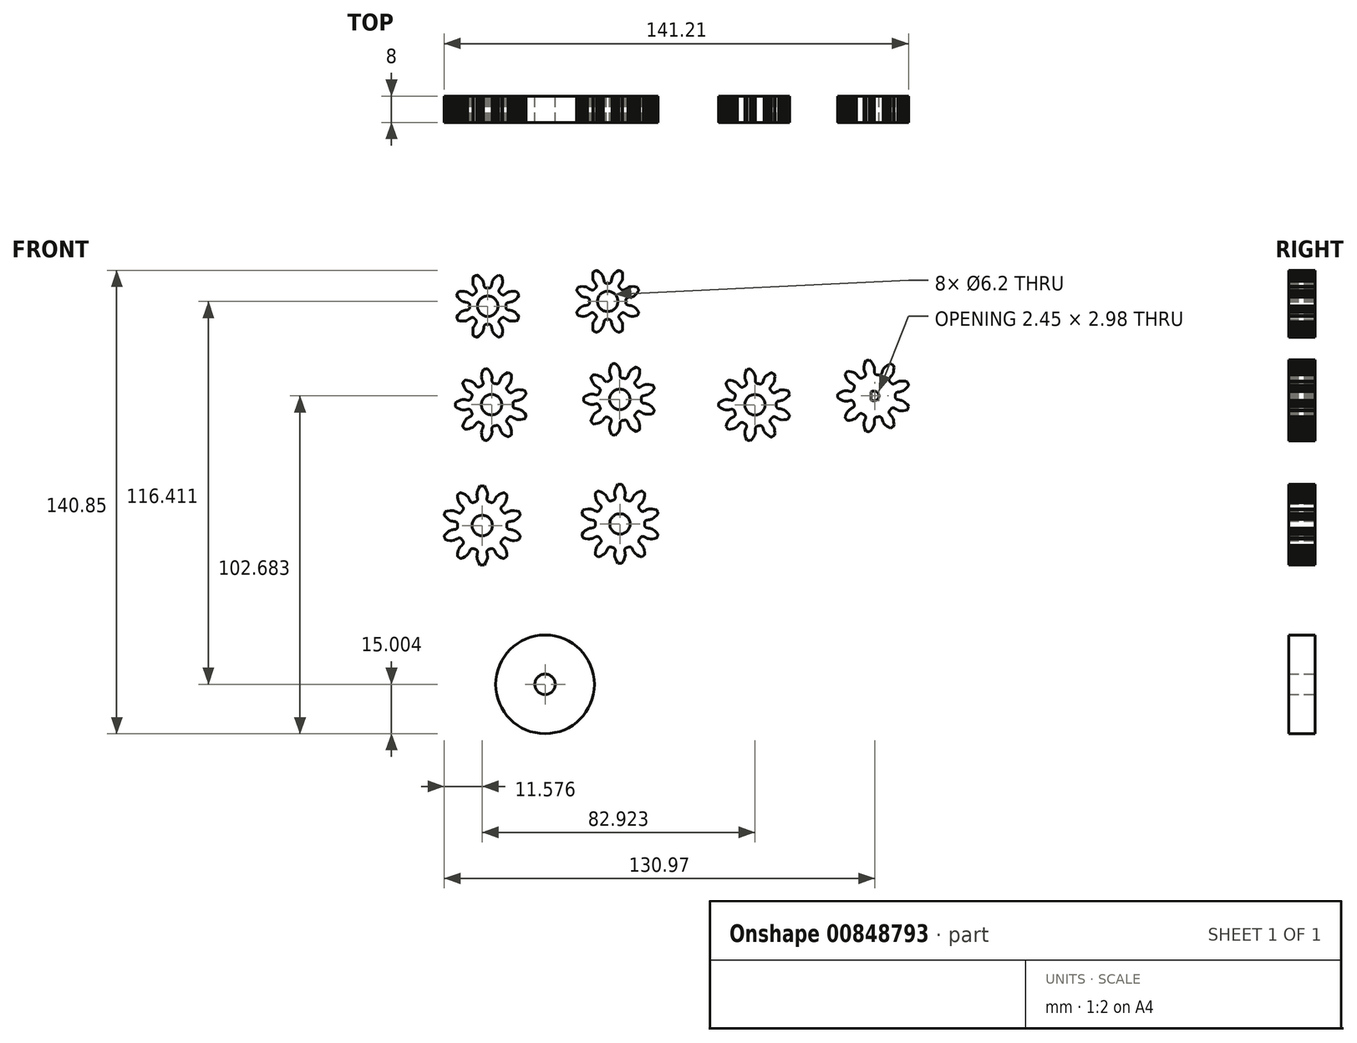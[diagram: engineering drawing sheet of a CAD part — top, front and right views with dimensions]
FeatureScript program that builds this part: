
annotation { "Feature Type Name" : "Feature", "Feature Type Description" : "" }
export const myFeature = defineFeature(function(context is Context, id is Id, definition is map)
    precondition{}
    {
        {
            var Q0;
            Q0=qCreatedBy(makeId("Front.planeOp"),FACE);
            var sketch = newSketch(context, id + "F0", { "sketchPlane" : qUnion([Q0])});
            skLineSegment(sketch, "E0", {"start": v(23.6, 118.61) * mm, "end": v(23.04, 118.9) * mm});
            skLineSegment(sketch, "E1", {"start": v(24.13, 118.4) * mm, "end": v(23.6, 118.61) * mm});
            skLineSegment(sketch, "E2", {"start": v(24.61, 118.29) * mm, "end": v(24.13, 118.4) * mm});
            skLineSegment(sketch, "E3", {"start": v(25.01, 118.25) * mm, "end": v(24.61, 118.29) * mm});
            skLineSegment(sketch, "E4", {"start": v(25.13, 118.25) * mm, "end": v(25.01, 118.25) * mm});
            skLineSegment(sketch, "E5", {"start": v(25.2, 118.26) * mm, "end": v(25.13, 118.25) * mm});
            skLineSegment(sketch, "E6", {"start": v(25.4, 118.3) * mm, "end": v(25.2, 118.26) * mm});
            skLineSegment(sketch, "E7", {"start": v(25.81, 118.38) * mm, "end": v(25.4, 118.3) * mm});
            skLineSegment(sketch, "E8", {"start": v(26.33, 118.48) * mm, "end": v(25.81, 118.38) * mm});
            skArc(sketch, "E9", {"start": v(22.48, 120.41) * mm, "mid": v(22.47, 119.85) * mm, "end": v(22.48, 119.28) * mm});
            skLineSegment(sketch, "E10", {"start": v(23.04, 120.8) * mm, "end": v(22.48, 120.41) * mm});
            skLineSegment(sketch, "E11", {"start": v(23.6, 121.08) * mm, "end": v(23.04, 120.8) * mm});
            skLineSegment(sketch, "E12", {"start": v(24.13, 121.3) * mm, "end": v(23.6, 121.08) * mm});
            skLineSegment(sketch, "E13", {"start": v(24.61, 121.41) * mm, "end": v(24.13, 121.3) * mm});
            skLineSegment(sketch, "E14", {"start": v(25.01, 121.45) * mm, "end": v(24.61, 121.41) * mm});
            skLineSegment(sketch, "E15", {"start": v(25.13, 121.45) * mm, "end": v(25.01, 121.45) * mm});
            skLineSegment(sketch, "E16", {"start": v(25.2, 121.43) * mm, "end": v(25.13, 121.45) * mm});
            skLineSegment(sketch, "E17", {"start": v(25.4, 121.4) * mm, "end": v(25.2, 121.43) * mm});
            skLineSegment(sketch, "E18", {"start": v(25.81, 121.32) * mm, "end": v(25.4, 121.4) * mm});
            skLineSegment(sketch, "E19", {"start": v(26.33, 121.22) * mm, "end": v(25.81, 121.32) * mm});
            skArc(sketch, "E20", {"start": v(26.33, 121.22) * mm, "mid": v(26.9, 121.32) * mm, "end": v(27.26, 121.78) * mm});
            skArc(sketch, "E21", {"start": v(27.47, 122.36) * mm, "mid": v(27.36, 122.07) * mm, "end": v(27.26, 121.78) * mm});
            skArc(sketch, "E22", {"start": v(27.47, 122.36) * mm, "mid": v(27.5, 122.94) * mm, "end": v(27.12, 123.39) * mm});
            skLineSegment(sketch, "E23", {"start": v(24.88, 125.83) * mm, "end": v(24.7, 126.48) * mm});
            skLineSegment(sketch, "E24", {"start": v(25.11, 125.25) * mm, "end": v(24.88, 125.83) * mm});
            skLineSegment(sketch, "E25", {"start": v(25.38, 124.75) * mm, "end": v(25.11, 125.25) * mm});
            skLineSegment(sketch, "E26", {"start": v(25.68, 124.34) * mm, "end": v(25.38, 124.75) * mm});
            skLineSegment(sketch, "E27", {"start": v(25.96, 124.06) * mm, "end": v(25.68, 124.34) * mm});
            skLineSegment(sketch, "E28", {"start": v(26.05, 123.99) * mm, "end": v(25.96, 124.06) * mm});
            skLineSegment(sketch, "E29", {"start": v(26.12, 123.94) * mm, "end": v(26.05, 123.99) * mm});
            skLineSegment(sketch, "E30", {"start": v(26.3, 123.84) * mm, "end": v(26.12, 123.94) * mm});
            skLineSegment(sketch, "E31", {"start": v(26.66, 123.65) * mm, "end": v(26.3, 123.84) * mm});
            skLineSegment(sketch, "E32", {"start": v(27.12, 123.39) * mm, "end": v(26.66, 123.65) * mm});
            skArc(sketch, "E33", {"start": v(25.42, 127.34) * mm, "mid": v(25.04, 126.92) * mm, "end": v(24.7, 126.48) * mm});
            skLineSegment(sketch, "E34", {"start": v(26.09, 127.27) * mm, "end": v(25.42, 127.34) * mm});
            skLineSegment(sketch, "E35", {"start": v(26.7, 127.14) * mm, "end": v(26.09, 127.27) * mm});
            skLineSegment(sketch, "E36", {"start": v(27.24, 126.96) * mm, "end": v(26.7, 127.14) * mm});
            skLineSegment(sketch, "E37", {"start": v(27.69, 126.74) * mm, "end": v(27.24, 126.96) * mm});
            skLineSegment(sketch, "E38", {"start": v(28.02, 126.51) * mm, "end": v(27.69, 126.74) * mm});
            skLineSegment(sketch, "E39", {"start": v(28.1, 126.43) * mm, "end": v(28.02, 126.51) * mm});
            skLineSegment(sketch, "E40", {"start": v(28.16, 126.37) * mm, "end": v(28.1, 126.43) * mm});
            skLineSegment(sketch, "E41", {"start": v(28.29, 126.22) * mm, "end": v(28.16, 126.37) * mm});
            skLineSegment(sketch, "E42", {"start": v(28.55, 125.9) * mm, "end": v(28.29, 126.22) * mm});
            skLineSegment(sketch, "E43", {"start": v(28.88, 125.5) * mm, "end": v(28.55, 125.9) * mm});
            skArc(sketch, "E44", {"start": v(28.88, 125.5) * mm, "mid": v(29.38, 125.2) * mm, "end": v(29.96, 125.32) * mm});
            skArc(sketch, "E45", {"start": v(30.49, 125.63) * mm, "mid": v(30.22, 125.48) * mm, "end": v(29.96, 125.32) * mm});
            skArc(sketch, "E46", {"start": v(30.49, 125.63) * mm, "mid": v(30.88, 126.06) * mm, "end": v(30.88, 126.64) * mm});
            skLineSegment(sketch, "E47", {"start": v(30.73, 129.95) * mm, "end": v(31, 130.57) * mm});
            skLineSegment(sketch, "E48", {"start": v(30.54, 129.36) * mm, "end": v(30.73, 129.95) * mm});
            skLineSegment(sketch, "E49", {"start": v(30.43, 128.8) * mm, "end": v(30.54, 129.36) * mm});
            skLineSegment(sketch, "E50", {"start": v(30.4, 128.3) * mm, "end": v(30.43, 128.8) * mm});
            skLineSegment(sketch, "E51", {"start": v(30.42, 127.9) * mm, "end": v(30.4, 128.3) * mm});
            skLineSegment(sketch, "E52", {"start": v(30.45, 127.78) * mm, "end": v(30.42, 127.9) * mm});
            skLineSegment(sketch, "E53", {"start": v(30.47, 127.7) * mm, "end": v(30.45, 127.78) * mm});
            skLineSegment(sketch, "E54", {"start": v(30.55, 127.52) * mm, "end": v(30.47, 127.7) * mm});
            skLineSegment(sketch, "E55", {"start": v(30.7, 127.14) * mm, "end": v(30.55, 127.52) * mm});
            skLineSegment(sketch, "E56", {"start": v(30.88, 126.64) * mm, "end": v(30.7, 127.14) * mm});
            skArc(sketch, "E57", {"start": v(32.12, 130.77) * mm, "mid": v(31.56, 130.68) * mm, "end": v(31, 130.57) * mm});
            skLineSegment(sketch, "E58", {"start": v(32.59, 130.28) * mm, "end": v(32.12, 130.77) * mm});
            skLineSegment(sketch, "E59", {"start": v(32.97, 129.79) * mm, "end": v(32.59, 130.28) * mm});
            skLineSegment(sketch, "E60", {"start": v(33.27, 129.3) * mm, "end": v(32.97, 129.79) * mm});
            skLineSegment(sketch, "E61", {"start": v(33.47, 128.84) * mm, "end": v(33.27, 129.3) * mm});
            skLineSegment(sketch, "E62", {"start": v(33.58, 128.46) * mm, "end": v(33.47, 128.84) * mm});
            skLineSegment(sketch, "E63", {"start": v(33.6, 128.34) * mm, "end": v(33.58, 128.46) * mm});
            skLineSegment(sketch, "E64", {"start": v(33.6, 128.26) * mm, "end": v(33.6, 128.34) * mm});
            skLineSegment(sketch, "E65", {"start": v(33.6, 128.05) * mm, "end": v(33.6, 128.26) * mm});
            skLineSegment(sketch, "E66", {"start": v(33.59, 127.65) * mm, "end": v(33.6, 128.05) * mm});
            skLineSegment(sketch, "E67", {"start": v(33.58, 127.12) * mm, "end": v(33.59, 127.65) * mm});
            skArc(sketch, "E68", {"start": v(33.58, 127.12) * mm, "mid": v(33.78, 126.57) * mm, "end": v(34.3, 126.3) * mm});
            skArc(sketch, "E69", {"start": v(34.9, 126.19) * mm, "mid": v(34.6, 126.25) * mm, "end": v(34.3, 126.3) * mm});
            skArc(sketch, "E70", {"start": v(34.9, 126.19) * mm, "mid": v(35.48, 126.27) * mm, "end": v(35.85, 126.72) * mm});
            skLineSegment(sketch, "E71", {"start": v(37.87, 129.35) * mm, "end": v(38.47, 129.65) * mm});
            skLineSegment(sketch, "E72", {"start": v(37.34, 129.02) * mm, "end": v(37.87, 129.35) * mm});
            skLineSegment(sketch, "E73", {"start": v(36.9, 128.66) * mm, "end": v(37.34, 129.02) * mm});
            skLineSegment(sketch, "E74", {"start": v(36.54, 128.3) * mm, "end": v(36.9, 128.66) * mm});
            skLineSegment(sketch, "E75", {"start": v(36.31, 127.98) * mm, "end": v(36.54, 128.3) * mm});
            skLineSegment(sketch, "E76", {"start": v(36.26, 127.87) * mm, "end": v(36.31, 127.98) * mm});
            skLineSegment(sketch, "E77", {"start": v(36.23, 127.8) * mm, "end": v(36.26, 127.87) * mm});
            skLineSegment(sketch, "E78", {"start": v(36.16, 127.6) * mm, "end": v(36.23, 127.8) * mm});
            skLineSegment(sketch, "E79", {"start": v(36.02, 127.22) * mm, "end": v(36.16, 127.6) * mm});
            skLineSegment(sketch, "E80", {"start": v(35.85, 126.72) * mm, "end": v(36.02, 127.22) * mm});
            skArc(sketch, "E81", {"start": v(39.45, 129.08) * mm, "mid": v(38.97, 129.38) * mm, "end": v(38.47, 129.65) * mm});
            skLineSegment(sketch, "E82", {"start": v(39.5, 128.4) * mm, "end": v(39.45, 129.08) * mm});
            skLineSegment(sketch, "E83", {"start": v(39.48, 127.78) * mm, "end": v(39.5, 128.4) * mm});
            skLineSegment(sketch, "E84", {"start": v(39.39, 127.22) * mm, "end": v(39.48, 127.78) * mm});
            skLineSegment(sketch, "E85", {"start": v(39.25, 126.74) * mm, "end": v(39.39, 127.22) * mm});
            skLineSegment(sketch, "E86", {"start": v(39.09, 126.37) * mm, "end": v(39.25, 126.74) * mm});
            skLineSegment(sketch, "E87", {"start": v(39.02, 126.27) * mm, "end": v(39.09, 126.37) * mm});
            skLineSegment(sketch, "E88", {"start": v(38.97, 126.21) * mm, "end": v(39.02, 126.27) * mm});
            skLineSegment(sketch, "E89", {"start": v(38.84, 126.06) * mm, "end": v(38.97, 126.21) * mm});
            skLineSegment(sketch, "E90", {"start": v(38.57, 125.75) * mm, "end": v(38.84, 126.06) * mm});
            skLineSegment(sketch, "E91", {"start": v(38.23, 125.35) * mm, "end": v(38.57, 125.75) * mm});
            skArc(sketch, "E92", {"start": v(38.23, 125.35) * mm, "mid": v(38.03, 124.8) * mm, "end": v(38.24, 124.26) * mm});
            skArc(sketch, "E93", {"start": v(38.64, 123.79) * mm, "mid": v(38.45, 124.03) * mm, "end": v(38.24, 124.26) * mm});
            skArc(sketch, "E94", {"start": v(38.64, 123.79) * mm, "mid": v(39.14, 123.48) * mm, "end": v(39.71, 123.58) * mm});
            skLineSegment(sketch, "E95", {"start": v(42.95, 124.3) * mm, "end": v(43.6, 124.14) * mm});
            skLineSegment(sketch, "E96", {"start": v(42.33, 124.39) * mm, "end": v(42.95, 124.3) * mm});
            skLineSegment(sketch, "E97", {"start": v(41.76, 124.4) * mm, "end": v(42.33, 124.39) * mm});
            skLineSegment(sketch, "E98", {"start": v(41.26, 124.35) * mm, "end": v(41.76, 124.4) * mm});
            skLineSegment(sketch, "E99", {"start": v(40.87, 124.25) * mm, "end": v(41.26, 124.35) * mm});
            skLineSegment(sketch, "E100", {"start": v(40.76, 124.2) * mm, "end": v(40.87, 124.25) * mm});
            skLineSegment(sketch, "E101", {"start": v(40.69, 124.16) * mm, "end": v(40.76, 124.2) * mm});
            skLineSegment(sketch, "E102", {"start": v(40.51, 124.06) * mm, "end": v(40.69, 124.16) * mm});
            skLineSegment(sketch, "E103", {"start": v(40.16, 123.85) * mm, "end": v(40.51, 124.06) * mm});
            skLineSegment(sketch, "E104", {"start": v(39.71, 123.58) * mm, "end": v(40.16, 123.85) * mm});
            skArc(sketch, "E105", {"start": v(43.99, 123.08) * mm, "mid": v(43.8, 123.61) * mm, "end": v(43.6, 124.14) * mm});
            skLineSegment(sketch, "E106", {"start": v(43.59, 122.53) * mm, "end": v(43.99, 123.08) * mm});
            skLineSegment(sketch, "E107", {"start": v(43.17, 122.07) * mm, "end": v(43.59, 122.53) * mm});
            skLineSegment(sketch, "E108", {"start": v(42.74, 121.69) * mm, "end": v(43.17, 122.07) * mm});
            skLineSegment(sketch, "E109", {"start": v(42.33, 121.4) * mm, "end": v(42.74, 121.69) * mm});
            skLineSegment(sketch, "E110", {"start": v(41.97, 121.24) * mm, "end": v(42.33, 121.4) * mm});
            skLineSegment(sketch, "E111", {"start": v(41.85, 121.2) * mm, "end": v(41.97, 121.24) * mm});
            skLineSegment(sketch, "E112", {"start": v(41.77, 121.19) * mm, "end": v(41.85, 121.2) * mm});
            skLineSegment(sketch, "E113", {"start": v(41.57, 121.15) * mm, "end": v(41.77, 121.19) * mm});
            skLineSegment(sketch, "E114", {"start": v(41.17, 121.09) * mm, "end": v(41.57, 121.15) * mm});
            skLineSegment(sketch, "E115", {"start": v(40.65, 121) * mm, "end": v(41.17, 121.09) * mm});
            skArc(sketch, "E116", {"start": v(40.65, 121) * mm, "mid": v(40.14, 120.71) * mm, "end": v(39.96, 120.16) * mm});
            skArc(sketch, "E117", {"start": v(39.96, 119.54) * mm, "mid": v(39.97, 119.85) * mm, "end": v(39.96, 120.16) * mm});
            skArc(sketch, "E118", {"start": v(39.96, 119.54) * mm, "mid": v(40.14, 118.99) * mm, "end": v(40.65, 118.7) * mm});
            skLineSegment(sketch, "E119", {"start": v(43.59, 117.17) * mm, "end": v(43.99, 116.62) * mm});
            skLineSegment(sketch, "E120", {"start": v(43.17, 117.63) * mm, "end": v(43.59, 117.17) * mm});
            skLineSegment(sketch, "E121", {"start": v(42.74, 118) * mm, "end": v(43.17, 117.63) * mm});
            skLineSegment(sketch, "E122", {"start": v(42.33, 118.29) * mm, "end": v(42.74, 118) * mm});
            skLineSegment(sketch, "E123", {"start": v(41.97, 118.46) * mm, "end": v(42.33, 118.29) * mm});
            skLineSegment(sketch, "E124", {"start": v(41.85, 118.5) * mm, "end": v(41.97, 118.46) * mm});
            skLineSegment(sketch, "E125", {"start": v(41.77, 118.51) * mm, "end": v(41.85, 118.5) * mm});
            skLineSegment(sketch, "E126", {"start": v(41.57, 118.55) * mm, "end": v(41.77, 118.51) * mm});
            skLineSegment(sketch, "E127", {"start": v(41.17, 118.61) * mm, "end": v(41.57, 118.55) * mm});
            skLineSegment(sketch, "E128", {"start": v(40.65, 118.7) * mm, "end": v(41.17, 118.61) * mm});
            skArc(sketch, "E129", {"start": v(43.6, 115.56) * mm, "mid": v(43.8, 116.09) * mm, "end": v(43.99, 116.62) * mm});
            skLineSegment(sketch, "E130", {"start": v(42.95, 115.4) * mm, "end": v(43.6, 115.56) * mm});
            skLineSegment(sketch, "E131", {"start": v(42.33, 115.31) * mm, "end": v(42.95, 115.4) * mm});
            skLineSegment(sketch, "E132", {"start": v(41.76, 115.3) * mm, "end": v(42.33, 115.31) * mm});
            skLineSegment(sketch, "E133", {"start": v(41.26, 115.35) * mm, "end": v(41.76, 115.3) * mm});
            skLineSegment(sketch, "E134", {"start": v(40.87, 115.45) * mm, "end": v(41.26, 115.35) * mm});
            skLineSegment(sketch, "E135", {"start": v(40.76, 115.5) * mm, "end": v(40.87, 115.45) * mm});
            skLineSegment(sketch, "E136", {"start": v(40.69, 115.53) * mm, "end": v(40.76, 115.5) * mm});
            skLineSegment(sketch, "E137", {"start": v(40.51, 115.64) * mm, "end": v(40.69, 115.53) * mm});
            skLineSegment(sketch, "E138", {"start": v(40.16, 115.85) * mm, "end": v(40.51, 115.64) * mm});
            skLineSegment(sketch, "E139", {"start": v(39.71, 116.12) * mm, "end": v(40.16, 115.85) * mm});
            skArc(sketch, "E140", {"start": v(39.71, 116.12) * mm, "mid": v(39.14, 116.22) * mm, "end": v(38.64, 115.91) * mm});
            skArc(sketch, "E141", {"start": v(38.24, 115.44) * mm, "mid": v(38.45, 115.67) * mm, "end": v(38.64, 115.91) * mm});
            skArc(sketch, "E142", {"start": v(38.24, 115.44) * mm, "mid": v(38.03, 114.9) * mm, "end": v(38.23, 114.35) * mm});
            skLineSegment(sketch, "E143", {"start": v(39.5, 111.29) * mm, "end": v(39.45, 110.62) * mm});
            skLineSegment(sketch, "E144", {"start": v(39.48, 111.92) * mm, "end": v(39.5, 111.29) * mm});
            skLineSegment(sketch, "E145", {"start": v(39.39, 112.48) * mm, "end": v(39.48, 111.92) * mm});
            skLineSegment(sketch, "E146", {"start": v(39.25, 112.96) * mm, "end": v(39.39, 112.48) * mm});
            skLineSegment(sketch, "E147", {"start": v(39.09, 113.32) * mm, "end": v(39.25, 112.96) * mm});
            skLineSegment(sketch, "E148", {"start": v(39.02, 113.43) * mm, "end": v(39.09, 113.32) * mm});
            skLineSegment(sketch, "E149", {"start": v(38.97, 113.49) * mm, "end": v(39.02, 113.43) * mm});
            skLineSegment(sketch, "E150", {"start": v(38.84, 113.64) * mm, "end": v(38.97, 113.49) * mm});
            skLineSegment(sketch, "E151", {"start": v(38.57, 113.95) * mm, "end": v(38.84, 113.64) * mm});
            skLineSegment(sketch, "E152", {"start": v(38.23, 114.35) * mm, "end": v(38.57, 113.95) * mm});
            skArc(sketch, "E153", {"start": v(38.47, 110.05) * mm, "mid": v(38.97, 110.32) * mm, "end": v(39.45, 110.62) * mm});
            skLineSegment(sketch, "E154", {"start": v(37.87, 110.35) * mm, "end": v(38.47, 110.05) * mm});
            skLineSegment(sketch, "E155", {"start": v(37.34, 110.68) * mm, "end": v(37.87, 110.35) * mm});
            skLineSegment(sketch, "E156", {"start": v(36.9, 111.04) * mm, "end": v(37.34, 110.68) * mm});
            skLineSegment(sketch, "E157", {"start": v(36.54, 111.4) * mm, "end": v(36.9, 111.04) * mm});
            skLineSegment(sketch, "E158", {"start": v(36.31, 111.72) * mm, "end": v(36.54, 111.4) * mm});
            skLineSegment(sketch, "E159", {"start": v(36.26, 111.83) * mm, "end": v(36.31, 111.72) * mm});
            skLineSegment(sketch, "E160", {"start": v(36.23, 111.9) * mm, "end": v(36.26, 111.83) * mm});
            skLineSegment(sketch, "E161", {"start": v(36.16, 112.1) * mm, "end": v(36.23, 111.9) * mm});
            skLineSegment(sketch, "E162", {"start": v(36.02, 112.48) * mm, "end": v(36.16, 112.1) * mm});
            skLineSegment(sketch, "E163", {"start": v(35.85, 112.98) * mm, "end": v(36.02, 112.48) * mm});
            skArc(sketch, "E164", {"start": v(35.85, 112.98) * mm, "mid": v(35.48, 113.43) * mm, "end": v(34.9, 113.5) * mm});
            skArc(sketch, "E165", {"start": v(-4.68, 111.79) * mm, "mid": v(-4.38, 111.83) * mm, "end": v(-4.07, 111.9) * mm});
            skArc(sketch, "E166", {"start": v(-4.68, 111.79) * mm, "mid": v(-5.2, 111.5) * mm, "end": v(-5.4, 110.96) * mm});
            skLineSegment(sketch, "E167", {"start": v(-6.39, 107.8) * mm, "end": v(-6.86, 107.32) * mm});
            skLineSegment(sketch, "E168", {"start": v(-6, 108.3) * mm, "end": v(-6.39, 107.8) * mm});
            skLineSegment(sketch, "E169", {"start": v(-5.7, 108.78) * mm, "end": v(-6, 108.3) * mm});
            skLineSegment(sketch, "E170", {"start": v(-5.5, 109.24) * mm, "end": v(-5.7, 108.78) * mm});
            skLineSegment(sketch, "E171", {"start": v(-5.4, 109.62) * mm, "end": v(-5.5, 109.24) * mm});
            skLineSegment(sketch, "E172", {"start": v(-5.38, 109.74) * mm, "end": v(-5.4, 109.62) * mm});
            skLineSegment(sketch, "E173", {"start": v(-5.38, 109.82) * mm, "end": v(-5.38, 109.74) * mm});
            skLineSegment(sketch, "E174", {"start": v(-5.38, 110.03) * mm, "end": v(-5.38, 109.82) * mm});
            skLineSegment(sketch, "E175", {"start": v(-5.39, 110.43) * mm, "end": v(-5.38, 110.03) * mm});
            skLineSegment(sketch, "E176", {"start": v(-5.4, 110.96) * mm, "end": v(-5.39, 110.43) * mm});
            skArc(sketch, "E177", {"start": v(-7.97, 107.51) * mm, "mid": v(-7.41, 107.4) * mm, "end": v(-6.86, 107.32) * mm});
            skLineSegment(sketch, "E178", {"start": v(-8.24, 108.13) * mm, "end": v(-7.97, 107.51) * mm});
            skLineSegment(sketch, "E179", {"start": v(-8.44, 108.72) * mm, "end": v(-8.24, 108.13) * mm});
            skLineSegment(sketch, "E180", {"start": v(-8.55, 109.28) * mm, "end": v(-8.44, 108.72) * mm});
            skLineSegment(sketch, "E181", {"start": v(-8.58, 109.78) * mm, "end": v(-8.55, 109.28) * mm});
            skLineSegment(sketch, "E182", {"start": v(-8.55, 110.18) * mm, "end": v(-8.58, 109.78) * mm});
            skLineSegment(sketch, "E183", {"start": v(-8.53, 110.3) * mm, "end": v(-8.55, 110.18) * mm});
            skLineSegment(sketch, "E184", {"start": v(-8.5, 110.37) * mm, "end": v(-8.53, 110.3) * mm});
            skLineSegment(sketch, "E185", {"start": v(-8.43, 110.56) * mm, "end": v(-8.5, 110.37) * mm});
            skLineSegment(sketch, "E186", {"start": v(-8.28, 110.95) * mm, "end": v(-8.43, 110.56) * mm});
            skArc(sketch, "E187", {"start": v(-8.1, 111.44) * mm, "mid": v(-8.1, 112.02) * mm, "end": v(-8.48, 112.46) * mm});
            skArc(sketch, "E188", {"start": v(-9.02, 112.76) * mm, "mid": v(-8.75, 112.6) * mm, "end": v(-8.48, 112.46) * mm});
            skArc(sketch, "E189", {"start": v(-9.02, 112.76) * mm, "mid": v(-9.59, 112.88) * mm, "end": v(-10.1, 112.6) * mm});
            skLineSegment(sketch, "E190", {"start": v(-12.89, 110.8) * mm, "end": v(-13.56, 110.74) * mm});
            skLineSegment(sketch, "E191", {"start": v(-12.27, 110.94) * mm, "end": v(-12.89, 110.8) * mm});
            skLineSegment(sketch, "E192", {"start": v(-11.73, 111.12) * mm, "end": v(-12.27, 110.94) * mm});
            skLineSegment(sketch, "E193", {"start": v(-11.28, 111.34) * mm, "end": v(-11.73, 111.12) * mm});
            skLineSegment(sketch, "E194", {"start": v(-10.95, 111.57) * mm, "end": v(-11.28, 111.34) * mm});
            skLineSegment(sketch, "E195", {"start": v(-10.87, 111.65) * mm, "end": v(-10.95, 111.57) * mm});
            skLineSegment(sketch, "E196", {"start": v(-10.81, 111.7) * mm, "end": v(-10.87, 111.65) * mm});
            skLineSegment(sketch, "E197", {"start": v(-10.68, 111.87) * mm, "end": v(-10.81, 111.7) * mm});
            skLineSegment(sketch, "E198", {"start": v(-10.43, 112.18) * mm, "end": v(-10.68, 111.87) * mm});
            skLineSegment(sketch, "E199", {"start": v(-10.1, 112.6) * mm, "end": v(-10.43, 112.18) * mm});
            skArc(sketch, "E200", {"start": v(-14.28, 111.6) * mm, "mid": v(-13.93, 111.16) * mm, "end": v(-13.56, 110.74) * mm});
            skLineSegment(sketch, "E201", {"start": v(-14.1, 112.25) * mm, "end": v(-14.28, 111.6) * mm});
            skLineSegment(sketch, "E202", {"start": v(-13.86, 112.83) * mm, "end": v(-14.1, 112.25) * mm});
            skLineSegment(sketch, "E203", {"start": v(-13.59, 113.33) * mm, "end": v(-13.86, 112.83) * mm});
            skLineSegment(sketch, "E204", {"start": v(-13.3, 113.74) * mm, "end": v(-13.59, 113.33) * mm});
            skLineSegment(sketch, "E205", {"start": v(-13.01, 114.02) * mm, "end": v(-13.3, 113.74) * mm});
            skLineSegment(sketch, "E206", {"start": v(-12.92, 114.1) * mm, "end": v(-13.01, 114.02) * mm});
            skLineSegment(sketch, "E207", {"start": v(-12.85, 114.14) * mm, "end": v(-12.92, 114.1) * mm});
            skLineSegment(sketch, "E208", {"start": v(-12.67, 114.24) * mm, "end": v(-12.85, 114.14) * mm});
            skLineSegment(sketch, "E209", {"start": v(-12.32, 114.44) * mm, "end": v(-12.67, 114.24) * mm});
            skLineSegment(sketch, "E210", {"start": v(-11.86, 114.7) * mm, "end": v(-12.32, 114.44) * mm});
            skArc(sketch, "E211", {"start": v(-11.86, 114.7) * mm, "mid": v(-11.48, 115.14) * mm, "end": v(-11.5, 115.72) * mm});
            skArc(sketch, "E212", {"start": v(-11.71, 116.3) * mm, "mid": v(-11.61, 116) * mm, "end": v(-11.5, 115.72) * mm});
            skArc(sketch, "E213", {"start": v(-11.71, 116.3) * mm, "mid": v(-12.07, 116.76) * mm, "end": v(-12.65, 116.86) * mm});
            skLineSegment(sketch, "E214", {"start": v(-15.93, 117.3) * mm, "end": v(-16.5, 117.67) * mm});
            skLineSegment(sketch, "E215", {"start": v(-15.38, 117) * mm, "end": v(-15.93, 117.3) * mm});
            skLineSegment(sketch, "E216", {"start": v(-14.85, 116.8) * mm, "end": v(-15.38, 117) * mm});
            skLineSegment(sketch, "E217", {"start": v(-14.36, 116.67) * mm, "end": v(-14.85, 116.8) * mm});
            skLineSegment(sketch, "E218", {"start": v(-13.96, 116.63) * mm, "end": v(-14.36, 116.67) * mm});
            skLineSegment(sketch, "E219", {"start": v(-13.84, 116.64) * mm, "end": v(-13.96, 116.63) * mm});
            skLineSegment(sketch, "E220", {"start": v(-13.76, 116.65) * mm, "end": v(-13.84, 116.64) * mm});
            skLineSegment(sketch, "E221", {"start": v(-13.56, 116.69) * mm, "end": v(-13.76, 116.65) * mm});
            skLineSegment(sketch, "E222", {"start": v(-13.16, 116.76) * mm, "end": v(-13.56, 116.69) * mm});
            skLineSegment(sketch, "E223", {"start": v(-12.65, 116.86) * mm, "end": v(-13.16, 116.76) * mm});
            skArc(sketch, "E224", {"start": v(-16.5, 118.8) * mm, "mid": v(-16.5, 118.23) * mm, "end": v(-16.5, 117.67) * mm});
            skLineSegment(sketch, "E225", {"start": v(-15.93, 119.17) * mm, "end": v(-16.5, 118.8) * mm});
            skLineSegment(sketch, "E226", {"start": v(-15.38, 119.47) * mm, "end": v(-15.93, 119.17) * mm});
            skLineSegment(sketch, "E227", {"start": v(-14.85, 119.68) * mm, "end": v(-15.38, 119.47) * mm});
            skLineSegment(sketch, "E228", {"start": v(-14.36, 119.8) * mm, "end": v(-14.85, 119.68) * mm});
            skLineSegment(sketch, "E229", {"start": v(-13.96, 119.83) * mm, "end": v(-14.36, 119.8) * mm});
            skLineSegment(sketch, "E230", {"start": v(-13.84, 119.83) * mm, "end": v(-13.96, 119.83) * mm});
            skLineSegment(sketch, "E231", {"start": v(-13.76, 119.82) * mm, "end": v(-13.84, 119.83) * mm});
            skLineSegment(sketch, "E232", {"start": v(-13.56, 119.78) * mm, "end": v(-13.76, 119.82) * mm});
            skLineSegment(sketch, "E233", {"start": v(-13.16, 119.7) * mm, "end": v(-13.56, 119.78) * mm});
            skLineSegment(sketch, "E234", {"start": v(-12.65, 119.6) * mm, "end": v(-13.16, 119.7) * mm});
            skArc(sketch, "E235", {"start": v(-12.65, 119.6) * mm, "mid": v(-12.07, 119.7) * mm, "end": v(-11.71, 120.16) * mm});
            skArc(sketch, "E236", {"start": v(-11.5, 120.74) * mm, "mid": v(-11.61, 120.46) * mm, "end": v(-11.71, 120.16) * mm});
            skArc(sketch, "E237", {"start": v(-11.5, 120.74) * mm, "mid": v(-11.48, 121.33) * mm, "end": v(-11.86, 121.77) * mm});
            skLineSegment(sketch, "E238", {"start": v(-14.1, 124.21) * mm, "end": v(-14.28, 124.86) * mm});
            skLineSegment(sketch, "E239", {"start": v(-13.86, 123.63) * mm, "end": v(-14.1, 124.21) * mm});
            skLineSegment(sketch, "E240", {"start": v(-13.59, 123.13) * mm, "end": v(-13.86, 123.63) * mm});
            skLineSegment(sketch, "E241", {"start": v(-13.3, 122.73) * mm, "end": v(-13.59, 123.13) * mm});
            skLineSegment(sketch, "E242", {"start": v(-13.01, 122.44) * mm, "end": v(-13.3, 122.73) * mm});
            skLineSegment(sketch, "E243", {"start": v(-12.92, 122.37) * mm, "end": v(-13.01, 122.44) * mm});
            skLineSegment(sketch, "E244", {"start": v(-12.85, 122.33) * mm, "end": v(-12.92, 122.37) * mm});
            skLineSegment(sketch, "E245", {"start": v(-12.67, 122.23) * mm, "end": v(-12.85, 122.33) * mm});
            skLineSegment(sketch, "E246", {"start": v(-12.32, 122.03) * mm, "end": v(-12.67, 122.23) * mm});
            skLineSegment(sketch, "E247", {"start": v(-11.86, 121.77) * mm, "end": v(-12.32, 122.03) * mm});
            skArc(sketch, "E248", {"start": v(-13.56, 125.73) * mm, "mid": v(-13.93, 125.3) * mm, "end": v(-14.28, 124.86) * mm});
            skLineSegment(sketch, "E249", {"start": v(-12.89, 125.66) * mm, "end": v(-13.56, 125.73) * mm});
            skLineSegment(sketch, "E250", {"start": v(-12.27, 125.53) * mm, "end": v(-12.89, 125.66) * mm});
            skLineSegment(sketch, "E251", {"start": v(-11.73, 125.34) * mm, "end": v(-12.27, 125.53) * mm});
            skLineSegment(sketch, "E252", {"start": v(-11.28, 125.12) * mm, "end": v(-11.73, 125.34) * mm});
            skLineSegment(sketch, "E253", {"start": v(-10.95, 124.9) * mm, "end": v(-11.28, 125.12) * mm});
            skLineSegment(sketch, "E254", {"start": v(-10.87, 124.82) * mm, "end": v(-10.95, 124.9) * mm});
            skLineSegment(sketch, "E255", {"start": v(-10.81, 124.76) * mm, "end": v(-10.87, 124.82) * mm});
            skLineSegment(sketch, "E256", {"start": v(-10.68, 124.6) * mm, "end": v(-10.81, 124.76) * mm});
            skLineSegment(sketch, "E257", {"start": v(-10.43, 124.28) * mm, "end": v(-10.68, 124.6) * mm});
            skLineSegment(sketch, "E258", {"start": v(-10.1, 123.87) * mm, "end": v(-10.43, 124.28) * mm});
            skArc(sketch, "E259", {"start": v(-10.1, 123.87) * mm, "mid": v(-9.59, 123.58) * mm, "end": v(-9.02, 123.7) * mm});
            skArc(sketch, "E260", {"start": v(-8.48, 124) * mm, "mid": v(-8.75, 123.86) * mm, "end": v(-9.02, 123.7) * mm});
            skArc(sketch, "E261", {"start": v(-8.48, 124) * mm, "mid": v(-8.1, 124.44) * mm, "end": v(-8.1, 125.03) * mm});
            skLineSegment(sketch, "E262", {"start": v(-8.24, 128.34) * mm, "end": v(-7.97, 128.95) * mm});
            skLineSegment(sketch, "E263", {"start": v(-8.44, 127.74) * mm, "end": v(-8.24, 128.34) * mm});
            skLineSegment(sketch, "E264", {"start": v(-8.55, 127.18) * mm, "end": v(-8.44, 127.74) * mm});
            skLineSegment(sketch, "E265", {"start": v(-8.58, 126.68) * mm, "end": v(-8.55, 127.18) * mm});
            skLineSegment(sketch, "E266", {"start": v(-8.55, 126.28) * mm, "end": v(-8.58, 126.68) * mm});
            skLineSegment(sketch, "E267", {"start": v(-8.53, 126.17) * mm, "end": v(-8.55, 126.28) * mm});
            skLineSegment(sketch, "E268", {"start": v(-8.5, 126.1) * mm, "end": v(-8.53, 126.17) * mm});
            skLineSegment(sketch, "E269", {"start": v(-8.43, 125.9) * mm, "end": v(-8.5, 126.1) * mm});
            skLineSegment(sketch, "E270", {"start": v(-8.28, 125.52) * mm, "end": v(-8.43, 125.9) * mm});
            skLineSegment(sketch, "E271", {"start": v(-8.1, 125.03) * mm, "end": v(-8.28, 125.52) * mm});
            skArc(sketch, "E272", {"start": v(-6.86, 129.15) * mm, "mid": v(-7.41, 129.07) * mm, "end": v(-7.97, 128.95) * mm});
            skLineSegment(sketch, "E273", {"start": v(-6.39, 128.67) * mm, "end": v(-6.86, 129.15) * mm});
            skLineSegment(sketch, "E274", {"start": v(-6, 128.17) * mm, "end": v(-6.39, 128.67) * mm});
            skLineSegment(sketch, "E275", {"start": v(-5.7, 127.68) * mm, "end": v(-6, 128.17) * mm});
            skLineSegment(sketch, "E276", {"start": v(-5.5, 127.23) * mm, "end": v(-5.7, 127.68) * mm});
            skLineSegment(sketch, "E277", {"start": v(-5.4, 126.84) * mm, "end": v(-5.5, 127.23) * mm});
            skLineSegment(sketch, "E278", {"start": v(-5.38, 126.72) * mm, "end": v(-5.4, 126.84) * mm});
            skLineSegment(sketch, "E279", {"start": v(-5.38, 126.64) * mm, "end": v(-5.38, 126.72) * mm});
            skLineSegment(sketch, "E280", {"start": v(-5.38, 126.44) * mm, "end": v(-5.38, 126.64) * mm});
            skLineSegment(sketch, "E281", {"start": v(-5.39, 126.03) * mm, "end": v(-5.38, 126.44) * mm});
            skLineSegment(sketch, "E282", {"start": v(-5.4, 125.5) * mm, "end": v(-5.39, 126.03) * mm});
            skArc(sketch, "E283", {"start": v(-5.4, 125.5) * mm, "mid": v(-5.2, 124.96) * mm, "end": v(-4.68, 124.68) * mm});
            skArc(sketch, "E284", {"start": v(-4.07, 124.57) * mm, "mid": v(-4.38, 124.63) * mm, "end": v(-4.68, 124.68) * mm});
            skArc(sketch, "E285", {"start": v(-4.07, 124.57) * mm, "mid": v(-3.5, 124.66) * mm, "end": v(-3.12, 125.1) * mm});
            skLineSegment(sketch, "E286", {"start": v(-1.1, 127.73) * mm, "end": v(-0.5, 128.03) * mm});
            skLineSegment(sketch, "E287", {"start": v(-1.64, 127.4) * mm, "end": v(-1.1, 127.73) * mm});
            skLineSegment(sketch, "E288", {"start": v(-2.08, 127.05) * mm, "end": v(-1.64, 127.4) * mm});
            skLineSegment(sketch, "E289", {"start": v(-2.43, 126.69) * mm, "end": v(-2.08, 127.05) * mm});
            skLineSegment(sketch, "E290", {"start": v(-2.66, 126.36) * mm, "end": v(-2.43, 126.69) * mm});
            skLineSegment(sketch, "E291", {"start": v(-2.72, 126.25) * mm, "end": v(-2.66, 126.36) * mm});
            skLineSegment(sketch, "E292", {"start": v(-2.75, 126.18) * mm, "end": v(-2.72, 126.25) * mm});
            skLineSegment(sketch, "E293", {"start": v(-2.81, 125.99) * mm, "end": v(-2.75, 126.18) * mm});
            skLineSegment(sketch, "E294", {"start": v(-2.95, 125.6) * mm, "end": v(-2.81, 125.99) * mm});
            skLineSegment(sketch, "E295", {"start": v(-3.12, 125.1) * mm, "end": v(-2.95, 125.6) * mm});
            skArc(sketch, "E296", {"start": v(0.48, 127.46) * mm, "mid": v(0, 127.76) * mm, "end": v(-0.5, 128.03) * mm});
            skLineSegment(sketch, "E297", {"start": v(0.52, 126.8) * mm, "end": v(0.48, 127.46) * mm});
            skLineSegment(sketch, "E298", {"start": v(0.5, 126.17) * mm, "end": v(0.52, 126.8) * mm});
            skLineSegment(sketch, "E299", {"start": v(0.42, 125.6) * mm, "end": v(0.5, 126.17) * mm});
            skLineSegment(sketch, "E300", {"start": v(0.28, 125.12) * mm, "end": v(0.42, 125.6) * mm});
            skLineSegment(sketch, "E301", {"start": v(0.11, 124.76) * mm, "end": v(0.28, 125.12) * mm});
            skLineSegment(sketch, "E302", {"start": v(0.05, 124.66) * mm, "end": v(0.11, 124.76) * mm});
            skLineSegment(sketch, "E303", {"start": v(0, 124.6) * mm, "end": v(0.05, 124.66) * mm});
            skLineSegment(sketch, "E304", {"start": v(-0.13, 124.44) * mm, "end": v(0, 124.6) * mm});
            skLineSegment(sketch, "E305", {"start": v(-0.4, 124.13) * mm, "end": v(-0.13, 124.44) * mm});
            skLineSegment(sketch, "E306", {"start": v(-0.75, 123.73) * mm, "end": v(-0.4, 124.13) * mm});
            skArc(sketch, "E307", {"start": v(-0.75, 123.73) * mm, "mid": v(-0.95, 123.18) * mm, "end": v(-0.73, 122.64) * mm});
            skArc(sketch, "E308", {"start": v(-0.33, 122.17) * mm, "mid": v(-0.53, 122.41) * mm, "end": v(-0.73, 122.64) * mm});
            skArc(sketch, "E309", {"start": v(-0.33, 122.17) * mm, "mid": v(0.16, 121.86) * mm, "end": v(0.74, 121.96) * mm});
            skLineSegment(sketch, "E310", {"start": v(3.97, 122.68) * mm, "end": v(4.63, 122.52) * mm});
            skLineSegment(sketch, "E311", {"start": v(3.35, 122.77) * mm, "end": v(3.97, 122.68) * mm});
            skLineSegment(sketch, "E312", {"start": v(2.78, 122.78) * mm, "end": v(3.35, 122.77) * mm});
            skLineSegment(sketch, "E313", {"start": v(2.28, 122.73) * mm, "end": v(2.78, 122.78) * mm});
            skLineSegment(sketch, "E314", {"start": v(1.9, 122.63) * mm, "end": v(2.28, 122.73) * mm});
            skLineSegment(sketch, "E315", {"start": v(1.79, 122.59) * mm, "end": v(1.9, 122.63) * mm});
            skLineSegment(sketch, "E316", {"start": v(1.72, 122.55) * mm, "end": v(1.79, 122.59) * mm});
            skLineSegment(sketch, "E317", {"start": v(1.54, 122.44) * mm, "end": v(1.72, 122.55) * mm});
            skLineSegment(sketch, "E318", {"start": v(1.19, 122.23) * mm, "end": v(1.54, 122.44) * mm});
            skLineSegment(sketch, "E319", {"start": v(0.74, 121.96) * mm, "end": v(1.19, 122.23) * mm});
            skArc(sketch, "E320", {"start": v(5.01, 121.46) * mm, "mid": v(4.83, 122) * mm, "end": v(4.63, 122.52) * mm});
            skLineSegment(sketch, "E321", {"start": v(4.62, 120.91) * mm, "end": v(5.01, 121.46) * mm});
            skLineSegment(sketch, "E322", {"start": v(4.2, 120.45) * mm, "end": v(4.62, 120.91) * mm});
            skLineSegment(sketch, "E323", {"start": v(3.77, 120.07) * mm, "end": v(4.2, 120.45) * mm});
            skLineSegment(sketch, "E324", {"start": v(3.35, 119.8) * mm, "end": v(3.77, 120.07) * mm});
            skLineSegment(sketch, "E325", {"start": v(3, 119.62) * mm, "end": v(3.35, 119.8) * mm});
            skLineSegment(sketch, "E326", {"start": v(2.88, 119.58) * mm, "end": v(3, 119.62) * mm});
            skLineSegment(sketch, "E327", {"start": v(2.8, 119.57) * mm, "end": v(2.88, 119.58) * mm});
            skLineSegment(sketch, "E328", {"start": v(2.6, 119.54) * mm, "end": v(2.8, 119.57) * mm});
            skLineSegment(sketch, "E329", {"start": v(2.2, 119.47) * mm, "end": v(2.6, 119.54) * mm});
            skLineSegment(sketch, "E330", {"start": v(1.68, 119.39) * mm, "end": v(2.2, 119.47) * mm});
            skArc(sketch, "E331", {"start": v(1.68, 119.39) * mm, "mid": v(1.17, 119.1) * mm, "end": v(0.99, 118.54) * mm});
            skArc(sketch, "E332", {"start": v(0.99, 117.92) * mm, "mid": v(1, 118.23) * mm, "end": v(0.99, 118.54) * mm});
            skArc(sketch, "E333", {"start": v(0.99, 117.92) * mm, "mid": v(1.17, 117.37) * mm, "end": v(1.68, 117.08) * mm});
            skLineSegment(sketch, "E334", {"start": v(4.62, 115.55) * mm, "end": v(5.01, 115) * mm});
            skLineSegment(sketch, "E335", {"start": v(4.2, 116.02) * mm, "end": v(4.62, 115.55) * mm});
            skLineSegment(sketch, "E336", {"start": v(3.77, 116.4) * mm, "end": v(4.2, 116.02) * mm});
            skLineSegment(sketch, "E337", {"start": v(3.35, 116.67) * mm, "end": v(3.77, 116.4) * mm});
            skLineSegment(sketch, "E338", {"start": v(3, 116.85) * mm, "end": v(3.35, 116.67) * mm});
            skLineSegment(sketch, "E339", {"start": v(2.88, 116.88) * mm, "end": v(3, 116.85) * mm});
            skLineSegment(sketch, "E340", {"start": v(2.8, 116.9) * mm, "end": v(2.88, 116.88) * mm});
            skLineSegment(sketch, "E341", {"start": v(2.6, 116.93) * mm, "end": v(2.8, 116.9) * mm});
            skLineSegment(sketch, "E342", {"start": v(2.2, 117) * mm, "end": v(2.6, 116.93) * mm});
            skLineSegment(sketch, "E343", {"start": v(1.68, 117.08) * mm, "end": v(2.2, 117) * mm});
            skArc(sketch, "E344", {"start": v(4.63, 113.94) * mm, "mid": v(4.83, 114.47) * mm, "end": v(5.01, 115) * mm});
            skLineSegment(sketch, "E345", {"start": v(3.97, 113.78) * mm, "end": v(4.63, 113.94) * mm});
            skLineSegment(sketch, "E346", {"start": v(3.35, 113.7) * mm, "end": v(3.97, 113.78) * mm});
            skLineSegment(sketch, "E347", {"start": v(2.78, 113.68) * mm, "end": v(3.35, 113.7) * mm});
            skLineSegment(sketch, "E348", {"start": v(2.28, 113.73) * mm, "end": v(2.78, 113.68) * mm});
            skLineSegment(sketch, "E349", {"start": v(1.9, 113.83) * mm, "end": v(2.28, 113.73) * mm});
            skLineSegment(sketch, "E350", {"start": v(1.79, 113.88) * mm, "end": v(1.9, 113.83) * mm});
            skLineSegment(sketch, "E351", {"start": v(1.72, 113.92) * mm, "end": v(1.79, 113.88) * mm});
            skLineSegment(sketch, "E352", {"start": v(1.54, 114.02) * mm, "end": v(1.72, 113.92) * mm});
            skLineSegment(sketch, "E353", {"start": v(1.19, 114.23) * mm, "end": v(1.54, 114.02) * mm});
            skLineSegment(sketch, "E354", {"start": v(0.74, 114.5) * mm, "end": v(1.19, 114.23) * mm});
            skArc(sketch, "E355", {"start": v(0.74, 114.5) * mm, "mid": v(0.16, 114.6) * mm, "end": v(-0.33, 114.3) * mm});
            skArc(sketch, "E356", {"start": v(-0.73, 113.82) * mm, "mid": v(-0.53, 114.05) * mm, "end": v(-0.33, 114.3) * mm});
            skArc(sketch, "E357", {"start": v(-0.73, 113.82) * mm, "mid": v(-0.95, 113.28) * mm, "end": v(-0.75, 112.73) * mm});
            skLineSegment(sketch, "E358", {"start": v(0.52, 109.67) * mm, "end": v(0.48, 109) * mm});
            skLineSegment(sketch, "E359", {"start": v(0.5, 110.3) * mm, "end": v(0.52, 109.67) * mm});
            skLineSegment(sketch, "E360", {"start": v(0.42, 110.86) * mm, "end": v(0.5, 110.3) * mm});
            skLineSegment(sketch, "E361", {"start": v(0.28, 111.34) * mm, "end": v(0.42, 110.86) * mm});
            skLineSegment(sketch, "E362", {"start": v(0.11, 111.7) * mm, "end": v(0.28, 111.34) * mm});
            skLineSegment(sketch, "E363", {"start": v(0.05, 111.8) * mm, "end": v(0.11, 111.7) * mm});
            skLineSegment(sketch, "E364", {"start": v(0, 111.87) * mm, "end": v(0.05, 111.8) * mm});
            skLineSegment(sketch, "E365", {"start": v(-0.13, 112.03) * mm, "end": v(0, 111.87) * mm});
            skLineSegment(sketch, "E366", {"start": v(-0.4, 112.34) * mm, "end": v(-0.13, 112.03) * mm});
            skLineSegment(sketch, "E367", {"start": v(-0.75, 112.73) * mm, "end": v(-0.4, 112.34) * mm});
            skArc(sketch, "E368", {"start": v(-0.5, 108.44) * mm, "mid": v(0, 108.7) * mm, "end": v(0.48, 109) * mm});
            skLineSegment(sketch, "E369", {"start": v(-1.1, 108.73) * mm, "end": v(-0.5, 108.44) * mm});
            skLineSegment(sketch, "E370", {"start": v(-1.64, 109.06) * mm, "end": v(-1.1, 108.73) * mm});
            skLineSegment(sketch, "E371", {"start": v(-2.08, 109.42) * mm, "end": v(-1.64, 109.06) * mm});
            skLineSegment(sketch, "E372", {"start": v(-2.43, 109.78) * mm, "end": v(-2.08, 109.42) * mm});
            skLineSegment(sketch, "E373", {"start": v(-2.66, 110.1) * mm, "end": v(-2.43, 109.78) * mm});
            skLineSegment(sketch, "E374", {"start": v(-2.72, 110.21) * mm, "end": v(-2.66, 110.1) * mm});
            skLineSegment(sketch, "E375", {"start": v(-2.75, 110.29) * mm, "end": v(-2.72, 110.21) * mm});
            skLineSegment(sketch, "E376", {"start": v(-2.81, 110.48) * mm, "end": v(-2.75, 110.29) * mm});
            skLineSegment(sketch, "E377", {"start": v(-2.95, 110.86) * mm, "end": v(-2.81, 110.48) * mm});
            skLineSegment(sketch, "E378", {"start": v(-3.12, 111.36) * mm, "end": v(-2.95, 110.86) * mm});
            skArc(sketch, "E379", {"start": v(-3.12, 111.36) * mm, "mid": v(-3.5, 111.8) * mm, "end": v(-4.07, 111.9) * mm});
            skArc(sketch, "E380", {"start": v(-3, 144.08) * mm, "mid": v(-2.8, 144.28) * mm, "end": v(-2.59, 144.49) * mm});
            skArc(sketch, "E381", {"start": v(-3, 144.08) * mm, "mid": v(-3.26, 143.57) * mm, "end": v(-3.13, 143.02) * mm});
            skLineSegment(sketch, "E382", {"start": v(-2.21, 139.8) * mm, "end": v(-2.36, 139.15) * mm});
            skLineSegment(sketch, "E383", {"start": v(-2.15, 140.41) * mm, "end": v(-2.21, 139.8) * mm});
            skLineSegment(sketch, "E384", {"start": v(-2.15, 140.97) * mm, "end": v(-2.15, 140.41) * mm});
            skLineSegment(sketch, "E385", {"start": v(-2.22, 141.46) * mm, "end": v(-2.15, 140.97) * mm});
            skLineSegment(sketch, "E386", {"start": v(-2.34, 141.84) * mm, "end": v(-2.22, 141.46) * mm});
            skLineSegment(sketch, "E387", {"start": v(-2.37, 141.9) * mm, "end": v(-2.34, 141.84) * mm});
            skLineSegment(sketch, "E388", {"start": v(-2.4, 141.95) * mm, "end": v(-2.37, 141.9) * mm});
            skLineSegment(sketch, "E389", {"start": v(-2.43, 142.01) * mm, "end": v(-2.4, 141.95) * mm});
            skLineSegment(sketch, "E390", {"start": v(-2.55, 142.2) * mm, "end": v(-2.43, 142.01) * mm});
            skLineSegment(sketch, "E391", {"start": v(-2.8, 142.55) * mm, "end": v(-2.55, 142.2) * mm});
            skLineSegment(sketch, "E392", {"start": v(-3.13, 143.02) * mm, "end": v(-2.8, 142.55) * mm});
            skArc(sketch, "E393", {"start": v(-3.36, 138.73) * mm, "mid": v(-2.85, 138.93) * mm, "end": v(-2.36, 139.15) * mm});
            skLineSegment(sketch, "E394", {"start": v(-3.92, 139.09) * mm, "end": v(-3.36, 138.73) * mm});
            skLineSegment(sketch, "E395", {"start": v(-4.4, 139.48) * mm, "end": v(-3.92, 139.09) * mm});
            skLineSegment(sketch, "E396", {"start": v(-4.8, 139.88) * mm, "end": v(-4.4, 139.48) * mm});
            skLineSegment(sketch, "E397", {"start": v(-5.1, 140.27) * mm, "end": v(-4.8, 139.88) * mm});
            skLineSegment(sketch, "E398", {"start": v(-5.28, 140.63) * mm, "end": v(-5.1, 140.27) * mm});
            skLineSegment(sketch, "E399", {"start": v(-5.3, 140.69) * mm, "end": v(-5.28, 140.63) * mm});
            skLineSegment(sketch, "E400", {"start": v(-5.32, 140.74) * mm, "end": v(-5.3, 140.69) * mm});
            skLineSegment(sketch, "E401", {"start": v(-5.33, 140.81) * mm, "end": v(-5.32, 140.74) * mm});
            skLineSegment(sketch, "E402", {"start": v(-5.37, 141.02) * mm, "end": v(-5.33, 140.81) * mm});
            skLineSegment(sketch, "E403", {"start": v(-5.45, 141.45) * mm, "end": v(-5.37, 141.02) * mm});
            skLineSegment(sketch, "E404", {"start": v(-5.55, 142.01) * mm, "end": v(-5.45, 141.45) * mm});
            skArc(sketch, "E405", {"start": v(-5.55, 142.01) * mm, "mid": v(-5.85, 142.5) * mm, "end": v(-6.39, 142.67) * mm});
            skArc(sketch, "E406", {"start": v(-6.97, 142.67) * mm, "mid": v(-6.68, 142.67) * mm, "end": v(-6.39, 142.67) * mm});
            skArc(sketch, "E407", {"start": v(-6.97, 142.67) * mm, "mid": v(-7.51, 142.5) * mm, "end": v(-7.8, 142.01) * mm});
            skLineSegment(sketch, "E408", {"start": v(-9.44, 139.09) * mm, "end": v(-10, 138.73) * mm});
            skLineSegment(sketch, "E409", {"start": v(-8.96, 139.48) * mm, "end": v(-9.44, 139.09) * mm});
            skLineSegment(sketch, "E410", {"start": v(-8.56, 139.88) * mm, "end": v(-8.96, 139.48) * mm});
            skLineSegment(sketch, "E411", {"start": v(-8.27, 140.27) * mm, "end": v(-8.56, 139.88) * mm});
            skLineSegment(sketch, "E412", {"start": v(-8.08, 140.63) * mm, "end": v(-8.27, 140.27) * mm});
            skLineSegment(sketch, "E413", {"start": v(-8.06, 140.69) * mm, "end": v(-8.08, 140.63) * mm});
            skLineSegment(sketch, "E414", {"start": v(-8.04, 140.74) * mm, "end": v(-8.06, 140.69) * mm});
            skLineSegment(sketch, "E415", {"start": v(-8.03, 140.81) * mm, "end": v(-8.04, 140.74) * mm});
            skLineSegment(sketch, "E416", {"start": v(-7.99, 141.02) * mm, "end": v(-8.03, 140.81) * mm});
            skLineSegment(sketch, "E417", {"start": v(-7.9, 141.45) * mm, "end": v(-7.99, 141.02) * mm});
            skLineSegment(sketch, "E418", {"start": v(-7.8, 142.01) * mm, "end": v(-7.9, 141.45) * mm});
            skArc(sketch, "E419", {"start": v(-11, 139.15) * mm, "mid": v(-10.5, 138.93) * mm, "end": v(-10, 138.73) * mm});
            skLineSegment(sketch, "E420", {"start": v(-11.15, 139.8) * mm, "end": v(-11, 139.15) * mm});
            skLineSegment(sketch, "E421", {"start": v(-11.21, 140.41) * mm, "end": v(-11.15, 139.8) * mm});
            skLineSegment(sketch, "E422", {"start": v(-11.2, 140.97) * mm, "end": v(-11.21, 140.41) * mm});
            skLineSegment(sketch, "E423", {"start": v(-11.14, 141.46) * mm, "end": v(-11.2, 140.97) * mm});
            skLineSegment(sketch, "E424", {"start": v(-11.02, 141.84) * mm, "end": v(-11.14, 141.46) * mm});
            skLineSegment(sketch, "E425", {"start": v(-11, 141.9) * mm, "end": v(-11.02, 141.84) * mm});
            skLineSegment(sketch, "E426", {"start": v(-10.97, 141.95) * mm, "end": v(-11, 141.9) * mm});
            skLineSegment(sketch, "E427", {"start": v(-10.93, 142.01) * mm, "end": v(-10.97, 141.95) * mm});
            skLineSegment(sketch, "E428", {"start": v(-10.8, 142.2) * mm, "end": v(-10.93, 142.01) * mm});
            skLineSegment(sketch, "E429", {"start": v(-10.56, 142.55) * mm, "end": v(-10.8, 142.2) * mm});
            skLineSegment(sketch, "E430", {"start": v(-10.23, 143.02) * mm, "end": v(-10.56, 142.55) * mm});
            skArc(sketch, "E431", {"start": v(-10.23, 143.02) * mm, "mid": v(-10.1, 143.57) * mm, "end": v(-10.36, 144.08) * mm});
            skArc(sketch, "E432", {"start": v(-10.77, 144.49) * mm, "mid": v(-10.57, 144.28) * mm, "end": v(-10.36, 144.08) * mm});
            skArc(sketch, "E433", {"start": v(-10.77, 144.49) * mm, "mid": v(-11.28, 144.75) * mm, "end": v(-11.83, 144.61) * mm});
            skLineSegment(sketch, "E434", {"start": v(-15.05, 143.7) * mm, "end": v(-15.7, 143.85) * mm});
            skLineSegment(sketch, "E435", {"start": v(-14.44, 143.63) * mm, "end": v(-15.05, 143.7) * mm});
            skLineSegment(sketch, "E436", {"start": v(-13.87, 143.64) * mm, "end": v(-14.44, 143.63) * mm});
            skLineSegment(sketch, "E437", {"start": v(-13.38, 143.7) * mm, "end": v(-13.87, 143.64) * mm});
            skLineSegment(sketch, "E438", {"start": v(-13, 143.83) * mm, "end": v(-13.38, 143.7) * mm});
            skLineSegment(sketch, "E439", {"start": v(-12.94, 143.86) * mm, "end": v(-13, 143.83) * mm});
            skLineSegment(sketch, "E440", {"start": v(-12.9, 143.88) * mm, "end": v(-12.94, 143.86) * mm});
            skLineSegment(sketch, "E441", {"start": v(-12.83, 143.92) * mm, "end": v(-12.9, 143.88) * mm});
            skLineSegment(sketch, "E442", {"start": v(-12.66, 144.04) * mm, "end": v(-12.83, 143.92) * mm});
            skLineSegment(sketch, "E443", {"start": v(-12.3, 144.29) * mm, "end": v(-12.66, 144.04) * mm});
            skLineSegment(sketch, "E444", {"start": v(-11.83, 144.61) * mm, "end": v(-12.3, 144.29) * mm});
            skArc(sketch, "E445", {"start": v(-16.11, 144.84) * mm, "mid": v(-15.92, 144.34) * mm, "end": v(-15.7, 143.85) * mm});
            skLineSegment(sketch, "E446", {"start": v(-15.76, 145.4) * mm, "end": v(-16.11, 144.84) * mm});
            skLineSegment(sketch, "E447", {"start": v(-15.37, 145.89) * mm, "end": v(-15.76, 145.4) * mm});
            skLineSegment(sketch, "E448", {"start": v(-14.97, 146.28) * mm, "end": v(-15.37, 145.89) * mm});
            skLineSegment(sketch, "E449", {"start": v(-14.57, 146.58) * mm, "end": v(-14.97, 146.28) * mm});
            skLineSegment(sketch, "E450", {"start": v(-14.22, 146.76) * mm, "end": v(-14.57, 146.58) * mm});
            skLineSegment(sketch, "E451", {"start": v(-14.16, 146.79) * mm, "end": v(-14.22, 146.76) * mm});
            skLineSegment(sketch, "E452", {"start": v(-14.1, 146.8) * mm, "end": v(-14.16, 146.79) * mm});
            skLineSegment(sketch, "E453", {"start": v(-14.03, 146.82) * mm, "end": v(-14.1, 146.8) * mm});
            skLineSegment(sketch, "E454", {"start": v(-13.82, 146.86) * mm, "end": v(-14.03, 146.82) * mm});
            skLineSegment(sketch, "E455", {"start": v(-13.4, 146.94) * mm, "end": v(-13.82, 146.86) * mm});
            skLineSegment(sketch, "E456", {"start": v(-12.83, 147.04) * mm, "end": v(-13.4, 146.94) * mm});
            skArc(sketch, "E457", {"start": v(-12.83, 147.04) * mm, "mid": v(-12.34, 147.33) * mm, "end": v(-12.17, 147.87) * mm});
            skArc(sketch, "E458", {"start": v(-12.17, 148.46) * mm, "mid": v(-12.18, 148.17) * mm, "end": v(-12.17, 147.87) * mm});
            skArc(sketch, "E459", {"start": v(-12.17, 148.46) * mm, "mid": v(-12.34, 149) * mm, "end": v(-12.83, 149.3) * mm});
            skLineSegment(sketch, "E460", {"start": v(-15.76, 150.93) * mm, "end": v(-16.11, 151.49) * mm});
            skLineSegment(sketch, "E461", {"start": v(-15.37, 150.44) * mm, "end": v(-15.76, 150.93) * mm});
            skLineSegment(sketch, "E462", {"start": v(-14.97, 150.05) * mm, "end": v(-15.37, 150.44) * mm});
            skLineSegment(sketch, "E463", {"start": v(-14.57, 149.76) * mm, "end": v(-14.97, 150.05) * mm});
            skLineSegment(sketch, "E464", {"start": v(-14.22, 149.57) * mm, "end": v(-14.57, 149.76) * mm});
            skLineSegment(sketch, "E465", {"start": v(-14.16, 149.55) * mm, "end": v(-14.22, 149.57) * mm});
            skLineSegment(sketch, "E466", {"start": v(-14.1, 149.53) * mm, "end": v(-14.16, 149.55) * mm});
            skLineSegment(sketch, "E467", {"start": v(-14.03, 149.51) * mm, "end": v(-14.1, 149.53) * mm});
            skLineSegment(sketch, "E468", {"start": v(-13.82, 149.47) * mm, "end": v(-14.03, 149.51) * mm});
            skLineSegment(sketch, "E469", {"start": v(-13.4, 149.4) * mm, "end": v(-13.82, 149.47) * mm});
            skLineSegment(sketch, "E470", {"start": v(-12.83, 149.3) * mm, "end": v(-13.4, 149.4) * mm});
            skArc(sketch, "E471", {"start": v(-15.7, 152.49) * mm, "mid": v(-15.92, 152) * mm, "end": v(-16.11, 151.49) * mm});
            skLineSegment(sketch, "E472", {"start": v(-15.05, 152.63) * mm, "end": v(-15.7, 152.49) * mm});
            skLineSegment(sketch, "E473", {"start": v(-14.44, 152.7) * mm, "end": v(-15.05, 152.63) * mm});
            skLineSegment(sketch, "E474", {"start": v(-13.87, 152.7) * mm, "end": v(-14.44, 152.7) * mm});
            skLineSegment(sketch, "E475", {"start": v(-13.38, 152.62) * mm, "end": v(-13.87, 152.7) * mm});
            skLineSegment(sketch, "E476", {"start": v(-13, 152.5) * mm, "end": v(-13.38, 152.62) * mm});
            skLineSegment(sketch, "E477", {"start": v(-12.94, 152.48) * mm, "end": v(-13, 152.5) * mm});
            skLineSegment(sketch, "E478", {"start": v(-12.9, 152.45) * mm, "end": v(-12.94, 152.48) * mm});
            skLineSegment(sketch, "E479", {"start": v(-12.83, 152.41) * mm, "end": v(-12.9, 152.45) * mm});
            skLineSegment(sketch, "E480", {"start": v(-12.66, 152.3) * mm, "end": v(-12.83, 152.41) * mm});
            skLineSegment(sketch, "E481", {"start": v(-12.3, 152.04) * mm, "end": v(-12.66, 152.3) * mm});
            skLineSegment(sketch, "E482", {"start": v(-11.83, 151.72) * mm, "end": v(-12.3, 152.04) * mm});
            skArc(sketch, "E483", {"start": v(-11.83, 151.72) * mm, "mid": v(-11.28, 151.58) * mm, "end": v(-10.77, 151.84) * mm});
            skArc(sketch, "E484", {"start": v(-10.36, 152.26) * mm, "mid": v(-10.57, 152.06) * mm, "end": v(-10.77, 151.84) * mm});
            skArc(sketch, "E485", {"start": v(-10.36, 152.26) * mm, "mid": v(-10.1, 152.76) * mm, "end": v(-10.23, 153.31) * mm});
            skLineSegment(sketch, "E486", {"start": v(-11.15, 156.54) * mm, "end": v(-11, 157.19) * mm});
            skLineSegment(sketch, "E487", {"start": v(-11.21, 155.92) * mm, "end": v(-11.15, 156.54) * mm});
            skLineSegment(sketch, "E488", {"start": v(-11.2, 155.36) * mm, "end": v(-11.21, 155.92) * mm});
            skLineSegment(sketch, "E489", {"start": v(-11.14, 154.87) * mm, "end": v(-11.2, 155.36) * mm});
            skLineSegment(sketch, "E490", {"start": v(-11.02, 154.5) * mm, "end": v(-11.14, 154.87) * mm});
            skLineSegment(sketch, "E491", {"start": v(-11, 154.43) * mm, "end": v(-11.02, 154.5) * mm});
            skLineSegment(sketch, "E492", {"start": v(-10.97, 154.38) * mm, "end": v(-11, 154.43) * mm});
            skLineSegment(sketch, "E493", {"start": v(-10.93, 154.32) * mm, "end": v(-10.97, 154.38) * mm});
            skLineSegment(sketch, "E494", {"start": v(-10.8, 154.14) * mm, "end": v(-10.93, 154.32) * mm});
            skLineSegment(sketch, "E495", {"start": v(-10.56, 153.78) * mm, "end": v(-10.8, 154.14) * mm});
            skLineSegment(sketch, "E496", {"start": v(-10.23, 153.31) * mm, "end": v(-10.56, 153.78) * mm});
            skArc(sketch, "E497", {"start": v(-10, 157.6) * mm, "mid": v(-10.5, 157.4) * mm, "end": v(-11, 157.19) * mm});
            skLineSegment(sketch, "E498", {"start": v(-9.44, 157.24) * mm, "end": v(-10, 157.6) * mm});
            skLineSegment(sketch, "E499", {"start": v(-8.96, 156.86) * mm, "end": v(-9.44, 157.24) * mm});
            skLineSegment(sketch, "E500", {"start": v(-8.56, 156.45) * mm, "end": v(-8.96, 156.86) * mm});
            skLineSegment(sketch, "E501", {"start": v(-8.27, 156.06) * mm, "end": v(-8.56, 156.45) * mm});
            skLineSegment(sketch, "E502", {"start": v(-8.08, 155.7) * mm, "end": v(-8.27, 156.06) * mm});
            skLineSegment(sketch, "E503", {"start": v(-8.06, 155.64) * mm, "end": v(-8.08, 155.7) * mm});
            skLineSegment(sketch, "E504", {"start": v(-8.04, 155.6) * mm, "end": v(-8.06, 155.64) * mm});
            skLineSegment(sketch, "E505", {"start": v(-8.03, 155.52) * mm, "end": v(-8.04, 155.6) * mm});
            skLineSegment(sketch, "E506", {"start": v(-7.99, 155.3) * mm, "end": v(-8.03, 155.52) * mm});
            skLineSegment(sketch, "E507", {"start": v(-7.9, 154.88) * mm, "end": v(-7.99, 155.3) * mm});
            skLineSegment(sketch, "E508", {"start": v(-7.8, 154.32) * mm, "end": v(-7.9, 154.88) * mm});
            skArc(sketch, "E509", {"start": v(-7.8, 154.32) * mm, "mid": v(-7.51, 153.83) * mm, "end": v(-6.97, 153.66) * mm});
            skArc(sketch, "E510", {"start": v(-6.39, 153.66) * mm, "mid": v(-6.68, 153.67) * mm, "end": v(-6.97, 153.66) * mm});
            skArc(sketch, "E511", {"start": v(-6.39, 153.66) * mm, "mid": v(-5.85, 153.83) * mm, "end": v(-5.55, 154.32) * mm});
            skLineSegment(sketch, "E512", {"start": v(-3.92, 157.24) * mm, "end": v(-3.36, 157.6) * mm});
            skLineSegment(sketch, "E513", {"start": v(-4.4, 156.86) * mm, "end": v(-3.92, 157.24) * mm});
            skLineSegment(sketch, "E514", {"start": v(-4.8, 156.45) * mm, "end": v(-4.4, 156.86) * mm});
            skLineSegment(sketch, "E515", {"start": v(-5.1, 156.06) * mm, "end": v(-4.8, 156.45) * mm});
            skLineSegment(sketch, "E516", {"start": v(-5.28, 155.7) * mm, "end": v(-5.1, 156.06) * mm});
            skLineSegment(sketch, "E517", {"start": v(-5.3, 155.64) * mm, "end": v(-5.28, 155.7) * mm});
            skLineSegment(sketch, "E518", {"start": v(-5.32, 155.6) * mm, "end": v(-5.3, 155.64) * mm});
            skLineSegment(sketch, "E519", {"start": v(-5.33, 155.52) * mm, "end": v(-5.32, 155.6) * mm});
            skLineSegment(sketch, "E520", {"start": v(-5.37, 155.3) * mm, "end": v(-5.33, 155.52) * mm});
            skLineSegment(sketch, "E521", {"start": v(-5.45, 154.88) * mm, "end": v(-5.37, 155.3) * mm});
            skLineSegment(sketch, "E522", {"start": v(-5.55, 154.32) * mm, "end": v(-5.45, 154.88) * mm});
            skArc(sketch, "E523", {"start": v(-2.36, 157.19) * mm, "mid": v(-2.85, 157.4) * mm, "end": v(-3.36, 157.6) * mm});
            skLineSegment(sketch, "E524", {"start": v(-2.21, 156.54) * mm, "end": v(-2.36, 157.19) * mm});
            skLineSegment(sketch, "E525", {"start": v(-2.15, 155.92) * mm, "end": v(-2.21, 156.54) * mm});
            skLineSegment(sketch, "E526", {"start": v(-2.15, 155.36) * mm, "end": v(-2.15, 155.92) * mm});
            skLineSegment(sketch, "E527", {"start": v(-2.22, 154.87) * mm, "end": v(-2.15, 155.36) * mm});
            skLineSegment(sketch, "E528", {"start": v(-2.34, 154.5) * mm, "end": v(-2.22, 154.87) * mm});
            skLineSegment(sketch, "E529", {"start": v(-2.37, 154.43) * mm, "end": v(-2.34, 154.5) * mm});
            skLineSegment(sketch, "E530", {"start": v(-2.4, 154.38) * mm, "end": v(-2.37, 154.43) * mm});
            skLineSegment(sketch, "E531", {"start": v(-2.43, 154.32) * mm, "end": v(-2.4, 154.38) * mm});
            skLineSegment(sketch, "E532", {"start": v(-2.55, 154.14) * mm, "end": v(-2.43, 154.32) * mm});
            skLineSegment(sketch, "E533", {"start": v(-2.8, 153.78) * mm, "end": v(-2.55, 154.14) * mm});
            skLineSegment(sketch, "E534", {"start": v(-3.13, 153.31) * mm, "end": v(-2.8, 153.78) * mm});
            skArc(sketch, "E535", {"start": v(-3.13, 153.31) * mm, "mid": v(-3.26, 152.76) * mm, "end": v(-3, 152.26) * mm});
            skArc(sketch, "E536", {"start": v(-2.59, 151.84) * mm, "mid": v(-2.8, 152.06) * mm, "end": v(-3, 152.26) * mm});
            skArc(sketch, "E537", {"start": v(-2.59, 151.84) * mm, "mid": v(-2.08, 151.58) * mm, "end": v(-1.53, 151.72) * mm});
            skLineSegment(sketch, "E538", {"start": v(1.7, 152.63) * mm, "end": v(2.34, 152.49) * mm});
            skLineSegment(sketch, "E539", {"start": v(1.08, 152.7) * mm, "end": v(1.7, 152.63) * mm});
            skLineSegment(sketch, "E540", {"start": v(0.51, 152.7) * mm, "end": v(1.08, 152.7) * mm});
            skLineSegment(sketch, "E541", {"start": v(0.02, 152.62) * mm, "end": v(0.51, 152.7) * mm});
            skLineSegment(sketch, "E542", {"start": v(-0.35, 152.5) * mm, "end": v(0.02, 152.62) * mm});
            skLineSegment(sketch, "E543", {"start": v(-0.42, 152.48) * mm, "end": v(-0.35, 152.5) * mm});
            skLineSegment(sketch, "E544", {"start": v(-0.46, 152.45) * mm, "end": v(-0.42, 152.48) * mm});
            skLineSegment(sketch, "E545", {"start": v(-0.53, 152.41) * mm, "end": v(-0.46, 152.45) * mm});
            skLineSegment(sketch, "E546", {"start": v(-0.7, 152.3) * mm, "end": v(-0.53, 152.41) * mm});
            skLineSegment(sketch, "E547", {"start": v(-1.06, 152.04) * mm, "end": v(-0.7, 152.3) * mm});
            skLineSegment(sketch, "E548", {"start": v(-1.53, 151.72) * mm, "end": v(-1.06, 152.04) * mm});
            skArc(sketch, "E549", {"start": v(2.75, 151.49) * mm, "mid": v(2.56, 152) * mm, "end": v(2.34, 152.49) * mm});
            skLineSegment(sketch, "E550", {"start": v(2.4, 150.93) * mm, "end": v(2.75, 151.49) * mm});
            skLineSegment(sketch, "E551", {"start": v(2.01, 150.44) * mm, "end": v(2.4, 150.93) * mm});
            skLineSegment(sketch, "E552", {"start": v(1.6, 150.05) * mm, "end": v(2.01, 150.44) * mm});
            skLineSegment(sketch, "E553", {"start": v(1.21, 149.76) * mm, "end": v(1.6, 150.05) * mm});
            skLineSegment(sketch, "E554", {"start": v(0.86, 149.57) * mm, "end": v(1.21, 149.76) * mm});
            skLineSegment(sketch, "E555", {"start": v(0.8, 149.55) * mm, "end": v(0.86, 149.57) * mm});
            skLineSegment(sketch, "E556", {"start": v(0.75, 149.53) * mm, "end": v(0.8, 149.55) * mm});
            skLineSegment(sketch, "E557", {"start": v(0.67, 149.51) * mm, "end": v(0.75, 149.53) * mm});
            skLineSegment(sketch, "E558", {"start": v(0.46, 149.47) * mm, "end": v(0.67, 149.51) * mm});
            skLineSegment(sketch, "E559", {"start": v(0.03, 149.4) * mm, "end": v(0.46, 149.47) * mm});
            skLineSegment(sketch, "E560", {"start": v(-0.53, 149.3) * mm, "end": v(0.03, 149.4) * mm});
            skArc(sketch, "E561", {"start": v(-0.53, 149.3) * mm, "mid": v(-1.02, 149) * mm, "end": v(-1.19, 148.46) * mm});
            skArc(sketch, "E562", {"start": v(-1.19, 147.87) * mm, "mid": v(-1.18, 148.17) * mm, "end": v(-1.19, 148.46) * mm});
            skArc(sketch, "E563", {"start": v(-1.19, 147.87) * mm, "mid": v(-1.02, 147.33) * mm, "end": v(-0.53, 147.04) * mm});
            skLineSegment(sketch, "E564", {"start": v(2.4, 145.4) * mm, "end": v(2.75, 144.84) * mm});
            skLineSegment(sketch, "E565", {"start": v(2.01, 145.89) * mm, "end": v(2.4, 145.4) * mm});
            skLineSegment(sketch, "E566", {"start": v(1.6, 146.28) * mm, "end": v(2.01, 145.89) * mm});
            skLineSegment(sketch, "E567", {"start": v(1.21, 146.58) * mm, "end": v(1.6, 146.28) * mm});
            skLineSegment(sketch, "E568", {"start": v(0.86, 146.76) * mm, "end": v(1.21, 146.58) * mm});
            skLineSegment(sketch, "E569", {"start": v(0.8, 146.79) * mm, "end": v(0.86, 146.76) * mm});
            skLineSegment(sketch, "E570", {"start": v(0.75, 146.8) * mm, "end": v(0.8, 146.79) * mm});
            skLineSegment(sketch, "E571", {"start": v(0.67, 146.82) * mm, "end": v(0.75, 146.8) * mm});
            skLineSegment(sketch, "E572", {"start": v(0.46, 146.86) * mm, "end": v(0.67, 146.82) * mm});
            skLineSegment(sketch, "E573", {"start": v(0.03, 146.94) * mm, "end": v(0.46, 146.86) * mm});
            skLineSegment(sketch, "E574", {"start": v(-0.53, 147.04) * mm, "end": v(0.03, 146.94) * mm});
            skArc(sketch, "E575", {"start": v(2.34, 143.85) * mm, "mid": v(2.56, 144.34) * mm, "end": v(2.75, 144.84) * mm});
            skLineSegment(sketch, "E576", {"start": v(1.7, 143.7) * mm, "end": v(2.34, 143.85) * mm});
            skLineSegment(sketch, "E577", {"start": v(1.08, 143.63) * mm, "end": v(1.7, 143.7) * mm});
            skLineSegment(sketch, "E578", {"start": v(0.51, 143.64) * mm, "end": v(1.08, 143.63) * mm});
            skLineSegment(sketch, "E579", {"start": v(0.02, 143.7) * mm, "end": v(0.51, 143.64) * mm});
            skLineSegment(sketch, "E580", {"start": v(-0.35, 143.83) * mm, "end": v(0.02, 143.7) * mm});
            skLineSegment(sketch, "E581", {"start": v(-0.42, 143.86) * mm, "end": v(-0.35, 143.83) * mm});
            skLineSegment(sketch, "E582", {"start": v(-0.46, 143.88) * mm, "end": v(-0.42, 143.86) * mm});
            skLineSegment(sketch, "E583", {"start": v(-0.53, 143.92) * mm, "end": v(-0.46, 143.88) * mm});
            skLineSegment(sketch, "E584", {"start": v(-0.7, 144.04) * mm, "end": v(-0.53, 143.92) * mm});
            skLineSegment(sketch, "E585", {"start": v(-1.06, 144.29) * mm, "end": v(-0.7, 144.04) * mm});
            skLineSegment(sketch, "E586", {"start": v(-1.53, 144.61) * mm, "end": v(-1.06, 144.29) * mm});
            skArc(sketch, "E587", {"start": v(-1.53, 144.61) * mm, "mid": v(-2.08, 144.75) * mm, "end": v(-2.59, 144.49) * mm});
            skLineSegment(sketch, "E588", {"start": v(32.07, 158.31) * mm, "end": v(32.56, 158.7) * mm});
            skLineSegment(sketch, "E589", {"start": v(31.68, 157.91) * mm, "end": v(32.07, 158.31) * mm});
            skLineSegment(sketch, "E590", {"start": v(31.38, 157.52) * mm, "end": v(31.68, 157.91) * mm});
            skLineSegment(sketch, "E591", {"start": v(31.2, 157.16) * mm, "end": v(31.38, 157.52) * mm});
            skLineSegment(sketch, "E592", {"start": v(31.18, 157.1) * mm, "end": v(31.2, 157.16) * mm});
            skLineSegment(sketch, "E593", {"start": v(31.16, 157.05) * mm, "end": v(31.18, 157.1) * mm});
            skLineSegment(sketch, "E594", {"start": v(31.14, 156.98) * mm, "end": v(31.16, 157.05) * mm});
            skLineSegment(sketch, "E595", {"start": v(31.1, 156.77) * mm, "end": v(31.14, 156.98) * mm});
            skLineSegment(sketch, "E596", {"start": v(31.02, 156.34) * mm, "end": v(31.1, 156.77) * mm});
            skLineSegment(sketch, "E597", {"start": v(30.92, 155.78) * mm, "end": v(31.02, 156.34) * mm});
            skArc(sketch, "E598", {"start": v(34.12, 158.64) * mm, "mid": v(33.62, 158.86) * mm, "end": v(33.12, 159.06) * mm});
            skLineSegment(sketch, "E599", {"start": v(34.26, 158) * mm, "end": v(34.12, 158.64) * mm});
            skLineSegment(sketch, "E600", {"start": v(34.33, 157.38) * mm, "end": v(34.26, 158) * mm});
            skLineSegment(sketch, "E601", {"start": v(34.32, 156.82) * mm, "end": v(34.33, 157.38) * mm});
            skLineSegment(sketch, "E602", {"start": v(34.25, 156.33) * mm, "end": v(34.32, 156.82) * mm});
            skLineSegment(sketch, "E603", {"start": v(34.13, 155.95) * mm, "end": v(34.25, 156.33) * mm});
            skLineSegment(sketch, "E604", {"start": v(34.1, 155.89) * mm, "end": v(34.13, 155.95) * mm});
            skLineSegment(sketch, "E605", {"start": v(34.08, 155.84) * mm, "end": v(34.1, 155.89) * mm});
            skLineSegment(sketch, "E606", {"start": v(34.04, 155.78) * mm, "end": v(34.08, 155.84) * mm});
            skLineSegment(sketch, "E607", {"start": v(33.92, 155.6) * mm, "end": v(34.04, 155.78) * mm});
            skLineSegment(sketch, "E608", {"start": v(33.67, 155.24) * mm, "end": v(33.92, 155.6) * mm});
            skLineSegment(sketch, "E609", {"start": v(33.35, 154.77) * mm, "end": v(33.67, 155.24) * mm});
            skArc(sketch, "E610", {"start": v(33.35, 154.77) * mm, "mid": v(33.21, 154.22) * mm, "end": v(33.47, 153.71) * mm});
            skArc(sketch, "E611", {"start": v(33.89, 153.3) * mm, "mid": v(33.68, 153.51) * mm, "end": v(33.47, 153.71) * mm});
            skArc(sketch, "E612", {"start": v(33.89, 153.3) * mm, "mid": v(34.4, 153.04) * mm, "end": v(34.94, 153.18) * mm});
            skLineSegment(sketch, "E613", {"start": v(38.17, 154.1) * mm, "end": v(38.81, 153.94) * mm});
            skLineSegment(sketch, "E614", {"start": v(37.55, 154.16) * mm, "end": v(38.17, 154.1) * mm});
            skLineSegment(sketch, "E615", {"start": v(36.99, 154.15) * mm, "end": v(37.55, 154.16) * mm});
            skLineSegment(sketch, "E616", {"start": v(36.5, 154.08) * mm, "end": v(36.99, 154.15) * mm});
            skLineSegment(sketch, "E617", {"start": v(36.12, 153.96) * mm, "end": v(36.5, 154.08) * mm});
            skLineSegment(sketch, "E618", {"start": v(36.06, 153.94) * mm, "end": v(36.12, 153.96) * mm});
            skLineSegment(sketch, "E619", {"start": v(36.01, 153.91) * mm, "end": v(36.06, 153.94) * mm});
            skLineSegment(sketch, "E620", {"start": v(35.95, 153.87) * mm, "end": v(36.01, 153.91) * mm});
            skLineSegment(sketch, "E621", {"start": v(35.77, 153.75) * mm, "end": v(35.95, 153.87) * mm});
            skLineSegment(sketch, "E622", {"start": v(35.41, 153.5) * mm, "end": v(35.77, 153.75) * mm});
            skLineSegment(sketch, "E623", {"start": v(34.94, 153.18) * mm, "end": v(35.41, 153.5) * mm});
            skArc(sketch, "E624", {"start": v(39.23, 152.95) * mm, "mid": v(39.03, 153.45) * mm, "end": v(38.81, 153.94) * mm});
            skLineSegment(sketch, "E625", {"start": v(38.87, 152.38) * mm, "end": v(39.23, 152.95) * mm});
            skLineSegment(sketch, "E626", {"start": v(38.49, 151.9) * mm, "end": v(38.87, 152.38) * mm});
            skLineSegment(sketch, "E627", {"start": v(38.08, 151.5) * mm, "end": v(38.49, 151.9) * mm});
            skLineSegment(sketch, "E628", {"start": v(37.69, 151.21) * mm, "end": v(38.08, 151.5) * mm});
            skLineSegment(sketch, "E629", {"start": v(37.34, 151.03) * mm, "end": v(37.69, 151.21) * mm});
            skLineSegment(sketch, "E630", {"start": v(37.27, 151) * mm, "end": v(37.34, 151.03) * mm});
            skLineSegment(sketch, "E631", {"start": v(37.22, 150.99) * mm, "end": v(37.27, 151) * mm});
            skLineSegment(sketch, "E632", {"start": v(37.15, 150.97) * mm, "end": v(37.22, 150.99) * mm});
            skLineSegment(sketch, "E633", {"start": v(36.94, 150.93) * mm, "end": v(37.15, 150.97) * mm});
            skLineSegment(sketch, "E634", {"start": v(36.5, 150.85) * mm, "end": v(36.94, 150.93) * mm});
            skLineSegment(sketch, "E635", {"start": v(35.95, 150.75) * mm, "end": v(36.5, 150.85) * mm});
            skArc(sketch, "E636", {"start": v(35.95, 150.75) * mm, "mid": v(35.46, 150.46) * mm, "end": v(35.29, 149.92) * mm});
            skArc(sketch, "E637", {"start": v(35.29, 149.33) * mm, "mid": v(35.3, 149.62) * mm, "end": v(35.29, 149.92) * mm});
            skArc(sketch, "E638", {"start": v(35.29, 149.33) * mm, "mid": v(35.46, 148.8) * mm, "end": v(35.95, 148.5) * mm});
            skLineSegment(sketch, "E639", {"start": v(38.87, 146.86) * mm, "end": v(39.23, 146.3) * mm});
            skLineSegment(sketch, "E640", {"start": v(38.49, 147.35) * mm, "end": v(38.87, 146.86) * mm});
            skLineSegment(sketch, "E641", {"start": v(38.08, 147.74) * mm, "end": v(38.49, 147.35) * mm});
            skLineSegment(sketch, "E642", {"start": v(37.69, 148.04) * mm, "end": v(38.08, 147.74) * mm});
            skLineSegment(sketch, "E643", {"start": v(37.34, 148.22) * mm, "end": v(37.69, 148.04) * mm});
            skLineSegment(sketch, "E644", {"start": v(37.27, 148.24) * mm, "end": v(37.34, 148.22) * mm});
            skLineSegment(sketch, "E645", {"start": v(37.22, 148.26) * mm, "end": v(37.27, 148.24) * mm});
            skLineSegment(sketch, "E646", {"start": v(37.15, 148.28) * mm, "end": v(37.22, 148.26) * mm});
            skLineSegment(sketch, "E647", {"start": v(36.94, 148.32) * mm, "end": v(37.15, 148.28) * mm});
            skLineSegment(sketch, "E648", {"start": v(36.5, 148.4) * mm, "end": v(36.94, 148.32) * mm});
            skLineSegment(sketch, "E649", {"start": v(35.95, 148.5) * mm, "end": v(36.5, 148.4) * mm});
            skArc(sketch, "E650", {"start": v(38.81, 145.3) * mm, "mid": v(39.03, 145.8) * mm, "end": v(39.23, 146.3) * mm});
            skLineSegment(sketch, "E651", {"start": v(38.17, 145.16) * mm, "end": v(38.81, 145.3) * mm});
            skLineSegment(sketch, "E652", {"start": v(37.55, 145.1) * mm, "end": v(38.17, 145.16) * mm});
            skLineSegment(sketch, "E653", {"start": v(36.99, 145.1) * mm, "end": v(37.55, 145.1) * mm});
            skLineSegment(sketch, "E654", {"start": v(36.5, 145.17) * mm, "end": v(36.99, 145.1) * mm});
            skLineSegment(sketch, "E655", {"start": v(36.12, 145.29) * mm, "end": v(36.5, 145.17) * mm});
            skLineSegment(sketch, "E656", {"start": v(36.06, 145.31) * mm, "end": v(36.12, 145.29) * mm});
            skLineSegment(sketch, "E657", {"start": v(36.01, 145.34) * mm, "end": v(36.06, 145.31) * mm});
            skLineSegment(sketch, "E658", {"start": v(35.95, 145.38) * mm, "end": v(36.01, 145.34) * mm});
            skLineSegment(sketch, "E659", {"start": v(35.77, 145.5) * mm, "end": v(35.95, 145.38) * mm});
            skLineSegment(sketch, "E660", {"start": v(35.41, 145.75) * mm, "end": v(35.77, 145.5) * mm});
            skLineSegment(sketch, "E661", {"start": v(34.94, 146.07) * mm, "end": v(35.41, 145.75) * mm});
            skArc(sketch, "E662", {"start": v(34.94, 146.07) * mm, "mid": v(34.4, 146.2) * mm, "end": v(33.89, 145.95) * mm});
            skCircle(sketch, "E663", {"center": v(-6.68, 148.17) * mm, "radius": 3.1 * mm});
            skLineSegment(sketch, "E664", {"start": v(-6.75, 90.69) * mm, "end": v(-6.74, 90.78) * mm});
            skLineSegment(sketch, "E665", {"start": v(-6.79, 90.5) * mm, "end": v(-6.75, 90.69) * mm});
            skLineSegment(sketch, "E666", {"start": v(-6.85, 90.12) * mm, "end": v(-6.79, 90.5) * mm});
            skLineSegment(sketch, "E667", {"start": v(-6.93, 89.65) * mm, "end": v(-6.85, 90.12) * mm});
            skArc(sketch, "E668", {"start": v(-6.93, 89.65) * mm, "mid": v(-6.82, 89.07) * mm, "end": v(-6.34, 88.71) * mm});
            skArc(sketch, "E669", {"start": v(75.4, 111.74) * mm, "mid": v(75.7, 111.78) * mm, "end": v(76, 111.85) * mm});
            skArc(sketch, "E670", {"start": v(75.4, 111.74) * mm, "mid": v(74.88, 111.46) * mm, "end": v(74.68, 110.91) * mm});
            skLineSegment(sketch, "E671", {"start": v(73.69, 107.75) * mm, "end": v(73.22, 107.27) * mm});
            skLineSegment(sketch, "E672", {"start": v(74.07, 108.25) * mm, "end": v(73.69, 107.75) * mm});
            skLineSegment(sketch, "E673", {"start": v(74.37, 108.73) * mm, "end": v(74.07, 108.25) * mm});
            skLineSegment(sketch, "E674", {"start": v(74.57, 109.2) * mm, "end": v(74.37, 108.73) * mm});
            skLineSegment(sketch, "E675", {"start": v(74.68, 109.58) * mm, "end": v(74.57, 109.2) * mm});
            skLineSegment(sketch, "E676", {"start": v(74.7, 109.7) * mm, "end": v(74.68, 109.58) * mm});
            skLineSegment(sketch, "E677", {"start": v(74.7, 109.78) * mm, "end": v(74.7, 109.7) * mm});
            skLineSegment(sketch, "E678", {"start": v(74.7, 109.98) * mm, "end": v(74.7, 109.78) * mm});
            skLineSegment(sketch, "E679", {"start": v(74.69, 110.39) * mm, "end": v(74.7, 109.98) * mm});
            skLineSegment(sketch, "E680", {"start": v(74.68, 110.91) * mm, "end": v(74.69, 110.39) * mm});
            skArc(sketch, "E681", {"start": v(72.1, 107.47) * mm, "mid": v(72.66, 107.35) * mm, "end": v(73.22, 107.27) * mm});
            skLineSegment(sketch, "E682", {"start": v(71.83, 108.08) * mm, "end": v(72.1, 107.47) * mm});
            skLineSegment(sketch, "E683", {"start": v(71.64, 108.68) * mm, "end": v(71.83, 108.08) * mm});
            skLineSegment(sketch, "E684", {"start": v(71.53, 109.24) * mm, "end": v(71.64, 108.68) * mm});
            skLineSegment(sketch, "E685", {"start": v(71.5, 109.73) * mm, "end": v(71.53, 109.24) * mm});
            skLineSegment(sketch, "E686", {"start": v(71.52, 110.13) * mm, "end": v(71.5, 109.73) * mm});
            skLineSegment(sketch, "E687", {"start": v(71.55, 110.25) * mm, "end": v(71.52, 110.13) * mm});
            skLineSegment(sketch, "E688", {"start": v(71.57, 110.33) * mm, "end": v(71.55, 110.25) * mm});
            skLineSegment(sketch, "E689", {"start": v(71.65, 110.52) * mm, "end": v(71.57, 110.33) * mm});
            skLineSegment(sketch, "E690", {"start": v(71.8, 110.9) * mm, "end": v(71.65, 110.52) * mm});
            skLineSegment(sketch, "E691", {"start": v(71.98, 111.4) * mm, "end": v(71.8, 110.9) * mm});
            skArc(sketch, "E692", {"start": v(71.98, 111.4) * mm, "mid": v(71.98, 111.97) * mm, "end": v(71.6, 112.4) * mm});
            skArc(sketch, "E693", {"start": v(71.06, 112.72) * mm, "mid": v(71.32, 112.56) * mm, "end": v(71.6, 112.4) * mm});
            skArc(sketch, "E694", {"start": v(71.06, 112.72) * mm, "mid": v(70.48, 112.84) * mm, "end": v(69.98, 112.54) * mm});
            skLineSegment(sketch, "E695", {"start": v(67.19, 110.76) * mm, "end": v(66.52, 110.7) * mm});
            skLineSegment(sketch, "E696", {"start": v(67.8, 110.9) * mm, "end": v(67.19, 110.76) * mm});
            skLineSegment(sketch, "E697", {"start": v(68.34, 111.08) * mm, "end": v(67.8, 110.9) * mm});
            skLineSegment(sketch, "E698", {"start": v(68.79, 111.3) * mm, "end": v(68.34, 111.08) * mm});
            skLineSegment(sketch, "E699", {"start": v(69.12, 111.52) * mm, "end": v(68.79, 111.3) * mm});
            skLineSegment(sketch, "E700", {"start": v(69.2, 111.6) * mm, "end": v(69.12, 111.52) * mm});
            skLineSegment(sketch, "E701", {"start": v(69.26, 111.66) * mm, "end": v(69.2, 111.6) * mm});
            skLineSegment(sketch, "E702", {"start": v(69.4, 111.82) * mm, "end": v(69.26, 111.66) * mm});
            skLineSegment(sketch, "E703", {"start": v(69.65, 112.14) * mm, "end": v(69.4, 111.82) * mm});
            skLineSegment(sketch, "E704", {"start": v(69.98, 112.54) * mm, "end": v(69.65, 112.14) * mm});
            skArc(sketch, "E705", {"start": v(65.8, 111.56) * mm, "mid": v(66.14, 111.12) * mm, "end": v(66.52, 110.7) * mm});
            skLineSegment(sketch, "E706", {"start": v(65.98, 112.2) * mm, "end": v(65.8, 111.56) * mm});
            skLineSegment(sketch, "E707", {"start": v(66.21, 112.78) * mm, "end": v(65.98, 112.2) * mm});
            skLineSegment(sketch, "E708", {"start": v(66.49, 113.29) * mm, "end": v(66.21, 112.78) * mm});
            skLineSegment(sketch, "E709", {"start": v(66.78, 113.7) * mm, "end": v(66.49, 113.29) * mm});
            skLineSegment(sketch, "E710", {"start": v(67.06, 113.98) * mm, "end": v(66.78, 113.7) * mm});
            skLineSegment(sketch, "E711", {"start": v(67.16, 114.05) * mm, "end": v(67.06, 113.98) * mm});
            skLineSegment(sketch, "E712", {"start": v(67.22, 114.1) * mm, "end": v(67.16, 114.05) * mm});
            skLineSegment(sketch, "E713", {"start": v(67.4, 114.2) * mm, "end": v(67.22, 114.1) * mm});
            skLineSegment(sketch, "E714", {"start": v(67.76, 114.39) * mm, "end": v(67.4, 114.2) * mm});
            skLineSegment(sketch, "E715", {"start": v(68.22, 114.65) * mm, "end": v(67.76, 114.39) * mm});
            skArc(sketch, "E716", {"start": v(68.22, 114.65) * mm, "mid": v(68.6, 115.1) * mm, "end": v(68.57, 115.68) * mm});
            skArc(sketch, "E717", {"start": v(68.36, 116.26) * mm, "mid": v(68.46, 115.96) * mm, "end": v(68.57, 115.68) * mm});
            skArc(sketch, "E718", {"start": v(68.36, 116.26) * mm, "mid": v(68, 116.71) * mm, "end": v(67.43, 116.81) * mm});
            skLineSegment(sketch, "E719", {"start": v(64.14, 117.24) * mm, "end": v(63.58, 117.62) * mm});
            skLineSegment(sketch, "E720", {"start": v(64.7, 116.95) * mm, "end": v(64.14, 117.24) * mm});
            skLineSegment(sketch, "E721", {"start": v(65.23, 116.74) * mm, "end": v(64.7, 116.95) * mm});
            skLineSegment(sketch, "E722", {"start": v(65.71, 116.62) * mm, "end": v(65.23, 116.74) * mm});
            skLineSegment(sketch, "E723", {"start": v(66.11, 116.58) * mm, "end": v(65.71, 116.62) * mm});
            skLineSegment(sketch, "E724", {"start": v(66.23, 116.59) * mm, "end": v(66.11, 116.58) * mm});
            skLineSegment(sketch, "E725", {"start": v(66.3, 116.6) * mm, "end": v(66.23, 116.59) * mm});
            skLineSegment(sketch, "E726", {"start": v(66.5, 116.64) * mm, "end": v(66.3, 116.6) * mm});
            skLineSegment(sketch, "E727", {"start": v(66.91, 116.71) * mm, "end": v(66.5, 116.64) * mm});
            skLineSegment(sketch, "E728", {"start": v(67.43, 116.81) * mm, "end": v(66.91, 116.71) * mm});
            skArc(sketch, "E729", {"start": v(63.58, 118.75) * mm, "mid": v(63.57, 118.19) * mm, "end": v(63.58, 117.62) * mm});
            skLineSegment(sketch, "E730", {"start": v(64.14, 119.13) * mm, "end": v(63.58, 118.75) * mm});
            skLineSegment(sketch, "E731", {"start": v(64.7, 119.42) * mm, "end": v(64.14, 119.13) * mm});
            skLineSegment(sketch, "E732", {"start": v(65.23, 119.63) * mm, "end": v(64.7, 119.42) * mm});
            skLineSegment(sketch, "E733", {"start": v(65.71, 119.75) * mm, "end": v(65.23, 119.63) * mm});
            skLineSegment(sketch, "E734", {"start": v(66.11, 119.79) * mm, "end": v(65.71, 119.75) * mm});
            skLineSegment(sketch, "E735", {"start": v(66.23, 119.78) * mm, "end": v(66.11, 119.79) * mm});
            skLineSegment(sketch, "E736", {"start": v(66.3, 119.77) * mm, "end": v(66.23, 119.78) * mm});
            skLineSegment(sketch, "E737", {"start": v(66.5, 119.73) * mm, "end": v(66.3, 119.77) * mm});
            skLineSegment(sketch, "E738", {"start": v(27.69, 112.96) * mm, "end": v(27.24, 112.74) * mm});
            skLineSegment(sketch, "E739", {"start": v(22.6, 145.1) * mm, "end": v(22.04, 145.1) * mm});
            skLineSegment(sketch, "E740", {"start": v(28.02, 113.18) * mm, "end": v(27.69, 112.96) * mm});
            skLineSegment(sketch, "E741", {"start": v(23.1, 145.17) * mm, "end": v(22.6, 145.1) * mm});
            skLineSegment(sketch, "E742", {"start": v(28.1, 113.27) * mm, "end": v(28.02, 113.18) * mm});
            skLineSegment(sketch, "E743", {"start": v(23.47, 145.29) * mm, "end": v(23.1, 145.17) * mm});
            skLineSegment(sketch, "E744", {"start": v(28.16, 113.33) * mm, "end": v(28.1, 113.27) * mm});
            skLineSegment(sketch, "E745", {"start": v(23.53, 145.31) * mm, "end": v(23.47, 145.29) * mm});
            skLineSegment(sketch, "E746", {"start": v(28.29, 113.48) * mm, "end": v(28.16, 113.33) * mm});
            skLineSegment(sketch, "E747", {"start": v(23.58, 145.34) * mm, "end": v(23.53, 145.31) * mm});
            skLineSegment(sketch, "E748", {"start": v(28.55, 113.8) * mm, "end": v(28.29, 113.48) * mm});
            skLineSegment(sketch, "E749", {"start": v(23.64, 145.38) * mm, "end": v(23.58, 145.34) * mm});
            skLineSegment(sketch, "E750", {"start": v(28.88, 114.2) * mm, "end": v(28.55, 113.8) * mm});
            skLineSegment(sketch, "E751", {"start": v(23.82, 145.5) * mm, "end": v(23.64, 145.38) * mm});
            skArc(sketch, "E752", {"start": v(24.7, 113.22) * mm, "mid": v(25.04, 112.78) * mm, "end": v(25.42, 112.35) * mm});
            skLineSegment(sketch, "E753", {"start": v(24.18, 145.75) * mm, "end": v(23.82, 145.5) * mm});
            skLineSegment(sketch, "E754", {"start": v(24.88, 113.87) * mm, "end": v(24.7, 113.22) * mm});
            skLineSegment(sketch, "E755", {"start": v(24.65, 146.07) * mm, "end": v(24.18, 145.75) * mm});
            skLineSegment(sketch, "E756", {"start": v(25.11, 114.45) * mm, "end": v(24.88, 113.87) * mm});
            skArc(sketch, "E757", {"start": v(20.36, 146.3) * mm, "mid": v(20.56, 145.8) * mm, "end": v(20.78, 145.3) * mm});
            skLineSegment(sketch, "E758", {"start": v(25.38, 114.95) * mm, "end": v(25.11, 114.45) * mm});
            skLineSegment(sketch, "E759", {"start": v(20.72, 146.86) * mm, "end": v(20.36, 146.3) * mm});
            skLineSegment(sketch, "E760", {"start": v(25.68, 115.35) * mm, "end": v(25.38, 114.95) * mm});
            skLineSegment(sketch, "E761", {"start": v(21.1, 147.35) * mm, "end": v(20.72, 146.86) * mm});
            skArc(sketch, "E762", {"start": v(27.12, 116.3) * mm, "mid": v(27.5, 116.76) * mm, "end": v(27.47, 117.34) * mm});
            skLineSegment(sketch, "E763", {"start": v(22.65, 148.32) * mm, "end": v(22.44, 148.28) * mm});
            skArc(sketch, "E764", {"start": v(27.26, 117.92) * mm, "mid": v(27.36, 117.63) * mm, "end": v(27.47, 117.34) * mm});
            skLineSegment(sketch, "E765", {"start": v(23.08, 148.4) * mm, "end": v(22.65, 148.32) * mm});
            skArc(sketch, "E766", {"start": v(27.26, 117.92) * mm, "mid": v(26.9, 118.38) * mm, "end": v(26.33, 118.48) * mm});
            skLineSegment(sketch, "E767", {"start": v(23.64, 148.5) * mm, "end": v(23.08, 148.4) * mm});
            skLineSegment(sketch, "E768", {"start": v(23.04, 118.9) * mm, "end": v(22.48, 119.28) * mm});
            skArc(sketch, "E769", {"start": v(23.64, 148.5) * mm, "mid": v(24.13, 148.8) * mm, "end": v(24.3, 149.33) * mm});
            skLineSegment(sketch, "E770", {"start": v(27.12, 116.3) * mm, "end": v(26.66, 116.05) * mm});
            skLineSegment(sketch, "E771", {"start": v(22.44, 148.28) * mm, "end": v(22.37, 148.26) * mm});
            skLineSegment(sketch, "E772", {"start": v(26.66, 116.05) * mm, "end": v(26.3, 115.85) * mm});
            skLineSegment(sketch, "E773", {"start": v(22.37, 148.26) * mm, "end": v(22.32, 148.24) * mm});
            skLineSegment(sketch, "E774", {"start": v(26.3, 115.85) * mm, "end": v(26.12, 115.75) * mm});
            skLineSegment(sketch, "E775", {"start": v(22.32, 148.24) * mm, "end": v(22.25, 148.22) * mm});
            skLineSegment(sketch, "E776", {"start": v(26.12, 115.75) * mm, "end": v(26.05, 115.71) * mm});
            skLineSegment(sketch, "E777", {"start": v(22.25, 148.22) * mm, "end": v(21.9, 148.04) * mm});
            skLineSegment(sketch, "E778", {"start": v(26.05, 115.71) * mm, "end": v(25.96, 115.64) * mm});
            skLineSegment(sketch, "E779", {"start": v(21.9, 148.04) * mm, "end": v(21.5, 147.74) * mm});
            skLineSegment(sketch, "E780", {"start": v(25.96, 115.64) * mm, "end": v(25.68, 115.35) * mm});
            skLineSegment(sketch, "E781", {"start": v(21.5, 147.74) * mm, "end": v(21.1, 147.35) * mm});
            skLineSegment(sketch, "E782", {"start": v(27.24, 112.74) * mm, "end": v(26.7, 112.56) * mm});
            skLineSegment(sketch, "E783", {"start": v(22.04, 145.1) * mm, "end": v(21.42, 145.16) * mm});
            skLineSegment(sketch, "E784", {"start": v(26.7, 112.56) * mm, "end": v(26.09, 112.42) * mm});
            skLineSegment(sketch, "E785", {"start": v(21.42, 145.16) * mm, "end": v(20.78, 145.3) * mm});
            skLineSegment(sketch, "E786", {"start": v(26.09, 112.42) * mm, "end": v(25.42, 112.35) * mm});
            skArc(sketch, "E787", {"start": v(25.7, 145.95) * mm, "mid": v(25.2, 146.2) * mm, "end": v(24.65, 146.07) * mm});
            skArc(sketch, "E788", {"start": v(29.96, 114.38) * mm, "mid": v(29.38, 114.5) * mm, "end": v(28.88, 114.2) * mm});
            skArc(sketch, "E789", {"start": v(25.7, 145.95) * mm, "mid": v(25.9, 145.74) * mm, "end": v(26.12, 145.53) * mm});
            skArc(sketch, "E790", {"start": v(29.96, 114.38) * mm, "mid": v(30.22, 114.22) * mm, "end": v(30.49, 114.07) * mm});
            skArc(sketch, "E791", {"start": v(26.24, 144.48) * mm, "mid": v(26.38, 145.03) * mm, "end": v(26.12, 145.53) * mm});
            skArc(sketch, "E792", {"start": v(30.88, 113.05) * mm, "mid": v(30.88, 113.64) * mm, "end": v(30.49, 114.07) * mm});
            skLineSegment(sketch, "E793", {"start": v(26.24, 144.48) * mm, "end": v(25.92, 144) * mm});
            skLineSegment(sketch, "E794", {"start": v(30.88, 113.05) * mm, "end": v(30.7, 112.56) * mm});
            skLineSegment(sketch, "E795", {"start": v(25.92, 144) * mm, "end": v(25.67, 143.65) * mm});
            skLineSegment(sketch, "E796", {"start": v(30.7, 112.56) * mm, "end": v(30.55, 112.18) * mm});
            skLineSegment(sketch, "E797", {"start": v(25.67, 143.65) * mm, "end": v(25.55, 143.47) * mm});
            skLineSegment(sketch, "E798", {"start": v(30.55, 112.18) * mm, "end": v(30.47, 111.99) * mm});
            skLineSegment(sketch, "E799", {"start": v(25.55, 143.47) * mm, "end": v(25.5, 143.4) * mm});
            skLineSegment(sketch, "E800", {"start": v(30.47, 111.99) * mm, "end": v(30.45, 111.91) * mm});
            skLineSegment(sketch, "E801", {"start": v(25.5, 143.4) * mm, "end": v(25.48, 143.36) * mm});
            skLineSegment(sketch, "E802", {"start": v(30.45, 111.91) * mm, "end": v(30.42, 111.8) * mm});
            skLineSegment(sketch, "E803", {"start": v(25.48, 143.36) * mm, "end": v(25.46, 143.3) * mm});
            skLineSegment(sketch, "E804", {"start": v(30.42, 111.8) * mm, "end": v(30.4, 111.4) * mm});
            skLineSegment(sketch, "E805", {"start": v(25.46, 143.3) * mm, "end": v(25.34, 142.92) * mm});
            skLineSegment(sketch, "E806", {"start": v(30.4, 111.4) * mm, "end": v(30.43, 110.9) * mm});
            skLineSegment(sketch, "E807", {"start": v(25.34, 142.92) * mm, "end": v(25.27, 142.43) * mm});
            skLineSegment(sketch, "E808", {"start": v(30.43, 110.9) * mm, "end": v(30.54, 110.34) * mm});
            skLineSegment(sketch, "E809", {"start": v(25.27, 142.43) * mm, "end": v(25.26, 141.87) * mm});
            skLineSegment(sketch, "E810", {"start": v(30.54, 110.34) * mm, "end": v(30.73, 109.74) * mm});
            skLineSegment(sketch, "E811", {"start": v(25.26, 141.87) * mm, "end": v(25.33, 141.25) * mm});
            skLineSegment(sketch, "E812", {"start": v(30.73, 109.74) * mm, "end": v(31, 109.13) * mm});
            skLineSegment(sketch, "E813", {"start": v(25.33, 141.25) * mm, "end": v(25.47, 140.6) * mm});
            skArc(sketch, "E814", {"start": v(31, 109.13) * mm, "mid": v(31.56, 109.02) * mm, "end": v(32.12, 108.93) * mm});
            skArc(sketch, "E815", {"start": v(25.47, 140.6) * mm, "mid": v(25.97, 140.39) * mm, "end": v(26.47, 140.2) * mm});
            skLineSegment(sketch, "E816", {"start": v(33.58, 112.58) * mm, "end": v(33.59, 112.05) * mm});
            skLineSegment(sketch, "E817", {"start": v(28.67, 143.47) * mm, "end": v(28.57, 142.91) * mm});
            skLineSegment(sketch, "E818", {"start": v(69.26, 124.7) * mm, "end": v(69.2, 124.77) * mm});
            skLineSegment(sketch, "E819", {"start": v(69.2, 124.77) * mm, "end": v(69.12, 124.85) * mm});
            skLineSegment(sketch, "E820", {"start": v(69.12, 124.85) * mm, "end": v(68.79, 125.08) * mm});
            skLineSegment(sketch, "E821", {"start": v(68.79, 125.08) * mm, "end": v(68.34, 125.3) * mm});
            skLineSegment(sketch, "E822", {"start": v(68.34, 125.3) * mm, "end": v(67.8, 125.48) * mm});
            skLineSegment(sketch, "E823", {"start": v(67.8, 125.48) * mm, "end": v(67.19, 125.6) * mm});
            skLineSegment(sketch, "E824", {"start": v(67.19, 125.6) * mm, "end": v(66.52, 125.68) * mm});
            skArc(sketch, "E825", {"start": v(66.52, 125.68) * mm, "mid": v(66.14, 125.26) * mm, "end": v(65.8, 124.81) * mm});
            skLineSegment(sketch, "E826", {"start": v(68.22, 121.73) * mm, "end": v(67.76, 121.98) * mm});
            skLineSegment(sketch, "E827", {"start": v(67.76, 121.98) * mm, "end": v(67.4, 122.18) * mm});
            skLineSegment(sketch, "E828", {"start": v(67.4, 122.18) * mm, "end": v(67.22, 122.28) * mm});
            skLineSegment(sketch, "E829", {"start": v(67.22, 122.28) * mm, "end": v(67.16, 122.32) * mm});
            skLineSegment(sketch, "E830", {"start": v(67.16, 122.32) * mm, "end": v(67.06, 122.4) * mm});
            skLineSegment(sketch, "E831", {"start": v(67.06, 122.4) * mm, "end": v(66.78, 122.68) * mm});
            skLineSegment(sketch, "E832", {"start": v(66.78, 122.68) * mm, "end": v(66.49, 123.09) * mm});
            skLineSegment(sketch, "E833", {"start": v(66.49, 123.09) * mm, "end": v(66.21, 123.59) * mm});
            skLineSegment(sketch, "E834", {"start": v(66.21, 123.59) * mm, "end": v(65.98, 124.17) * mm});
            skLineSegment(sketch, "E835", {"start": v(65.98, 124.17) * mm, "end": v(65.8, 124.81) * mm});
            skArc(sketch, "E836", {"start": v(68.57, 120.7) * mm, "mid": v(68.6, 121.28) * mm, "end": v(68.22, 121.73) * mm});
            skArc(sketch, "E837", {"start": v(68.57, 120.7) * mm, "mid": v(68.46, 120.4) * mm, "end": v(68.36, 120.12) * mm});
            skArc(sketch, "E838", {"start": v(67.43, 119.56) * mm, "mid": v(68, 119.66) * mm, "end": v(68.36, 120.12) * mm});
            skLineSegment(sketch, "E839", {"start": v(67.43, 119.56) * mm, "end": v(66.91, 119.66) * mm});
            skLineSegment(sketch, "E840", {"start": v(66.91, 119.66) * mm, "end": v(66.5, 119.73) * mm});
            skLineSegment(sketch, "E841", {"start": v(-7.36, 70.13) * mm, "end": v(-7.77, 69.5) * mm});
            skArc(sketch, "E842", {"start": v(-6.34, 74.26) * mm, "mid": v(-6.82, 73.9) * mm, "end": v(-6.93, 73.33) * mm});
            skArc(sketch, "E843", {"start": v(-6.34, 74.26) * mm, "mid": v(-6.04, 74.35) * mm, "end": v(-5.73, 74.46) * mm});
            skArc(sketch, "E844", {"start": v(-4.7, 74.05) * mm, "mid": v(-5.14, 74.45) * mm, "end": v(-5.73, 74.46) * mm});
            skLineSegment(sketch, "E845", {"start": v(-4.7, 74.05) * mm, "end": v(-4.5, 73.62) * mm});
            skLineSegment(sketch, "E846", {"start": v(-4.5, 73.62) * mm, "end": v(-4.33, 73.28) * mm});
            skLineSegment(sketch, "E847", {"start": v(-4.33, 73.28) * mm, "end": v(-4.24, 73.1) * mm});
            skLineSegment(sketch, "E848", {"start": v(-4.24, 73.1) * mm, "end": v(-4.2, 73.02) * mm});
            skLineSegment(sketch, "E849", {"start": v(-4.2, 73.02) * mm, "end": v(-4.13, 72.93) * mm});
            skLineSegment(sketch, "E850", {"start": v(-4.13, 72.93) * mm, "end": v(-3.89, 72.65) * mm});
            skLineSegment(sketch, "E851", {"start": v(-3.89, 72.65) * mm, "end": v(-3.53, 72.34) * mm});
            skLineSegment(sketch, "E852", {"start": v(-3.53, 72.34) * mm, "end": v(-3.1, 72.04) * mm});
            skLineSegment(sketch, "E853", {"start": v(-3.1, 72.04) * mm, "end": v(-2.48, 71.72) * mm});
            skLineSegment(sketch, "E854", {"start": v(-2.48, 71.72) * mm, "end": v(-1.78, 71.45) * mm});
            skArc(sketch, "E855", {"start": v(-1.78, 71.45) * mm, "mid": v(-1.3, 71.78) * mm, "end": v(-0.83, 72.14) * mm});
            skLineSegment(sketch, "E856", {"start": v(-2.4, 75.72) * mm, "end": v(-2.06, 75.38) * mm});
            skLineSegment(sketch, "E857", {"start": v(-2.06, 75.38) * mm, "end": v(-1.8, 75.12) * mm});
            skLineSegment(sketch, "E858", {"start": v(-1.8, 75.12) * mm, "end": v(-1.65, 74.98) * mm});
            skLineSegment(sketch, "E859", {"start": v(-1.65, 74.98) * mm, "end": v(-1.59, 74.92) * mm});
            skLineSegment(sketch, "E860", {"start": v(-1.59, 74.92) * mm, "end": v(-1.52, 74.83) * mm});
            skLineSegment(sketch, "E861", {"start": v(-1.52, 74.83) * mm, "end": v(-1.33, 74.5) * mm});
            skLineSegment(sketch, "E862", {"start": v(-1.33, 74.5) * mm, "end": v(-1.14, 74.08) * mm});
            skLineSegment(sketch, "E863", {"start": v(-1.14, 74.08) * mm, "end": v(-1, 73.57) * mm});
            skLineSegment(sketch, "E864", {"start": v(-1, 73.57) * mm, "end": v(-0.88, 72.89) * mm});
            skLineSegment(sketch, "E865", {"start": v(-0.88, 72.89) * mm, "end": v(-0.83, 72.14) * mm});
            skArc(sketch, "E866", {"start": v(-2.48, 76.82) * mm, "mid": v(-2.66, 76.26) * mm, "end": v(-2.4, 75.72) * mm});
            skArc(sketch, "E867", {"start": v(-2.48, 76.82) * mm, "mid": v(-2.29, 77.08) * mm, "end": v(-2.1, 77.34) * mm});
            skArc(sketch, "E868", {"start": v(-1.03, 77.62) * mm, "mid": v(-1.62, 77.69) * mm, "end": v(-2.1, 77.34) * mm});
            skLineSegment(sketch, "E869", {"start": v(-1.03, 77.62) * mm, "end": v(-0.6, 77.39) * mm});
            skLineSegment(sketch, "E870", {"start": v(-0.6, 77.39) * mm, "end": v(-0.27, 77.21) * mm});
            skLineSegment(sketch, "E871", {"start": v(-0.27, 77.21) * mm, "end": v(-0.1, 77.12) * mm});
            skLineSegment(sketch, "E872", {"start": v(-0.1, 77.12) * mm, "end": v(-0.02, 77.08) * mm});
            skLineSegment(sketch, "E873", {"start": v(-0.02, 77.08) * mm, "end": v(0.1, 77.04) * mm});
            skLineSegment(sketch, "E874", {"start": v(0.1, 77.04) * mm, "end": v(0.46, 76.96) * mm});
            skLineSegment(sketch, "E875", {"start": v(0.46, 76.96) * mm, "end": v(0.92, 76.92) * mm});
            skLineSegment(sketch, "E876", {"start": v(0.92, 76.92) * mm, "end": v(1.45, 76.94) * mm});
            skLineSegment(sketch, "E877", {"start": v(1.45, 76.94) * mm, "end": v(2.14, 77.04) * mm});
            skLineSegment(sketch, "E878", {"start": v(2.14, 77.04) * mm, "end": v(2.86, 77.23) * mm});
            skArc(sketch, "E879", {"start": v(2.86, 77.23) * mm, "mid": v(3.06, 77.78) * mm, "end": v(3.23, 78.34) * mm});
            skLineSegment(sketch, "E880", {"start": v(-0.15, 80.32) * mm, "end": v(0.32, 80.25) * mm});
            skLineSegment(sketch, "E881", {"start": v(0.32, 80.25) * mm, "end": v(0.7, 80.2) * mm});
            skLineSegment(sketch, "E882", {"start": v(0.7, 80.2) * mm, "end": v(0.9, 80.16) * mm});
            skLineSegment(sketch, "E883", {"start": v(0.9, 80.16) * mm, "end": v(0.98, 80.15) * mm});
            skLineSegment(sketch, "E884", {"start": v(0.98, 80.15) * mm, "end": v(1.09, 80.12) * mm});
            skLineSegment(sketch, "E885", {"start": v(1.09, 80.12) * mm, "end": v(1.43, 79.97) * mm});
            skLineSegment(sketch, "E886", {"start": v(1.43, 79.97) * mm, "end": v(1.83, 79.73) * mm});
            skLineSegment(sketch, "E887", {"start": v(1.83, 79.73) * mm, "end": v(2.25, 79.4) * mm});
            skLineSegment(sketch, "E888", {"start": v(2.25, 79.4) * mm, "end": v(2.75, 78.92) * mm});
            skLineSegment(sketch, "E889", {"start": v(2.75, 78.92) * mm, "end": v(3.23, 78.34) * mm});
            skArc(sketch, "E890", {"start": v(-0.86, 81.17) * mm, "mid": v(-0.67, 80.6) * mm, "end": v(-0.15, 80.32) * mm});
            skArc(sketch, "E891", {"start": v(-0.86, 81.17) * mm, "mid": v(-0.85, 81.49) * mm, "end": v(-0.86, 81.8) * mm});
            skArc(sketch, "E892", {"start": v(-0.15, 82.66) * mm, "mid": v(-0.67, 82.37) * mm, "end": v(-0.86, 81.8) * mm});
            skLineSegment(sketch, "E893", {"start": v(-0.15, 82.66) * mm, "end": v(0.32, 82.73) * mm});
            skLineSegment(sketch, "E894", {"start": v(0.32, 82.73) * mm, "end": v(0.7, 82.78) * mm});
            skLineSegment(sketch, "E895", {"start": v(0.7, 82.78) * mm, "end": v(0.9, 82.81) * mm});
            skLineSegment(sketch, "E896", {"start": v(0.9, 82.81) * mm, "end": v(0.98, 82.82) * mm});
            skLineSegment(sketch, "E897", {"start": v(0.98, 82.82) * mm, "end": v(1.09, 82.86) * mm});
            skLineSegment(sketch, "E898", {"start": v(1.09, 82.86) * mm, "end": v(1.43, 83) * mm});
            skLineSegment(sketch, "E899", {"start": v(1.43, 83) * mm, "end": v(1.83, 83.24) * mm});
            skLineSegment(sketch, "E900", {"start": v(1.83, 83.24) * mm, "end": v(2.25, 83.57) * mm});
            skLineSegment(sketch, "E901", {"start": v(2.25, 83.57) * mm, "end": v(2.75, 84.05) * mm});
            skLineSegment(sketch, "E902", {"start": v(2.75, 84.05) * mm, "end": v(3.23, 84.63) * mm});
            skArc(sketch, "E903", {"start": v(3.23, 84.63) * mm, "mid": v(3.06, 85.2) * mm, "end": v(2.86, 85.75) * mm});
            skLineSegment(sketch, "E904", {"start": v(-1.03, 85.36) * mm, "end": v(-0.6, 85.59) * mm});
            skLineSegment(sketch, "E905", {"start": v(-0.6, 85.59) * mm, "end": v(-0.27, 85.76) * mm});
            skLineSegment(sketch, "E906", {"start": v(-0.27, 85.76) * mm, "end": v(-0.1, 85.85) * mm});
            skLineSegment(sketch, "E907", {"start": v(-0.1, 85.85) * mm, "end": v(-0.02, 85.9) * mm});
            skLineSegment(sketch, "E908", {"start": v(-0.02, 85.9) * mm, "end": v(0.1, 85.93) * mm});
            skLineSegment(sketch, "E909", {"start": v(0.1, 85.93) * mm, "end": v(0.46, 86.01) * mm});
            skLineSegment(sketch, "E910", {"start": v(0.46, 86.01) * mm, "end": v(0.92, 86.05) * mm});
            skLineSegment(sketch, "E911", {"start": v(0.92, 86.05) * mm, "end": v(1.45, 86.04) * mm});
            skLineSegment(sketch, "E912", {"start": v(1.45, 86.04) * mm, "end": v(2.14, 85.94) * mm});
            skLineSegment(sketch, "E913", {"start": v(2.14, 85.94) * mm, "end": v(2.86, 85.75) * mm});
            skArc(sketch, "E914", {"start": v(-2.1, 85.63) * mm, "mid": v(-1.62, 85.29) * mm, "end": v(-1.03, 85.36) * mm});
            skArc(sketch, "E915", {"start": v(-2.1, 85.63) * mm, "mid": v(-2.29, 85.9) * mm, "end": v(-2.48, 86.15) * mm});
            skArc(sketch, "E916", {"start": v(-2.4, 87.26) * mm, "mid": v(-2.66, 86.72) * mm, "end": v(-2.48, 86.15) * mm});
            skLineSegment(sketch, "E917", {"start": v(-2.4, 87.26) * mm, "end": v(-2.06, 87.6) * mm});
            skLineSegment(sketch, "E918", {"start": v(-2.06, 87.6) * mm, "end": v(-1.8, 87.85) * mm});
            skLineSegment(sketch, "E919", {"start": v(-1.8, 87.85) * mm, "end": v(-1.65, 88) * mm});
            skLineSegment(sketch, "E920", {"start": v(-1.65, 88) * mm, "end": v(-1.59, 88.05) * mm});
            skLineSegment(sketch, "E921", {"start": v(-1.59, 88.05) * mm, "end": v(-1.52, 88.15) * mm});
            skLineSegment(sketch, "E922", {"start": v(-1.52, 88.15) * mm, "end": v(-1.33, 88.47) * mm});
            skLineSegment(sketch, "E923", {"start": v(-1.33, 88.47) * mm, "end": v(-1.14, 88.9) * mm});
            skLineSegment(sketch, "E924", {"start": v(-1.14, 88.9) * mm, "end": v(-1, 89.4) * mm});
            skLineSegment(sketch, "E925", {"start": v(-1, 89.4) * mm, "end": v(-0.88, 90.09) * mm});
            skLineSegment(sketch, "E926", {"start": v(-0.88, 90.09) * mm, "end": v(-0.83, 90.84) * mm});
            skArc(sketch, "E927", {"start": v(-0.83, 90.84) * mm, "mid": v(-1.3, 91.2) * mm, "end": v(-1.78, 91.53) * mm});
            skLineSegment(sketch, "E928", {"start": v(-4.7, 88.92) * mm, "end": v(-4.5, 89.36) * mm});
            skLineSegment(sketch, "E929", {"start": v(-4.5, 89.36) * mm, "end": v(-4.33, 89.7) * mm});
            skLineSegment(sketch, "E930", {"start": v(-4.33, 89.7) * mm, "end": v(-4.24, 89.87) * mm});
            skLineSegment(sketch, "E931", {"start": v(-4.24, 89.87) * mm, "end": v(-4.2, 89.95) * mm});
            skLineSegment(sketch, "E932", {"start": v(-4.2, 89.95) * mm, "end": v(-4.13, 90.05) * mm});
            skLineSegment(sketch, "E933", {"start": v(-4.13, 90.05) * mm, "end": v(-3.89, 90.33) * mm});
            skLineSegment(sketch, "E934", {"start": v(-3.89, 90.33) * mm, "end": v(-3.53, 90.63) * mm});
            skLineSegment(sketch, "E935", {"start": v(-3.53, 90.63) * mm, "end": v(-3.1, 90.93) * mm});
            skLineSegment(sketch, "E936", {"start": v(-3.1, 90.93) * mm, "end": v(-2.48, 91.26) * mm});
            skLineSegment(sketch, "E937", {"start": v(-2.48, 91.26) * mm, "end": v(-1.78, 91.53) * mm});
            skArc(sketch, "E938", {"start": v(-5.73, 88.51) * mm, "mid": v(-5.14, 88.52) * mm, "end": v(-4.7, 88.92) * mm});
            skArc(sketch, "E939", {"start": v(-5.73, 88.51) * mm, "mid": v(-6.04, 88.62) * mm, "end": v(-6.34, 88.71) * mm});
            skArc(sketch, "E940", {"start": v(34.94, 90.13) * mm, "mid": v(35.05, 89.55) * mm, "end": v(35.53, 89.2) * mm});
            skLineSegment(sketch, "E941", {"start": v(34.94, 90.13) * mm, "end": v(35.02, 90.6) * mm});
            skLineSegment(sketch, "E942", {"start": v(35.02, 90.6) * mm, "end": v(35.09, 90.98) * mm});
            skLineSegment(sketch, "E943", {"start": v(35.09, 90.98) * mm, "end": v(35.12, 91.17) * mm});
            skLineSegment(sketch, "E944", {"start": v(35.12, 91.17) * mm, "end": v(35.13, 91.26) * mm});
            skLineSegment(sketch, "E945", {"start": v(35.13, 91.26) * mm, "end": v(35.14, 91.38) * mm});
            skLineSegment(sketch, "E946", {"start": v(35.14, 91.38) * mm, "end": v(35.1, 91.75) * mm});
            skLineSegment(sketch, "E947", {"start": v(35.1, 91.75) * mm, "end": v(35, 92.2) * mm});
            skLineSegment(sketch, "E948", {"start": v(35, 92.2) * mm, "end": v(34.82, 92.7) * mm});
            skLineSegment(sketch, "E949", {"start": v(34.82, 92.7) * mm, "end": v(34.51, 93.33) * mm});
            skLineSegment(sketch, "E950", {"start": v(34.51, 93.33) * mm, "end": v(34.1, 93.96) * mm});
            skArc(sketch, "E951", {"start": v(34.1, 93.96) * mm, "mid": v(33.52, 93.97) * mm, "end": v(32.93, 93.96) * mm});
            skLineSegment(sketch, "E952", {"start": v(32.1, 90.13) * mm, "end": v(32.02, 90.6) * mm});
            skLineSegment(sketch, "E953", {"start": v(32.02, 90.6) * mm, "end": v(31.95, 90.98) * mm});
            skLineSegment(sketch, "E954", {"start": v(31.95, 90.98) * mm, "end": v(31.92, 91.17) * mm});
            skLineSegment(sketch, "E955", {"start": v(31.92, 91.17) * mm, "end": v(31.9, 91.26) * mm});
            skLineSegment(sketch, "E956", {"start": v(31.9, 91.26) * mm, "end": v(31.9, 91.38) * mm});
            skLineSegment(sketch, "E957", {"start": v(31.9, 91.38) * mm, "end": v(31.94, 91.75) * mm});
            skLineSegment(sketch, "E958", {"start": v(31.94, 91.75) * mm, "end": v(32.04, 92.2) * mm});
            skLineSegment(sketch, "E959", {"start": v(32.04, 92.2) * mm, "end": v(32.22, 92.7) * mm});
            skLineSegment(sketch, "E960", {"start": v(32.22, 92.7) * mm, "end": v(32.53, 93.33) * mm});
            skLineSegment(sketch, "E961", {"start": v(32.53, 93.33) * mm, "end": v(32.93, 93.96) * mm});
            skArc(sketch, "E962", {"start": v(31.51, 89.2) * mm, "mid": v(31.99, 89.55) * mm, "end": v(32.1, 90.13) * mm});
            skArc(sketch, "E963", {"start": v(31.51, 89.2) * mm, "mid": v(31.2, 89.1) * mm, "end": v(30.9, 89) * mm});
            skArc(sketch, "E964", {"start": v(29.87, 89.4) * mm, "mid": v(30.3, 89) * mm, "end": v(30.9, 89) * mm});
            skLineSegment(sketch, "E965", {"start": v(29.87, 89.4) * mm, "end": v(29.66, 89.84) * mm});
            skLineSegment(sketch, "E966", {"start": v(29.66, 89.84) * mm, "end": v(29.5, 90.18) * mm});
            skLineSegment(sketch, "E967", {"start": v(29.5, 90.18) * mm, "end": v(29.4, 90.36) * mm});
            skLineSegment(sketch, "E968", {"start": v(29.4, 90.36) * mm, "end": v(29.36, 90.44) * mm});
            skLineSegment(sketch, "E969", {"start": v(29.36, 90.44) * mm, "end": v(29.3, 90.53) * mm});
            skLineSegment(sketch, "E970", {"start": v(29.3, 90.53) * mm, "end": v(29.05, 90.81) * mm});
            skLineSegment(sketch, "E971", {"start": v(29.05, 90.81) * mm, "end": v(28.7, 91.12) * mm});
            skLineSegment(sketch, "E972", {"start": v(28.7, 91.12) * mm, "end": v(28.26, 91.42) * mm});
            skLineSegment(sketch, "E973", {"start": v(28.26, 91.42) * mm, "end": v(27.65, 91.74) * mm});
            skLineSegment(sketch, "E974", {"start": v(27.65, 91.74) * mm, "end": v(26.95, 92.01) * mm});
            skArc(sketch, "E975", {"start": v(26.95, 92.01) * mm, "mid": v(26.47, 91.68) * mm, "end": v(26, 91.32) * mm});
            skLineSegment(sketch, "E976", {"start": v(27.57, 87.74) * mm, "end": v(27.23, 88.08) * mm});
            skLineSegment(sketch, "E977", {"start": v(27.23, 88.08) * mm, "end": v(26.96, 88.34) * mm});
            skLineSegment(sketch, "E978", {"start": v(26.96, 88.34) * mm, "end": v(26.82, 88.48) * mm});
            skLineSegment(sketch, "E979", {"start": v(26.82, 88.48) * mm, "end": v(26.76, 88.54) * mm});
            skLineSegment(sketch, "E980", {"start": v(26.76, 88.54) * mm, "end": v(26.68, 88.63) * mm});
            skLineSegment(sketch, "E981", {"start": v(26.68, 88.63) * mm, "end": v(26.5, 88.95) * mm});
            skLineSegment(sketch, "E982", {"start": v(26.5, 88.95) * mm, "end": v(26.31, 89.38) * mm});
            skLineSegment(sketch, "E983", {"start": v(33.59, 112.05) * mm, "end": v(33.6, 111.64) * mm});
            skLineSegment(sketch, "E984", {"start": v(28.57, 142.91) * mm, "end": v(28.49, 142.48) * mm});
            skLineSegment(sketch, "E985", {"start": v(32.56, 158.7) * mm, "end": v(33.12, 159.06) * mm});
            skLineSegment(sketch, "E986", {"start": v(33.6, 111.64) * mm, "end": v(33.6, 111.44) * mm});
            skLineSegment(sketch, "E987", {"start": v(28.49, 142.48) * mm, "end": v(28.45, 142.27) * mm});
            skArc(sketch, "E988", {"start": v(30.09, 155.12) * mm, "mid": v(30.63, 155.29) * mm, "end": v(30.92, 155.78) * mm});
            skLineSegment(sketch, "E989", {"start": v(33.6, 111.44) * mm, "end": v(33.6, 111.36) * mm});
            skLineSegment(sketch, "E990", {"start": v(28.45, 142.27) * mm, "end": v(28.43, 142.2) * mm});
            skArc(sketch, "E991", {"start": v(30.09, 155.12) * mm, "mid": v(29.8, 155.12) * mm, "end": v(29.5, 155.12) * mm});
            skLineSegment(sketch, "E992", {"start": v(33.6, 111.36) * mm, "end": v(33.58, 111.24) * mm});
            skLineSegment(sketch, "E993", {"start": v(28.43, 142.2) * mm, "end": v(28.41, 142.15) * mm});
            skArc(sketch, "E994", {"start": v(28.67, 155.78) * mm, "mid": v(28.96, 155.29) * mm, "end": v(29.5, 155.12) * mm});
            skLineSegment(sketch, "E995", {"start": v(33.58, 111.24) * mm, "end": v(33.47, 110.85) * mm});
            skLineSegment(sketch, "E996", {"start": v(28.41, 142.15) * mm, "end": v(28.4, 142.08) * mm});
            skLineSegment(sketch, "E997", {"start": v(28.67, 155.78) * mm, "end": v(28.57, 156.34) * mm});
            skLineSegment(sketch, "E998", {"start": v(33.47, 110.85) * mm, "end": v(33.27, 110.4) * mm});
            skLineSegment(sketch, "E999", {"start": v(28.4, 142.08) * mm, "end": v(28.2, 141.73) * mm});
            skLineSegment(sketch, "E1000", {"start": v(28.57, 156.34) * mm, "end": v(28.49, 156.77) * mm});
            skLineSegment(sketch, "E1001", {"start": v(33.27, 110.4) * mm, "end": v(32.97, 109.91) * mm});
            skLineSegment(sketch, "E1002", {"start": v(28.2, 141.73) * mm, "end": v(27.91, 141.34) * mm});
            skLineSegment(sketch, "E1003", {"start": v(28.49, 156.77) * mm, "end": v(28.45, 156.98) * mm});
            skLineSegment(sketch, "E1004", {"start": v(32.97, 109.91) * mm, "end": v(32.59, 109.42) * mm});
            skLineSegment(sketch, "E1005", {"start": v(27.91, 141.34) * mm, "end": v(27.52, 140.93) * mm});
            skLineSegment(sketch, "E1006", {"start": v(28.45, 156.98) * mm, "end": v(28.43, 157.05) * mm});
            skLineSegment(sketch, "E1007", {"start": v(32.59, 109.42) * mm, "end": v(32.12, 108.93) * mm});
            skLineSegment(sketch, "E1008", {"start": v(27.52, 140.93) * mm, "end": v(27.03, 140.55) * mm});
            skLineSegment(sketch, "E1009", {"start": v(28.43, 157.05) * mm, "end": v(28.41, 157.1) * mm});
            skArc(sketch, "E1010", {"start": v(34.3, 113.4) * mm, "mid": v(33.78, 113.13) * mm, "end": v(33.58, 112.58) * mm});
            skLineSegment(sketch, "E1011", {"start": v(27.03, 140.55) * mm, "end": v(26.47, 140.2) * mm});
            skLineSegment(sketch, "E1012", {"start": v(28.41, 157.1) * mm, "end": v(28.4, 157.16) * mm});
            skArc(sketch, "E1013", {"start": v(34.3, 113.4) * mm, "mid": v(34.6, 113.45) * mm, "end": v(34.9, 113.5) * mm});
            skArc(sketch, "E1014", {"start": v(29.5, 144.13) * mm, "mid": v(28.96, 143.96) * mm, "end": v(28.67, 143.47) * mm});
            skLineSegment(sketch, "E1015", {"start": v(28.4, 157.16) * mm, "end": v(28.2, 157.52) * mm});
            skArc(sketch, "E1016", {"start": v(76.95, 111.31) * mm, "mid": v(76.58, 111.76) * mm, "end": v(76, 111.85) * mm});
            skArc(sketch, "E1017", {"start": v(29.5, 144.13) * mm, "mid": v(29.8, 144.12) * mm, "end": v(30.09, 144.13) * mm});
            skLineSegment(sketch, "E1018", {"start": v(28.2, 157.52) * mm, "end": v(27.91, 157.91) * mm});
            skLineSegment(sketch, "E1019", {"start": v(76.95, 111.31) * mm, "end": v(77.13, 110.82) * mm});
            skArc(sketch, "E1020", {"start": v(30.92, 143.47) * mm, "mid": v(30.63, 143.96) * mm, "end": v(30.09, 144.13) * mm});
            skLineSegment(sketch, "E1021", {"start": v(27.91, 157.91) * mm, "end": v(27.52, 158.31) * mm});
            skLineSegment(sketch, "E1022", {"start": v(77.13, 110.82) * mm, "end": v(77.26, 110.43) * mm});
            skLineSegment(sketch, "E1023", {"start": v(30.92, 143.47) * mm, "end": v(31.02, 142.91) * mm});
            skLineSegment(sketch, "E1024", {"start": v(27.52, 158.31) * mm, "end": v(27.03, 158.7) * mm});
            skLineSegment(sketch, "E1025", {"start": v(77.26, 110.43) * mm, "end": v(77.33, 110.24) * mm});
            skLineSegment(sketch, "E1026", {"start": v(31.02, 142.91) * mm, "end": v(31.1, 142.48) * mm});
            skLineSegment(sketch, "E1027", {"start": v(27.03, 158.7) * mm, "end": v(26.47, 159.06) * mm});
            skLineSegment(sketch, "E1028", {"start": v(77.33, 110.24) * mm, "end": v(77.36, 110.17) * mm});
            skLineSegment(sketch, "E1029", {"start": v(31.1, 142.48) * mm, "end": v(31.14, 142.27) * mm});
            skArc(sketch, "E1030", {"start": v(26.47, 159.06) * mm, "mid": v(25.97, 158.86) * mm, "end": v(25.47, 158.64) * mm});
            skLineSegment(sketch, "E1031", {"start": v(77.36, 110.17) * mm, "end": v(77.41, 110.06) * mm});
            skLineSegment(sketch, "E1032", {"start": v(31.14, 142.27) * mm, "end": v(31.16, 142.2) * mm});
            skLineSegment(sketch, "E1033", {"start": v(26.24, 154.77) * mm, "end": v(25.92, 155.24) * mm});
            skLineSegment(sketch, "E1034", {"start": v(77.41, 110.06) * mm, "end": v(77.64, 109.73) * mm});
            skLineSegment(sketch, "E1035", {"start": v(31.16, 142.2) * mm, "end": v(31.18, 142.15) * mm});
            skLineSegment(sketch, "E1036", {"start": v(25.92, 155.24) * mm, "end": v(25.67, 155.6) * mm});
            skLineSegment(sketch, "E1037", {"start": v(77.64, 109.73) * mm, "end": v(78, 109.37) * mm});
            skLineSegment(sketch, "E1038", {"start": v(31.18, 142.15) * mm, "end": v(31.2, 142.08) * mm});
            skLineSegment(sketch, "E1039", {"start": v(25.67, 155.6) * mm, "end": v(25.55, 155.78) * mm});
            skLineSegment(sketch, "E1040", {"start": v(78, 109.37) * mm, "end": v(78.44, 109.02) * mm});
            skLineSegment(sketch, "E1041", {"start": v(31.2, 142.08) * mm, "end": v(31.38, 141.73) * mm});
            skLineSegment(sketch, "E1042", {"start": v(25.55, 155.78) * mm, "end": v(25.5, 155.84) * mm});
            skLineSegment(sketch, "E1043", {"start": v(78.44, 109.02) * mm, "end": v(78.97, 108.68) * mm});
            skLineSegment(sketch, "E1044", {"start": v(31.38, 141.73) * mm, "end": v(31.68, 141.34) * mm});
            skLineSegment(sketch, "E1045", {"start": v(25.5, 155.84) * mm, "end": v(25.48, 155.89) * mm});
            skLineSegment(sketch, "E1046", {"start": v(78.97, 108.68) * mm, "end": v(79.57, 108.39) * mm});
            skLineSegment(sketch, "E1047", {"start": v(31.68, 141.34) * mm, "end": v(32.07, 140.93) * mm});
            skLineSegment(sketch, "E1048", {"start": v(25.48, 155.89) * mm, "end": v(25.46, 155.95) * mm});
            skArc(sketch, "E1049", {"start": v(79.57, 108.39) * mm, "mid": v(80.07, 108.66) * mm, "end": v(80.55, 108.95) * mm});
            skLineSegment(sketch, "E1050", {"start": v(32.07, 140.93) * mm, "end": v(32.56, 140.55) * mm});
            skLineSegment(sketch, "E1051", {"start": v(25.46, 155.95) * mm, "end": v(25.34, 156.33) * mm});
            skLineSegment(sketch, "E1052", {"start": v(79.33, 112.69) * mm, "end": v(79.67, 112.29) * mm});
            skLineSegment(sketch, "E1053", {"start": v(32.56, 140.55) * mm, "end": v(33.12, 140.2) * mm});
            skLineSegment(sketch, "E1054", {"start": v(25.34, 156.33) * mm, "end": v(25.27, 156.82) * mm});
            skLineSegment(sketch, "E1055", {"start": v(79.67, 112.29) * mm, "end": v(79.94, 111.98) * mm});
            skArc(sketch, "E1056", {"start": v(33.12, 140.2) * mm, "mid": v(33.62, 140.39) * mm, "end": v(34.12, 140.6) * mm});
            skLineSegment(sketch, "E1057", {"start": v(25.27, 156.82) * mm, "end": v(25.26, 157.38) * mm});
            skLineSegment(sketch, "E1058", {"start": v(79.94, 111.98) * mm, "end": v(80.07, 111.82) * mm});
            skLineSegment(sketch, "E1059", {"start": v(33.35, 144.48) * mm, "end": v(33.67, 144) * mm});
            skLineSegment(sketch, "E1060", {"start": v(25.26, 157.38) * mm, "end": v(25.33, 158) * mm});
            skLineSegment(sketch, "E1061", {"start": v(80.07, 111.82) * mm, "end": v(80.12, 111.76) * mm});
            skLineSegment(sketch, "E1062", {"start": v(33.67, 144) * mm, "end": v(33.92, 143.65) * mm});
            skLineSegment(sketch, "E1063", {"start": v(25.33, 158) * mm, "end": v(25.47, 158.64) * mm});
            skLineSegment(sketch, "E1064", {"start": v(80.12, 111.76) * mm, "end": v(80.19, 111.66) * mm});
            skLineSegment(sketch, "E1065", {"start": v(33.92, 143.65) * mm, "end": v(34.04, 143.47) * mm});
            skArc(sketch, "E1066", {"start": v(26.12, 153.71) * mm, "mid": v(26.38, 154.22) * mm, "end": v(26.24, 154.77) * mm});
            skLineSegment(sketch, "E1067", {"start": v(80.19, 111.66) * mm, "end": v(80.35, 111.3) * mm});
            skLineSegment(sketch, "E1068", {"start": v(34.04, 143.47) * mm, "end": v(34.08, 143.4) * mm});
            skArc(sketch, "E1069", {"start": v(26.12, 153.71) * mm, "mid": v(25.9, 153.51) * mm, "end": v(25.7, 153.3) * mm});
            skLineSegment(sketch, "E1070", {"start": v(80.35, 111.3) * mm, "end": v(80.5, 110.82) * mm});
            skLineSegment(sketch, "E1071", {"start": v(34.08, 143.4) * mm, "end": v(34.1, 143.36) * mm});
            skArc(sketch, "E1072", {"start": v(24.65, 153.18) * mm, "mid": v(25.2, 153.04) * mm, "end": v(25.7, 153.3) * mm});
            skLineSegment(sketch, "E1073", {"start": v(80.5, 110.82) * mm, "end": v(80.58, 110.25) * mm});
            skLineSegment(sketch, "E1074", {"start": v(34.1, 143.36) * mm, "end": v(34.13, 143.3) * mm});
            skLineSegment(sketch, "E1075", {"start": v(24.65, 153.18) * mm, "end": v(24.18, 153.5) * mm});
            skLineSegment(sketch, "E1076", {"start": v(80.58, 110.25) * mm, "end": v(80.6, 109.63) * mm});
            skLineSegment(sketch, "E1077", {"start": v(34.13, 143.3) * mm, "end": v(34.25, 142.92) * mm});
            skLineSegment(sketch, "E1078", {"start": v(24.18, 153.5) * mm, "end": v(23.82, 153.75) * mm});
            skLineSegment(sketch, "E1079", {"start": v(80.6, 109.63) * mm, "end": v(80.55, 108.95) * mm});
            skLineSegment(sketch, "E1080", {"start": v(34.25, 142.92) * mm, "end": v(34.32, 142.43) * mm});
            skLineSegment(sketch, "E1081", {"start": v(23.82, 153.75) * mm, "end": v(23.64, 153.87) * mm});
            skArc(sketch, "E1082", {"start": v(79.35, 113.78) * mm, "mid": v(79.13, 113.23) * mm, "end": v(79.33, 112.69) * mm});
            skLineSegment(sketch, "E1083", {"start": v(34.32, 142.43) * mm, "end": v(34.33, 141.87) * mm});
            skLineSegment(sketch, "E1084", {"start": v(23.64, 153.87) * mm, "end": v(23.58, 153.91) * mm});
            skArc(sketch, "E1085", {"start": v(79.35, 113.78) * mm, "mid": v(79.55, 114) * mm, "end": v(79.74, 114.25) * mm});
            skLineSegment(sketch, "E1086", {"start": v(34.33, 141.87) * mm, "end": v(34.26, 141.25) * mm});
            skLineSegment(sketch, "E1087", {"start": v(23.58, 153.91) * mm, "end": v(23.53, 153.94) * mm});
            skArc(sketch, "E1088", {"start": v(80.81, 114.45) * mm, "mid": v(80.24, 114.56) * mm, "end": v(79.74, 114.25) * mm});
            skLineSegment(sketch, "E1089", {"start": v(34.26, 141.25) * mm, "end": v(34.12, 140.6) * mm});
            skLineSegment(sketch, "E1090", {"start": v(23.53, 153.94) * mm, "end": v(23.47, 153.96) * mm});
            skLineSegment(sketch, "E1091", {"start": v(80.81, 114.45) * mm, "end": v(81.26, 114.18) * mm});
            skArc(sketch, "E1092", {"start": v(33.47, 145.53) * mm, "mid": v(33.21, 145.03) * mm, "end": v(33.35, 144.48) * mm});
            skLineSegment(sketch, "E1093", {"start": v(23.47, 153.96) * mm, "end": v(23.1, 154.08) * mm});
            skLineSegment(sketch, "E1094", {"start": v(81.26, 114.18) * mm, "end": v(81.61, 113.98) * mm});
            skArc(sketch, "E1095", {"start": v(33.47, 145.53) * mm, "mid": v(33.68, 145.74) * mm, "end": v(33.89, 145.95) * mm});
            skLineSegment(sketch, "E1096", {"start": v(23.1, 154.08) * mm, "end": v(22.6, 154.15) * mm});
            skLineSegment(sketch, "E1097", {"start": v(81.61, 113.98) * mm, "end": v(81.79, 113.87) * mm});
            skArc(sketch, "E1098", {"start": v(109.81, 119.73) * mm, "mid": v(112.26, 120.9) * mm, "end": v(109.81, 122.05) * mm});
            skLineSegment(sketch, "E1099", {"start": v(22.6, 154.15) * mm, "end": v(22.04, 154.16) * mm});
            skLineSegment(sketch, "E1100", {"start": v(81.79, 113.87) * mm, "end": v(81.86, 113.83) * mm});
            skLineSegment(sketch, "E1101", {"start": v(109.81, 122.05) * mm, "end": v(109.81, 119.73) * mm});
            skLineSegment(sketch, "E1102", {"start": v(22.04, 154.16) * mm, "end": v(21.42, 154.1) * mm});
            skLineSegment(sketch, "E1103", {"start": v(80.35, 125.08) * mm, "end": v(80.5, 125.56) * mm});
            skLineSegment(sketch, "E1104", {"start": v(80.5, 125.56) * mm, "end": v(80.58, 126.12) * mm});
            skLineSegment(sketch, "E1105", {"start": v(26.31, 89.38) * mm, "end": v(26.16, 89.9) * mm});
            skLineSegment(sketch, "E1106", {"start": v(80.58, 126.12) * mm, "end": v(80.6, 126.75) * mm});
            skLineSegment(sketch, "E1107", {"start": v(26.16, 89.9) * mm, "end": v(26.04, 90.57) * mm});
            skLineSegment(sketch, "E1108", {"start": v(80.6, 126.75) * mm, "end": v(80.55, 127.42) * mm});
            skLineSegment(sketch, "E1109", {"start": v(26.04, 90.57) * mm, "end": v(26, 91.32) * mm});
            skArc(sketch, "E1110", {"start": v(80.55, 127.42) * mm, "mid": v(80.07, 127.71) * mm, "end": v(79.57, 127.98) * mm});
            skArc(sketch, "E1111", {"start": v(27.65, 86.64) * mm, "mid": v(27.82, 87.2) * mm, "end": v(27.57, 87.74) * mm});
            skLineSegment(sketch, "E1112", {"start": v(76.95, 125.06) * mm, "end": v(77.13, 125.55) * mm});
            skArc(sketch, "E1113", {"start": v(27.65, 86.64) * mm, "mid": v(27.45, 86.38) * mm, "end": v(27.27, 86.12) * mm});
            skLineSegment(sketch, "E1114", {"start": v(77.13, 125.55) * mm, "end": v(77.26, 125.94) * mm});
            skArc(sketch, "E1115", {"start": v(26.2, 85.84) * mm, "mid": v(26.79, 85.77) * mm, "end": v(27.27, 86.12) * mm});
            skLineSegment(sketch, "E1116", {"start": v(77.26, 125.94) * mm, "end": v(77.33, 126.13) * mm});
            skLineSegment(sketch, "E1117", {"start": v(26.2, 85.84) * mm, "end": v(25.77, 86.07) * mm});
            skLineSegment(sketch, "E1118", {"start": v(77.33, 126.13) * mm, "end": v(77.36, 126.2) * mm});
            skLineSegment(sketch, "E1119", {"start": v(25.77, 86.07) * mm, "end": v(25.44, 86.25) * mm});
            skLineSegment(sketch, "E1120", {"start": v(77.36, 126.2) * mm, "end": v(77.41, 126.31) * mm});
            skLineSegment(sketch, "E1121", {"start": v(25.44, 86.25) * mm, "end": v(25.26, 86.34) * mm});
            skLineSegment(sketch, "E1122", {"start": v(77.41, 126.31) * mm, "end": v(77.64, 126.64) * mm});
            skLineSegment(sketch, "E1123", {"start": v(25.26, 86.34) * mm, "end": v(25.18, 86.38) * mm});
            skLineSegment(sketch, "E1124", {"start": v(77.64, 126.64) * mm, "end": v(78, 127) * mm});
            skLineSegment(sketch, "E1125", {"start": v(25.18, 86.38) * mm, "end": v(25.08, 86.42) * mm});
            skLineSegment(sketch, "E1126", {"start": v(78, 127) * mm, "end": v(78.44, 127.35) * mm});
            skLineSegment(sketch, "E1127", {"start": v(25.08, 86.42) * mm, "end": v(24.71, 86.5) * mm});
            skLineSegment(sketch, "E1128", {"start": v(78.44, 127.35) * mm, "end": v(78.97, 127.69) * mm});
            skLineSegment(sketch, "E1129", {"start": v(24.71, 86.5) * mm, "end": v(24.25, 86.54) * mm});
            skLineSegment(sketch, "E1130", {"start": v(78.97, 127.69) * mm, "end": v(79.57, 127.98) * mm});
            skLineSegment(sketch, "E1131", {"start": v(24.25, 86.54) * mm, "end": v(23.71, 86.52) * mm});
            skArc(sketch, "E1132", {"start": v(76, 124.53) * mm, "mid": v(76.58, 124.6) * mm, "end": v(76.95, 125.06) * mm});
            skLineSegment(sketch, "E1133", {"start": v(23.71, 86.52) * mm, "end": v(23.03, 86.42) * mm});
            skArc(sketch, "E1134", {"start": v(76, 124.53) * mm, "mid": v(75.7, 124.59) * mm, "end": v(75.4, 124.63) * mm});
            skLineSegment(sketch, "E1135", {"start": v(23.03, 86.42) * mm, "end": v(22.3, 86.23) * mm});
            skArc(sketch, "E1136", {"start": v(74.68, 125.46) * mm, "mid": v(74.88, 124.9) * mm, "end": v(75.4, 124.63) * mm});
            skArc(sketch, "E1137", {"start": v(22.3, 86.23) * mm, "mid": v(22.1, 85.68) * mm, "end": v(21.94, 85.12) * mm});
            skLineSegment(sketch, "E1138", {"start": v(74.68, 125.46) * mm, "end": v(74.69, 125.98) * mm});
            skLineSegment(sketch, "E1139", {"start": v(25.32, 83.14) * mm, "end": v(24.84, 83.21) * mm});
            skLineSegment(sketch, "E1140", {"start": v(74.69, 125.98) * mm, "end": v(74.7, 126.4) * mm});
            skLineSegment(sketch, "E1141", {"start": v(24.84, 83.21) * mm, "end": v(24.47, 83.27) * mm});
            skLineSegment(sketch, "E1142", {"start": v(74.7, 126.4) * mm, "end": v(74.7, 126.6) * mm});
            skLineSegment(sketch, "E1143", {"start": v(24.47, 83.27) * mm, "end": v(24.27, 83.3) * mm});
            skLineSegment(sketch, "E1144", {"start": v(74.7, 126.6) * mm, "end": v(74.7, 126.68) * mm});
            skLineSegment(sketch, "E1145", {"start": v(24.27, 83.3) * mm, "end": v(24.19, 83.3) * mm});
            skLineSegment(sketch, "E1146", {"start": v(74.7, 126.68) * mm, "end": v(74.68, 126.8) * mm});
            skLineSegment(sketch, "E1147", {"start": v(24.19, 83.3) * mm, "end": v(24.08, 83.34) * mm});
            skLineSegment(sketch, "E1148", {"start": v(74.68, 126.8) * mm, "end": v(74.57, 127.18) * mm});
            skLineSegment(sketch, "E1149", {"start": v(24.08, 83.34) * mm, "end": v(23.73, 83.49) * mm});
            skLineSegment(sketch, "E1150", {"start": v(71.53, 127.14) * mm, "end": v(71.64, 127.7) * mm});
            skLineSegment(sketch, "E1151", {"start": v(24.08, 80.6) * mm, "end": v(23.73, 80.46) * mm});
            skLineSegment(sketch, "E1152", {"start": v(71.64, 127.7) * mm, "end": v(71.83, 128.3) * mm});
            skLineSegment(sketch, "E1153", {"start": v(23.73, 80.46) * mm, "end": v(23.33, 80.22) * mm});
            skLineSegment(sketch, "E1154", {"start": v(71.83, 128.3) * mm, "end": v(72.1, 128.9) * mm});
            skLineSegment(sketch, "E1155", {"start": v(23.33, 80.22) * mm, "end": v(22.91, 79.9) * mm});
            skArc(sketch, "E1156", {"start": v(71.6, 123.96) * mm, "mid": v(71.98, 124.4) * mm, "end": v(71.98, 124.98) * mm});
            skLineSegment(sketch, "E1157", {"start": v(22.91, 79.9) * mm, "end": v(22.42, 79.4) * mm});
            skArc(sketch, "E1158", {"start": v(69.98, 123.83) * mm, "mid": v(70.48, 123.54) * mm, "end": v(71.06, 123.65) * mm});
            skArc(sketch, "E1159", {"start": v(21.94, 78.83) * mm, "mid": v(22.1, 78.26) * mm, "end": v(22.3, 77.71) * mm});
            skLineSegment(sketch, "E1160", {"start": v(69.4, 124.55) * mm, "end": v(69.26, 124.7) * mm});
            skLineSegment(sketch, "E1161", {"start": v(25.44, 77.7) * mm, "end": v(25.26, 77.6) * mm});
            skLineSegment(sketch, "E1162", {"start": v(69.65, 124.24) * mm, "end": v(69.4, 124.55) * mm});
            skLineSegment(sketch, "E1163", {"start": v(25.77, 77.87) * mm, "end": v(25.44, 77.7) * mm});
            skArc(sketch, "E1164", {"start": v(71.6, 123.96) * mm, "mid": v(71.32, 123.82) * mm, "end": v(71.06, 123.65) * mm});
            skLineSegment(sketch, "E1165", {"start": v(22.42, 79.4) * mm, "end": v(21.94, 78.83) * mm});
            skLineSegment(sketch, "E1166", {"start": v(69.98, 123.83) * mm, "end": v(69.65, 124.24) * mm});
            skLineSegment(sketch, "E1167", {"start": v(26.2, 78.1) * mm, "end": v(25.77, 77.87) * mm});
            skLineSegment(sketch, "E1168", {"start": v(71.5, 126.64) * mm, "end": v(71.53, 127.14) * mm});
            skLineSegment(sketch, "E1169", {"start": v(24.19, 80.64) * mm, "end": v(24.08, 80.6) * mm});
            skLineSegment(sketch, "E1170", {"start": v(71.52, 126.24) * mm, "end": v(71.5, 126.64) * mm});
            skLineSegment(sketch, "E1171", {"start": v(24.27, 80.65) * mm, "end": v(24.19, 80.64) * mm});
            skLineSegment(sketch, "E1172", {"start": v(71.55, 126.12) * mm, "end": v(71.52, 126.24) * mm});
            skLineSegment(sketch, "E1173", {"start": v(24.47, 80.68) * mm, "end": v(24.27, 80.65) * mm});
            skLineSegment(sketch, "E1174", {"start": v(71.57, 126.05) * mm, "end": v(71.55, 126.12) * mm});
            skLineSegment(sketch, "E1175", {"start": v(24.84, 80.73) * mm, "end": v(24.47, 80.68) * mm});
            skLineSegment(sketch, "E1176", {"start": v(71.65, 125.85) * mm, "end": v(71.57, 126.05) * mm});
            skLineSegment(sketch, "E1177", {"start": v(25.32, 80.8) * mm, "end": v(24.84, 80.73) * mm});
            skLineSegment(sketch, "E1178", {"start": v(71.8, 125.47) * mm, "end": v(71.65, 125.85) * mm});
            skArc(sketch, "E1179", {"start": v(25.32, 80.8) * mm, "mid": v(25.84, 81.09) * mm, "end": v(26.03, 81.65) * mm});
            skLineSegment(sketch, "E1180", {"start": v(71.98, 124.98) * mm, "end": v(71.8, 125.47) * mm});
            skArc(sketch, "E1181", {"start": v(26.03, 82.3) * mm, "mid": v(26.02, 81.97) * mm, "end": v(26.03, 81.65) * mm});
            skArc(sketch, "E1182", {"start": v(73.22, 129.1) * mm, "mid": v(72.66, 129.02) * mm, "end": v(72.1, 128.9) * mm});
            skArc(sketch, "E1183", {"start": v(26.03, 82.3) * mm, "mid": v(25.84, 82.86) * mm, "end": v(25.32, 83.14) * mm});
            skLineSegment(sketch, "E1184", {"start": v(73.69, 128.62) * mm, "end": v(73.22, 129.1) * mm});
            skLineSegment(sketch, "E1185", {"start": v(22.42, 84.54) * mm, "end": v(21.94, 85.12) * mm});
            skLineSegment(sketch, "E1186", {"start": v(74.07, 128.12) * mm, "end": v(73.69, 128.62) * mm});
            skLineSegment(sketch, "E1187", {"start": v(22.91, 84.05) * mm, "end": v(22.42, 84.54) * mm});
            skLineSegment(sketch, "E1188", {"start": v(74.37, 127.64) * mm, "end": v(74.07, 128.12) * mm});
            skLineSegment(sketch, "E1189", {"start": v(23.33, 83.73) * mm, "end": v(22.91, 84.05) * mm});
            skLineSegment(sketch, "E1190", {"start": v(74.57, 127.18) * mm, "end": v(74.37, 127.64) * mm});
            skLineSegment(sketch, "E1191", {"start": v(23.73, 83.49) * mm, "end": v(23.33, 83.73) * mm});
            skLineSegment(sketch, "E1192", {"start": v(80.19, 124.71) * mm, "end": v(80.35, 125.08) * mm});
            skLineSegment(sketch, "E1193", {"start": v(80.12, 124.6) * mm, "end": v(80.19, 124.71) * mm});
            skLineSegment(sketch, "E1194", {"start": v(80.07, 124.55) * mm, "end": v(80.12, 124.6) * mm});
            skLineSegment(sketch, "E1195", {"start": v(79.94, 124.4) * mm, "end": v(80.07, 124.55) * mm});
            skLineSegment(sketch, "E1196", {"start": v(79.67, 124.08) * mm, "end": v(79.94, 124.4) * mm});
            skLineSegment(sketch, "E1197", {"start": v(79.33, 123.69) * mm, "end": v(79.67, 124.08) * mm});
            skArc(sketch, "E1198", {"start": v(79.33, 123.69) * mm, "mid": v(79.13, 123.14) * mm, "end": v(79.35, 122.6) * mm});
            skArc(sketch, "E1199", {"start": v(79.74, 122.12) * mm, "mid": v(79.55, 122.36) * mm, "end": v(79.35, 122.6) * mm});
            skArc(sketch, "E1200", {"start": v(79.74, 122.12) * mm, "mid": v(80.24, 121.82) * mm, "end": v(80.81, 121.92) * mm});
            skLineSegment(sketch, "E1201", {"start": v(84.05, 122.64) * mm, "end": v(84.7, 122.47) * mm});
            skLineSegment(sketch, "E1202", {"start": v(83.43, 122.72) * mm, "end": v(84.05, 122.64) * mm});
            skLineSegment(sketch, "E1203", {"start": v(82.86, 122.74) * mm, "end": v(83.43, 122.72) * mm});
            skLineSegment(sketch, "E1204", {"start": v(82.36, 122.68) * mm, "end": v(82.86, 122.74) * mm});
            skLineSegment(sketch, "E1205", {"start": v(81.97, 122.58) * mm, "end": v(82.36, 122.68) * mm});
            skLineSegment(sketch, "E1206", {"start": v(-8.1, 111.44) * mm, "end": v(-8.28, 110.95) * mm});
            skCircle(sketch, "E1207", {"center": v(29.8, 149.62) * mm, "radius": 3.1 * mm});
            skLineSegment(sketch, "E1208", {"start": v(29.3, 73.41) * mm, "end": v(29.05, 73.13) * mm});
            skLineSegment(sketch, "E1209", {"start": v(81.86, 122.54) * mm, "end": v(81.97, 122.58) * mm});
            skLineSegment(sketch, "E1210", {"start": v(81.79, 122.5) * mm, "end": v(81.86, 122.54) * mm});
            skLineSegment(sketch, "E1211", {"start": v(81.61, 122.4) * mm, "end": v(81.79, 122.5) * mm});
            skLineSegment(sketch, "E1212", {"start": v(81.26, 122.19) * mm, "end": v(81.61, 122.4) * mm});
            skLineSegment(sketch, "E1213", {"start": v(80.81, 121.92) * mm, "end": v(81.26, 122.19) * mm});
            skArc(sketch, "E1214", {"start": v(85.09, 121.41) * mm, "mid": v(84.9, 121.95) * mm, "end": v(84.7, 122.47) * mm});
            skLineSegment(sketch, "E1215", {"start": v(84.7, 120.87) * mm, "end": v(85.09, 121.41) * mm});
            skLineSegment(sketch, "E1216", {"start": v(84.27, 120.4) * mm, "end": v(84.7, 120.87) * mm});
            skLineSegment(sketch, "E1217", {"start": v(83.84, 120.03) * mm, "end": v(84.27, 120.4) * mm});
            skLineSegment(sketch, "E1218", {"start": v(83.43, 119.75) * mm, "end": v(83.84, 120.03) * mm});
            skLineSegment(sketch, "E1219", {"start": v(83.07, 119.57) * mm, "end": v(83.43, 119.75) * mm});
            skLineSegment(sketch, "E1220", {"start": v(82.95, 119.54) * mm, "end": v(83.07, 119.57) * mm});
            skLineSegment(sketch, "E1221", {"start": v(82.87, 119.52) * mm, "end": v(82.95, 119.54) * mm});
            skLineSegment(sketch, "E1222", {"start": v(82.67, 119.49) * mm, "end": v(82.87, 119.52) * mm});
            skLineSegment(sketch, "E1223", {"start": v(82.27, 119.42) * mm, "end": v(82.67, 119.49) * mm});
            skLineSegment(sketch, "E1224", {"start": v(81.75, 119.34) * mm, "end": v(82.27, 119.42) * mm});
            skArc(sketch, "E1225", {"start": v(81.75, 119.34) * mm, "mid": v(81.24, 119.05) * mm, "end": v(81.06, 118.5) * mm});
            skArc(sketch, "E1226", {"start": v(81.06, 117.88) * mm, "mid": v(81.07, 118.19) * mm, "end": v(81.06, 118.5) * mm});
            skArc(sketch, "E1227", {"start": v(81.06, 117.88) * mm, "mid": v(81.24, 117.32) * mm, "end": v(81.75, 117.03) * mm});
            skLineSegment(sketch, "E1228", {"start": v(84.7, 115.5) * mm, "end": v(85.09, 114.96) * mm});
            skLineSegment(sketch, "E1229", {"start": v(84.27, 115.97) * mm, "end": v(84.7, 115.5) * mm});
            skLineSegment(sketch, "E1230", {"start": v(83.84, 116.35) * mm, "end": v(84.27, 115.97) * mm});
            skArc(sketch, "E1231", {"start": v(24.3, 149.92) * mm, "mid": v(24.3, 149.62) * mm, "end": v(24.3, 149.33) * mm});
            skLineSegment(sketch, "E1232", {"start": v(83.43, 116.63) * mm, "end": v(83.84, 116.35) * mm});
            skArc(sketch, "E1233", {"start": v(24.3, 149.92) * mm, "mid": v(24.13, 150.46) * mm, "end": v(23.64, 150.75) * mm});
            skLineSegment(sketch, "E1234", {"start": v(83.07, 116.8) * mm, "end": v(83.43, 116.63) * mm});
            skLineSegment(sketch, "E1235", {"start": v(20.72, 152.38) * mm, "end": v(20.36, 152.95) * mm});
            skLineSegment(sketch, "E1236", {"start": v(82.95, 116.83) * mm, "end": v(83.07, 116.8) * mm});
            skLineSegment(sketch, "E1237", {"start": v(21.1, 151.9) * mm, "end": v(20.72, 152.38) * mm});
            skLineSegment(sketch, "E1238", {"start": v(82.87, 116.85) * mm, "end": v(82.95, 116.83) * mm});
            skLineSegment(sketch, "E1239", {"start": v(21.5, 151.5) * mm, "end": v(21.1, 151.9) * mm});
            skLineSegment(sketch, "E1240", {"start": v(82.67, 116.88) * mm, "end": v(82.87, 116.85) * mm});
            skLineSegment(sketch, "E1241", {"start": v(21.9, 151.21) * mm, "end": v(21.5, 151.5) * mm});
            skLineSegment(sketch, "E1242", {"start": v(82.27, 116.95) * mm, "end": v(82.67, 116.88) * mm});
            skLineSegment(sketch, "E1243", {"start": v(22.25, 151.03) * mm, "end": v(21.9, 151.21) * mm});
            skLineSegment(sketch, "E1244", {"start": v(81.75, 117.03) * mm, "end": v(82.27, 116.95) * mm});
            skLineSegment(sketch, "E1245", {"start": v(22.32, 151) * mm, "end": v(22.25, 151.03) * mm});
            skArc(sketch, "E1246", {"start": v(84.7, 113.9) * mm, "mid": v(84.9, 114.42) * mm, "end": v(85.09, 114.96) * mm});
            skLineSegment(sketch, "E1247", {"start": v(22.37, 150.99) * mm, "end": v(22.32, 151) * mm});
            skLineSegment(sketch, "E1248", {"start": v(84.05, 113.73) * mm, "end": v(84.7, 113.9) * mm});
            skLineSegment(sketch, "E1249", {"start": v(22.44, 150.97) * mm, "end": v(22.37, 150.99) * mm});
            skLineSegment(sketch, "E1250", {"start": v(83.43, 113.65) * mm, "end": v(84.05, 113.73) * mm});
            skLineSegment(sketch, "E1251", {"start": v(22.65, 150.93) * mm, "end": v(22.44, 150.97) * mm});
            skLineSegment(sketch, "E1252", {"start": v(82.86, 113.63) * mm, "end": v(83.43, 113.65) * mm});
            skLineSegment(sketch, "E1253", {"start": v(23.08, 150.85) * mm, "end": v(22.65, 150.93) * mm});
            skLineSegment(sketch, "E1254", {"start": v(82.36, 113.69) * mm, "end": v(82.86, 113.63) * mm});
            skLineSegment(sketch, "E1255", {"start": v(23.64, 150.75) * mm, "end": v(23.08, 150.85) * mm});
            skLineSegment(sketch, "E1256", {"start": v(81.97, 113.79) * mm, "end": v(82.36, 113.69) * mm});
            skArc(sketch, "E1257", {"start": v(20.78, 153.94) * mm, "mid": v(20.56, 153.45) * mm, "end": v(20.36, 152.95) * mm});
            skLineSegment(sketch, "E1258", {"start": v(81.86, 113.83) * mm, "end": v(81.97, 113.79) * mm});
            skLineSegment(sketch, "E1259", {"start": v(21.42, 154.1) * mm, "end": v(20.78, 153.94) * mm});
            skArc(sketch, "E1260", {"start": v(36.14, 89) * mm, "mid": v(35.84, 89.1) * mm, "end": v(35.53, 89.2) * mm});
            skArc(sketch, "E1261", {"start": v(36.14, 89) * mm, "mid": v(36.73, 89) * mm, "end": v(37.17, 89.4) * mm});
            skLineSegment(sketch, "E1262", {"start": v(39.39, 91.74) * mm, "end": v(40.1, 92.01) * mm});
            skLineSegment(sketch, "E1263", {"start": v(38.78, 91.42) * mm, "end": v(39.39, 91.74) * mm});
            skLineSegment(sketch, "E1264", {"start": v(38.34, 91.12) * mm, "end": v(38.78, 91.42) * mm});
            skLineSegment(sketch, "E1265", {"start": v(37.99, 90.81) * mm, "end": v(38.34, 91.12) * mm});
            skLineSegment(sketch, "E1266", {"start": v(37.74, 90.53) * mm, "end": v(37.99, 90.81) * mm});
            skLineSegment(sketch, "E1267", {"start": v(37.68, 90.44) * mm, "end": v(37.74, 90.53) * mm});
            skLineSegment(sketch, "E1268", {"start": v(37.64, 90.36) * mm, "end": v(37.68, 90.44) * mm});
            skLineSegment(sketch, "E1269", {"start": v(37.55, 90.18) * mm, "end": v(37.64, 90.36) * mm});
            skLineSegment(sketch, "E1270", {"start": v(37.38, 89.84) * mm, "end": v(37.55, 90.18) * mm});
            skLineSegment(sketch, "E1271", {"start": v(37.17, 89.4) * mm, "end": v(37.38, 89.84) * mm});
            skArc(sketch, "E1272", {"start": v(41.04, 91.32) * mm, "mid": v(40.57, 91.68) * mm, "end": v(40.1, 92.01) * mm});
            skLineSegment(sketch, "E1273", {"start": v(41, 90.57) * mm, "end": v(41.04, 91.32) * mm});
            skLineSegment(sketch, "E1274", {"start": v(40.88, 89.9) * mm, "end": v(41, 90.57) * mm});
            skLineSegment(sketch, "E1275", {"start": v(40.73, 89.38) * mm, "end": v(40.88, 89.9) * mm});
            skLineSegment(sketch, "E1276", {"start": v(40.55, 88.95) * mm, "end": v(40.73, 89.38) * mm});
            skLineSegment(sketch, "E1277", {"start": v(40.36, 88.63) * mm, "end": v(40.55, 88.95) * mm});
            skLineSegment(sketch, "E1278", {"start": v(40.28, 88.54) * mm, "end": v(40.36, 88.63) * mm});
            skLineSegment(sketch, "E1279", {"start": v(40.22, 88.48) * mm, "end": v(40.28, 88.54) * mm});
            skLineSegment(sketch, "E1280", {"start": v(40.08, 88.34) * mm, "end": v(40.22, 88.48) * mm});
            skLineSegment(sketch, "E1281", {"start": v(39.81, 88.08) * mm, "end": v(40.08, 88.34) * mm});
            skLineSegment(sketch, "E1282", {"start": v(39.47, 87.74) * mm, "end": v(39.81, 88.08) * mm});
            skArc(sketch, "E1283", {"start": v(39.47, 87.74) * mm, "mid": v(39.22, 87.2) * mm, "end": v(39.4, 86.64) * mm});
            skArc(sketch, "E1284", {"start": v(39.77, 86.12) * mm, "mid": v(39.59, 86.38) * mm, "end": v(39.4, 86.64) * mm});
            skArc(sketch, "E1285", {"start": v(39.77, 86.12) * mm, "mid": v(40.25, 85.77) * mm, "end": v(40.84, 85.84) * mm});
            skLineSegment(sketch, "E1286", {"start": v(44.01, 86.42) * mm, "end": v(44.74, 86.23) * mm});
            skLineSegment(sketch, "E1287", {"start": v(43.33, 86.52) * mm, "end": v(44.01, 86.42) * mm});
            skLineSegment(sketch, "E1288", {"start": v(42.8, 86.54) * mm, "end": v(43.33, 86.52) * mm});
            skLineSegment(sketch, "E1289", {"start": v(42.33, 86.5) * mm, "end": v(42.8, 86.54) * mm});
            skLineSegment(sketch, "E1290", {"start": v(41.96, 86.42) * mm, "end": v(42.33, 86.5) * mm});
            skLineSegment(sketch, "E1291", {"start": v(41.86, 86.38) * mm, "end": v(41.96, 86.42) * mm});
            skLineSegment(sketch, "E1292", {"start": v(41.78, 86.34) * mm, "end": v(41.86, 86.38) * mm});
            skLineSegment(sketch, "E1293", {"start": v(41.6, 86.25) * mm, "end": v(41.78, 86.34) * mm});
            skLineSegment(sketch, "E1294", {"start": v(41.27, 86.07) * mm, "end": v(41.6, 86.25) * mm});
            skLineSegment(sketch, "E1295", {"start": v(40.84, 85.84) * mm, "end": v(41.27, 86.07) * mm});
            skArc(sketch, "E1296", {"start": v(45.1, 85.12) * mm, "mid": v(44.93, 85.68) * mm, "end": v(44.74, 86.23) * mm});
            skLineSegment(sketch, "E1297", {"start": v(44.62, 84.54) * mm, "end": v(45.1, 85.12) * mm});
            skLineSegment(sketch, "E1298", {"start": v(44.13, 84.05) * mm, "end": v(44.62, 84.54) * mm});
            skLineSegment(sketch, "E1299", {"start": v(43.7, 83.73) * mm, "end": v(44.13, 84.05) * mm});
            skLineSegment(sketch, "E1300", {"start": v(43.3, 83.49) * mm, "end": v(43.7, 83.73) * mm});
            skLineSegment(sketch, "E1301", {"start": v(42.96, 83.34) * mm, "end": v(43.3, 83.49) * mm});
            skLineSegment(sketch, "E1302", {"start": v(42.85, 83.3) * mm, "end": v(42.96, 83.34) * mm});
            skLineSegment(sketch, "E1303", {"start": v(42.77, 83.3) * mm, "end": v(42.85, 83.3) * mm});
            skLineSegment(sketch, "E1304", {"start": v(42.57, 83.27) * mm, "end": v(42.77, 83.3) * mm});
            skLineSegment(sketch, "E1305", {"start": v(42.2, 83.21) * mm, "end": v(42.57, 83.27) * mm});
            skLineSegment(sketch, "E1306", {"start": v(41.72, 83.14) * mm, "end": v(42.2, 83.21) * mm});
            skArc(sketch, "E1307", {"start": v(41.72, 83.14) * mm, "mid": v(41.2, 82.86) * mm, "end": v(41.01, 82.3) * mm});
            skArc(sketch, "E1308", {"start": v(41.01, 81.65) * mm, "mid": v(41.02, 81.97) * mm, "end": v(41.01, 82.3) * mm});
            skArc(sketch, "E1309", {"start": v(41.01, 81.65) * mm, "mid": v(41.2, 81.09) * mm, "end": v(41.72, 80.8) * mm});
            skLineSegment(sketch, "E1310", {"start": v(44.62, 79.4) * mm, "end": v(45.1, 78.83) * mm});
            skLineSegment(sketch, "E1311", {"start": v(44.13, 79.9) * mm, "end": v(44.62, 79.4) * mm});
            skLineSegment(sketch, "E1312", {"start": v(43.7, 80.22) * mm, "end": v(44.13, 79.9) * mm});
            skLineSegment(sketch, "E1313", {"start": v(43.3, 80.46) * mm, "end": v(43.7, 80.22) * mm});
            skLineSegment(sketch, "E1314", {"start": v(42.96, 80.6) * mm, "end": v(43.3, 80.46) * mm});
            skLineSegment(sketch, "E1315", {"start": v(42.85, 80.64) * mm, "end": v(42.96, 80.6) * mm});
            skLineSegment(sketch, "E1316", {"start": v(42.77, 80.65) * mm, "end": v(42.85, 80.64) * mm});
            skLineSegment(sketch, "E1317", {"start": v(42.57, 80.68) * mm, "end": v(42.77, 80.65) * mm});
            skLineSegment(sketch, "E1318", {"start": v(42.2, 80.73) * mm, "end": v(42.57, 80.68) * mm});
            skLineSegment(sketch, "E1319", {"start": v(41.72, 80.8) * mm, "end": v(42.2, 80.73) * mm});
            skArc(sketch, "E1320", {"start": v(44.74, 77.71) * mm, "mid": v(44.93, 78.26) * mm, "end": v(45.1, 78.83) * mm});
            skLineSegment(sketch, "E1321", {"start": v(44.01, 77.52) * mm, "end": v(44.74, 77.71) * mm});
            skLineSegment(sketch, "E1322", {"start": v(43.33, 77.42) * mm, "end": v(44.01, 77.52) * mm});
            skLineSegment(sketch, "E1323", {"start": v(42.8, 77.4) * mm, "end": v(43.33, 77.42) * mm});
            skLineSegment(sketch, "E1324", {"start": v(42.33, 77.45) * mm, "end": v(42.8, 77.4) * mm});
            skLineSegment(sketch, "E1325", {"start": v(41.96, 77.53) * mm, "end": v(42.33, 77.45) * mm});
            skLineSegment(sketch, "E1326", {"start": v(41.86, 77.57) * mm, "end": v(41.96, 77.53) * mm});
            skLineSegment(sketch, "E1327", {"start": v(41.78, 77.6) * mm, "end": v(41.86, 77.57) * mm});
            skLineSegment(sketch, "E1328", {"start": v(41.6, 77.7) * mm, "end": v(41.78, 77.6) * mm});
            skLineSegment(sketch, "E1329", {"start": v(41.27, 77.87) * mm, "end": v(41.6, 77.7) * mm});
            skLineSegment(sketch, "E1330", {"start": v(40.84, 78.1) * mm, "end": v(41.27, 77.87) * mm});
            skArc(sketch, "E1331", {"start": v(40.84, 78.1) * mm, "mid": v(40.25, 78.17) * mm, "end": v(39.77, 77.83) * mm});
            skArc(sketch, "E1332", {"start": v(39.4, 77.3) * mm, "mid": v(39.59, 77.56) * mm, "end": v(39.77, 77.83) * mm});
            skCircle(sketch, "E1333", {"center": v(33.52, 81.97) * mm, "radius": 3.1 * mm});
            skArc(sketch, "E1334", {"start": v(39.4, 77.3) * mm, "mid": v(39.22, 76.74) * mm, "end": v(39.47, 76.2) * mm});
            skLineSegment(sketch, "E1335", {"start": v(41, 73.37) * mm, "end": v(41.04, 72.62) * mm});
            skLineSegment(sketch, "E1336", {"start": v(40.88, 74.05) * mm, "end": v(41, 73.37) * mm});
            skLineSegment(sketch, "E1337", {"start": v(40.73, 74.56) * mm, "end": v(40.88, 74.05) * mm});
            skLineSegment(sketch, "E1338", {"start": v(40.55, 75) * mm, "end": v(40.73, 74.56) * mm});
            skLineSegment(sketch, "E1339", {"start": v(40.36, 75.31) * mm, "end": v(40.55, 75) * mm});
            skLineSegment(sketch, "E1340", {"start": v(40.28, 75.4) * mm, "end": v(40.36, 75.31) * mm});
            skLineSegment(sketch, "E1341", {"start": v(40.22, 75.47) * mm, "end": v(40.28, 75.4) * mm});
            skLineSegment(sketch, "E1342", {"start": v(40.08, 75.6) * mm, "end": v(40.22, 75.47) * mm});
            skLineSegment(sketch, "E1343", {"start": v(39.81, 75.87) * mm, "end": v(40.08, 75.6) * mm});
            skLineSegment(sketch, "E1344", {"start": v(39.47, 76.2) * mm, "end": v(39.81, 75.87) * mm});
            skArc(sketch, "E1345", {"start": v(40.1, 71.93) * mm, "mid": v(40.57, 72.26) * mm, "end": v(41.04, 72.62) * mm});
            skLineSegment(sketch, "E1346", {"start": v(39.39, 72.2) * mm, "end": v(40.1, 71.93) * mm});
            skLineSegment(sketch, "E1347", {"start": v(38.78, 72.53) * mm, "end": v(39.39, 72.2) * mm});
            skLineSegment(sketch, "E1348", {"start": v(38.34, 72.83) * mm, "end": v(38.78, 72.53) * mm});
            skLineSegment(sketch, "E1349", {"start": v(37.99, 73.13) * mm, "end": v(38.34, 72.83) * mm});
            skLineSegment(sketch, "E1350", {"start": v(37.74, 73.41) * mm, "end": v(37.99, 73.13) * mm});
            skLineSegment(sketch, "E1351", {"start": v(37.68, 73.5) * mm, "end": v(37.74, 73.41) * mm});
            skLineSegment(sketch, "E1352", {"start": v(37.64, 73.59) * mm, "end": v(37.68, 73.5) * mm});
            skLineSegment(sketch, "E1353", {"start": v(37.55, 73.76) * mm, "end": v(37.64, 73.59) * mm});
            skLineSegment(sketch, "E1354", {"start": v(37.38, 74.1) * mm, "end": v(37.55, 73.76) * mm});
            skLineSegment(sketch, "E1355", {"start": v(37.17, 74.54) * mm, "end": v(37.38, 74.1) * mm});
            skArc(sketch, "E1356", {"start": v(37.17, 74.54) * mm, "mid": v(36.73, 74.94) * mm, "end": v(36.14, 74.95) * mm});
            skArc(sketch, "E1357", {"start": v(35.53, 74.75) * mm, "mid": v(35.84, 74.84) * mm, "end": v(36.14, 74.95) * mm});
            skArc(sketch, "E1358", {"start": v(35.53, 74.75) * mm, "mid": v(35.05, 74.4) * mm, "end": v(34.94, 73.81) * mm});
            skLineSegment(sketch, "E1359", {"start": v(34.51, 70.62) * mm, "end": v(34.1, 69.99) * mm});
            skLineSegment(sketch, "E1360", {"start": v(34.82, 71.24) * mm, "end": v(34.51, 70.62) * mm});
            skLineSegment(sketch, "E1361", {"start": v(35, 71.74) * mm, "end": v(34.82, 71.24) * mm});
            skLineSegment(sketch, "E1362", {"start": v(35.1, 72.2) * mm, "end": v(35, 71.74) * mm});
            skLineSegment(sketch, "E1363", {"start": v(35.14, 72.57) * mm, "end": v(35.1, 72.2) * mm});
            skLineSegment(sketch, "E1364", {"start": v(35.13, 72.68) * mm, "end": v(35.14, 72.57) * mm});
            skLineSegment(sketch, "E1365", {"start": v(35.12, 72.77) * mm, "end": v(35.13, 72.68) * mm});
            skLineSegment(sketch, "E1366", {"start": v(35.09, 72.96) * mm, "end": v(35.12, 72.77) * mm});
            skLineSegment(sketch, "E1367", {"start": v(35.02, 73.34) * mm, "end": v(35.09, 72.96) * mm});
            skLineSegment(sketch, "E1368", {"start": v(34.94, 73.81) * mm, "end": v(35.02, 73.34) * mm});
            skArc(sketch, "E1369", {"start": v(32.93, 69.99) * mm, "mid": v(33.52, 69.97) * mm, "end": v(34.1, 69.99) * mm});
            skLineSegment(sketch, "E1370", {"start": v(32.53, 70.62) * mm, "end": v(32.93, 69.99) * mm});
            skLineSegment(sketch, "E1371", {"start": v(32.22, 71.24) * mm, "end": v(32.53, 70.62) * mm});
            skLineSegment(sketch, "E1372", {"start": v(32.04, 71.74) * mm, "end": v(32.22, 71.24) * mm});
            skLineSegment(sketch, "E1373", {"start": v(31.94, 72.2) * mm, "end": v(32.04, 71.74) * mm});
            skLineSegment(sketch, "E1374", {"start": v(31.9, 72.57) * mm, "end": v(31.94, 72.2) * mm});
            skLineSegment(sketch, "E1375", {"start": v(31.9, 72.68) * mm, "end": v(31.9, 72.57) * mm});
            skLineSegment(sketch, "E1376", {"start": v(31.92, 72.77) * mm, "end": v(31.9, 72.68) * mm});
            skLineSegment(sketch, "E1377", {"start": v(31.95, 72.96) * mm, "end": v(31.92, 72.77) * mm});
            skLineSegment(sketch, "E1378", {"start": v(32.02, 73.34) * mm, "end": v(31.95, 72.96) * mm});
            skLineSegment(sketch, "E1379", {"start": v(32.1, 73.81) * mm, "end": v(32.02, 73.34) * mm});
            skArc(sketch, "E1380", {"start": v(32.1, 73.81) * mm, "mid": v(31.99, 74.4) * mm, "end": v(31.51, 74.75) * mm});
            skArc(sketch, "E1381", {"start": v(30.9, 74.95) * mm, "mid": v(31.2, 74.84) * mm, "end": v(31.51, 74.75) * mm});
            skArc(sketch, "E1382", {"start": v(30.9, 74.95) * mm, "mid": v(30.3, 74.94) * mm, "end": v(29.87, 74.54) * mm});
            skLineSegment(sketch, "E1383", {"start": v(27.65, 72.2) * mm, "end": v(26.95, 71.93) * mm});
            skLineSegment(sketch, "E1384", {"start": v(28.26, 72.53) * mm, "end": v(27.65, 72.2) * mm});
            skLineSegment(sketch, "E1385", {"start": v(28.7, 72.83) * mm, "end": v(28.26, 72.53) * mm});
            skLineSegment(sketch, "E1386", {"start": v(29.05, 73.13) * mm, "end": v(28.7, 72.83) * mm});
            skLineSegment(sketch, "E1387", {"start": v(29.36, 73.5) * mm, "end": v(29.3, 73.41) * mm});
            skLineSegment(sketch, "E1388", {"start": v(29.4, 73.59) * mm, "end": v(29.36, 73.5) * mm});
            skLineSegment(sketch, "E1389", {"start": v(29.5, 73.76) * mm, "end": v(29.4, 73.59) * mm});
            skLineSegment(sketch, "E1390", {"start": v(29.66, 74.1) * mm, "end": v(29.5, 73.76) * mm});
            skLineSegment(sketch, "E1391", {"start": v(29.87, 74.54) * mm, "end": v(29.66, 74.1) * mm});
            skArc(sketch, "E1392", {"start": v(26, 72.62) * mm, "mid": v(26.47, 72.26) * mm, "end": v(26.95, 71.93) * mm});
            skLineSegment(sketch, "E1393", {"start": v(26.04, 73.37) * mm, "end": v(26, 72.62) * mm});
            skLineSegment(sketch, "E1394", {"start": v(26.16, 74.05) * mm, "end": v(26.04, 73.37) * mm});
            skLineSegment(sketch, "E1395", {"start": v(26.31, 74.56) * mm, "end": v(26.16, 74.05) * mm});
            skLineSegment(sketch, "E1396", {"start": v(26.5, 75) * mm, "end": v(26.31, 74.56) * mm});
            skLineSegment(sketch, "E1397", {"start": v(26.68, 75.31) * mm, "end": v(26.5, 75) * mm});
            skLineSegment(sketch, "E1398", {"start": v(26.76, 75.4) * mm, "end": v(26.68, 75.31) * mm});
            skLineSegment(sketch, "E1399", {"start": v(26.82, 75.47) * mm, "end": v(26.76, 75.4) * mm});
            skLineSegment(sketch, "E1400", {"start": v(26.96, 75.6) * mm, "end": v(26.82, 75.47) * mm});
            skLineSegment(sketch, "E1401", {"start": v(27.23, 75.87) * mm, "end": v(26.96, 75.6) * mm});
            skLineSegment(sketch, "E1402", {"start": v(27.57, 76.2) * mm, "end": v(27.23, 75.87) * mm});
            skArc(sketch, "E1403", {"start": v(27.57, 76.2) * mm, "mid": v(27.82, 76.74) * mm, "end": v(27.65, 77.3) * mm});
            skArc(sketch, "E1404", {"start": v(27.27, 77.83) * mm, "mid": v(27.45, 77.56) * mm, "end": v(27.65, 77.3) * mm});
            skArc(sketch, "E1405", {"start": v(27.27, 77.83) * mm, "mid": v(26.79, 78.17) * mm, "end": v(26.2, 78.1) * mm});
            skLineSegment(sketch, "E1406", {"start": v(23.03, 77.52) * mm, "end": v(22.3, 77.71) * mm});
            skLineSegment(sketch, "E1407", {"start": v(23.71, 77.42) * mm, "end": v(23.03, 77.52) * mm});
            skLineSegment(sketch, "E1408", {"start": v(24.25, 77.4) * mm, "end": v(23.71, 77.42) * mm});
            skLineSegment(sketch, "E1409", {"start": v(24.71, 77.45) * mm, "end": v(24.25, 77.4) * mm});
            skLineSegment(sketch, "E1410", {"start": v(25.08, 77.53) * mm, "end": v(24.71, 77.45) * mm});
            skLineSegment(sketch, "E1411", {"start": v(25.18, 77.57) * mm, "end": v(25.08, 77.53) * mm});
            skLineSegment(sketch, "E1412", {"start": v(25.26, 77.6) * mm, "end": v(25.18, 77.57) * mm});
            skLineSegment(sketch, "E1413", {"start": v(-6.74, 90.78) * mm, "end": v(-6.74, 90.9) * mm});
            skLineSegment(sketch, "E1414", {"start": v(-6.74, 90.9) * mm, "end": v(-6.77, 91.26) * mm});
            skLineSegment(sketch, "E1415", {"start": v(-6.77, 91.26) * mm, "end": v(-6.88, 91.72) * mm});
            skLineSegment(sketch, "E1416", {"start": v(-6.88, 91.72) * mm, "end": v(-7.06, 92.22) * mm});
            skLineSegment(sketch, "E1417", {"start": v(-7.06, 92.22) * mm, "end": v(-7.36, 92.84) * mm});
            skLineSegment(sketch, "E1418", {"start": v(-7.36, 92.84) * mm, "end": v(-7.77, 93.47) * mm});
            skArc(sketch, "E1419", {"start": v(-7.77, 93.47) * mm, "mid": v(-8.35, 93.49) * mm, "end": v(-8.94, 93.47) * mm});
            skLineSegment(sketch, "E1420", {"start": v(-9.77, 89.65) * mm, "end": v(-9.86, 90.12) * mm});
            skLineSegment(sketch, "E1421", {"start": v(-9.86, 90.12) * mm, "end": v(-9.92, 90.5) * mm});
            skLineSegment(sketch, "E1422", {"start": v(-9.92, 90.5) * mm, "end": v(-9.95, 90.69) * mm});
            skLineSegment(sketch, "E1423", {"start": v(-9.95, 90.69) * mm, "end": v(-9.97, 90.78) * mm});
            skLineSegment(sketch, "E1424", {"start": v(-9.97, 90.78) * mm, "end": v(-9.97, 90.9) * mm});
            skLineSegment(sketch, "E1425", {"start": v(-9.97, 90.9) * mm, "end": v(-9.94, 91.26) * mm});
            skLineSegment(sketch, "E1426", {"start": v(-9.94, 91.26) * mm, "end": v(-9.83, 91.72) * mm});
            skLineSegment(sketch, "E1427", {"start": v(-9.83, 91.72) * mm, "end": v(-9.65, 92.22) * mm});
            skLineSegment(sketch, "E1428", {"start": v(-9.65, 92.22) * mm, "end": v(-9.35, 92.84) * mm});
            skLineSegment(sketch, "E1429", {"start": v(-9.35, 92.84) * mm, "end": v(-8.94, 93.47) * mm});
            skArc(sketch, "E1430", {"start": v(-10.36, 88.71) * mm, "mid": v(-9.89, 89.07) * mm, "end": v(-9.77, 89.65) * mm});
            skArc(sketch, "E1431", {"start": v(-10.36, 88.71) * mm, "mid": v(-10.67, 88.62) * mm, "end": v(-10.97, 88.51) * mm});
            skArc(sketch, "E1432", {"start": v(-12, 88.92) * mm, "mid": v(-11.57, 88.52) * mm, "end": v(-10.97, 88.51) * mm});
            skLineSegment(sketch, "E1433", {"start": v(-12, 88.92) * mm, "end": v(-12.21, 89.36) * mm});
            skLineSegment(sketch, "E1434", {"start": v(-12.21, 89.36) * mm, "end": v(-12.38, 89.7) * mm});
            skLineSegment(sketch, "E1435", {"start": v(-12.38, 89.7) * mm, "end": v(-12.47, 89.87) * mm});
            skLineSegment(sketch, "E1436", {"start": v(-12.47, 89.87) * mm, "end": v(-12.5, 89.95) * mm});
            skLineSegment(sketch, "E1437", {"start": v(-12.5, 89.95) * mm, "end": v(-12.57, 90.05) * mm});
            skLineSegment(sketch, "E1438", {"start": v(-12.57, 90.05) * mm, "end": v(-12.82, 90.33) * mm});
            skLineSegment(sketch, "E1439", {"start": v(-12.82, 90.33) * mm, "end": v(-13.17, 90.63) * mm});
            skLineSegment(sketch, "E1440", {"start": v(-13.17, 90.63) * mm, "end": v(-13.61, 90.93) * mm});
            skLineSegment(sketch, "E1441", {"start": v(-13.61, 90.93) * mm, "end": v(-14.22, 91.26) * mm});
            skLineSegment(sketch, "E1442", {"start": v(-14.22, 91.26) * mm, "end": v(-14.92, 91.53) * mm});
            skArc(sketch, "E1443", {"start": v(-14.92, 91.53) * mm, "mid": v(-15.4, 91.2) * mm, "end": v(-15.87, 90.84) * mm});
            skLineSegment(sketch, "E1444", {"start": v(-14.3, 87.26) * mm, "end": v(-14.65, 87.6) * mm});
            skLineSegment(sketch, "E1445", {"start": v(-14.65, 87.6) * mm, "end": v(-14.92, 87.85) * mm});
            skLineSegment(sketch, "E1446", {"start": v(-14.92, 87.85) * mm, "end": v(-15.06, 88) * mm});
            skLineSegment(sketch, "E1447", {"start": v(-15.06, 88) * mm, "end": v(-15.12, 88.05) * mm});
            skLineSegment(sketch, "E1448", {"start": v(-15.12, 88.05) * mm, "end": v(-15.19, 88.15) * mm});
            skLineSegment(sketch, "E1449", {"start": v(-15.19, 88.15) * mm, "end": v(-15.38, 88.47) * mm});
            skLineSegment(sketch, "E1450", {"start": v(-15.38, 88.47) * mm, "end": v(-15.56, 88.9) * mm});
            skLineSegment(sketch, "E1451", {"start": v(-15.56, 88.9) * mm, "end": v(-15.71, 89.4) * mm});
            skLineSegment(sketch, "E1452", {"start": v(-15.71, 89.4) * mm, "end": v(-15.83, 90.09) * mm});
            skLineSegment(sketch, "E1453", {"start": v(-15.83, 90.09) * mm, "end": v(-15.87, 90.84) * mm});
            skArc(sketch, "E1454", {"start": v(-14.23, 86.15) * mm, "mid": v(-14.05, 86.72) * mm, "end": v(-14.3, 87.26) * mm});
            skArc(sketch, "E1455", {"start": v(-14.23, 86.15) * mm, "mid": v(-14.42, 85.9) * mm, "end": v(-14.6, 85.63) * mm});
            skArc(sketch, "E1456", {"start": v(-15.68, 85.36) * mm, "mid": v(-15.09, 85.29) * mm, "end": v(-14.6, 85.63) * mm});
            skLineSegment(sketch, "E1457", {"start": v(-15.68, 85.36) * mm, "end": v(-16.1, 85.59) * mm});
            skLineSegment(sketch, "E1458", {"start": v(-16.1, 85.59) * mm, "end": v(-16.44, 85.76) * mm});
            skLineSegment(sketch, "E1459", {"start": v(-16.44, 85.76) * mm, "end": v(-16.61, 85.85) * mm});
            skLineSegment(sketch, "E1460", {"start": v(-16.61, 85.85) * mm, "end": v(-16.69, 85.9) * mm});
            skLineSegment(sketch, "E1461", {"start": v(-16.69, 85.9) * mm, "end": v(-16.8, 85.93) * mm});
            skLineSegment(sketch, "E1462", {"start": v(-16.8, 85.93) * mm, "end": v(-17.16, 86.01) * mm});
            skLineSegment(sketch, "E1463", {"start": v(-17.16, 86.01) * mm, "end": v(-17.63, 86.05) * mm});
            skLineSegment(sketch, "E1464", {"start": v(-17.63, 86.05) * mm, "end": v(-18.16, 86.04) * mm});
            skLineSegment(sketch, "E1465", {"start": v(-18.16, 86.04) * mm, "end": v(-18.84, 85.94) * mm});
            skLineSegment(sketch, "E1466", {"start": v(-18.84, 85.94) * mm, "end": v(-19.57, 85.75) * mm});
            skArc(sketch, "E1467", {"start": v(-19.57, 85.75) * mm, "mid": v(-19.77, 85.2) * mm, "end": v(-19.93, 84.63) * mm});
            skLineSegment(sketch, "E1468", {"start": v(-16.55, 82.66) * mm, "end": v(-17.03, 82.73) * mm});
            skLineSegment(sketch, "E1469", {"start": v(-17.03, 82.73) * mm, "end": v(-17.4, 82.78) * mm});
            skLineSegment(sketch, "E1470", {"start": v(-17.4, 82.78) * mm, "end": v(-17.6, 82.81) * mm});
            skLineSegment(sketch, "E1471", {"start": v(-17.6, 82.81) * mm, "end": v(-17.69, 82.82) * mm});
            skLineSegment(sketch, "E1472", {"start": v(-17.69, 82.82) * mm, "end": v(-17.8, 82.86) * mm});
            skLineSegment(sketch, "E1473", {"start": v(-17.8, 82.86) * mm, "end": v(-18.14, 83) * mm});
            skLineSegment(sketch, "E1474", {"start": v(-18.14, 83) * mm, "end": v(-18.54, 83.24) * mm});
            skLineSegment(sketch, "E1475", {"start": v(-18.54, 83.24) * mm, "end": v(-18.96, 83.57) * mm});
            skLineSegment(sketch, "E1476", {"start": v(-18.96, 83.57) * mm, "end": v(-19.46, 84.05) * mm});
            skLineSegment(sketch, "E1477", {"start": v(-19.46, 84.05) * mm, "end": v(-19.93, 84.63) * mm});
            skArc(sketch, "E1478", {"start": v(-15.85, 81.8) * mm, "mid": v(-16.04, 82.37) * mm, "end": v(-16.55, 82.66) * mm});
            skArc(sketch, "E1479", {"start": v(-15.85, 81.8) * mm, "mid": v(-15.85, 81.49) * mm, "end": v(-15.85, 81.17) * mm});
            skArc(sketch, "E1480", {"start": v(-16.55, 80.32) * mm, "mid": v(-16.04, 80.6) * mm, "end": v(-15.85, 81.17) * mm});
            skLineSegment(sketch, "E1481", {"start": v(-16.55, 80.32) * mm, "end": v(-17.03, 80.25) * mm});
            skLineSegment(sketch, "E1482", {"start": v(-17.03, 80.25) * mm, "end": v(-17.4, 80.2) * mm});
            skLineSegment(sketch, "E1483", {"start": v(-17.4, 80.2) * mm, "end": v(-17.6, 80.16) * mm});
            skLineSegment(sketch, "E1484", {"start": v(-17.6, 80.16) * mm, "end": v(-17.69, 80.15) * mm});
            skLineSegment(sketch, "E1485", {"start": v(-17.69, 80.15) * mm, "end": v(-17.8, 80.12) * mm});
            skLineSegment(sketch, "E1486", {"start": v(-17.8, 80.12) * mm, "end": v(-18.14, 79.97) * mm});
            skLineSegment(sketch, "E1487", {"start": v(-18.14, 79.97) * mm, "end": v(-18.54, 79.73) * mm});
            skLineSegment(sketch, "E1488", {"start": v(-18.54, 79.73) * mm, "end": v(-18.96, 79.4) * mm});
            skLineSegment(sketch, "E1489", {"start": v(-18.96, 79.4) * mm, "end": v(-19.46, 78.92) * mm});
            skLineSegment(sketch, "E1490", {"start": v(-19.46, 78.92) * mm, "end": v(-19.93, 78.34) * mm});
            skArc(sketch, "E1491", {"start": v(-19.93, 78.34) * mm, "mid": v(-19.77, 77.78) * mm, "end": v(-19.57, 77.23) * mm});
            skLineSegment(sketch, "E1492", {"start": v(-15.68, 77.62) * mm, "end": v(-16.1, 77.39) * mm});
            skLineSegment(sketch, "E1493", {"start": v(-16.1, 77.39) * mm, "end": v(-16.44, 77.21) * mm});
            skLineSegment(sketch, "E1494", {"start": v(-16.44, 77.21) * mm, "end": v(-16.61, 77.12) * mm});
            skLineSegment(sketch, "E1495", {"start": v(-16.61, 77.12) * mm, "end": v(-16.69, 77.08) * mm});
            skLineSegment(sketch, "E1496", {"start": v(-16.69, 77.08) * mm, "end": v(-16.8, 77.04) * mm});
            skLineSegment(sketch, "E1497", {"start": v(-16.8, 77.04) * mm, "end": v(-17.16, 76.96) * mm});
            skLineSegment(sketch, "E1498", {"start": v(-17.16, 76.96) * mm, "end": v(-17.63, 76.92) * mm});
            skLineSegment(sketch, "E1499", {"start": v(-17.63, 76.92) * mm, "end": v(-18.16, 76.94) * mm});
            skLineSegment(sketch, "E1500", {"start": v(-18.16, 76.94) * mm, "end": v(-18.84, 77.04) * mm});
            skLineSegment(sketch, "E1501", {"start": v(-18.84, 77.04) * mm, "end": v(-19.57, 77.23) * mm});
            skArc(sketch, "E1502", {"start": v(-14.6, 77.34) * mm, "mid": v(-15.09, 77.69) * mm, "end": v(-15.68, 77.62) * mm});
            skArc(sketch, "E1503", {"start": v(-14.6, 77.34) * mm, "mid": v(-14.42, 77.08) * mm, "end": v(-14.23, 76.82) * mm});
            skArc(sketch, "E1504", {"start": v(-14.3, 75.72) * mm, "mid": v(-14.05, 76.26) * mm, "end": v(-14.23, 76.82) * mm});
            skLineSegment(sketch, "E1505", {"start": v(-14.3, 75.72) * mm, "end": v(-14.65, 75.38) * mm});
            skLineSegment(sketch, "E1506", {"start": v(-14.65, 75.38) * mm, "end": v(-14.92, 75.12) * mm});
            skLineSegment(sketch, "E1507", {"start": v(-14.92, 75.12) * mm, "end": v(-15.06, 74.98) * mm});
            skLineSegment(sketch, "E1508", {"start": v(-15.06, 74.98) * mm, "end": v(-15.12, 74.92) * mm});
            skLineSegment(sketch, "E1509", {"start": v(-15.12, 74.92) * mm, "end": v(-15.19, 74.83) * mm});
            skLineSegment(sketch, "E1510", {"start": v(-15.19, 74.83) * mm, "end": v(-15.38, 74.5) * mm});
            skLineSegment(sketch, "E1511", {"start": v(-15.38, 74.5) * mm, "end": v(-15.56, 74.08) * mm});
            skLineSegment(sketch, "E1512", {"start": v(-15.56, 74.08) * mm, "end": v(-15.71, 73.57) * mm});
            skLineSegment(sketch, "E1513", {"start": v(-15.71, 73.57) * mm, "end": v(-15.83, 72.89) * mm});
            skLineSegment(sketch, "E1514", {"start": v(-15.83, 72.89) * mm, "end": v(-15.87, 72.14) * mm});
            skArc(sketch, "E1515", {"start": v(-15.87, 72.14) * mm, "mid": v(-15.4, 71.78) * mm, "end": v(-14.92, 71.45) * mm});
            skLineSegment(sketch, "E1516", {"start": v(-12, 74.05) * mm, "end": v(-12.21, 73.62) * mm});
            skLineSegment(sketch, "E1517", {"start": v(-12.21, 73.62) * mm, "end": v(-12.38, 73.28) * mm});
            skLineSegment(sketch, "E1518", {"start": v(-12.38, 73.28) * mm, "end": v(-12.47, 73.1) * mm});
            skLineSegment(sketch, "E1519", {"start": v(-12.47, 73.1) * mm, "end": v(-12.5, 73.02) * mm});
            skLineSegment(sketch, "E1520", {"start": v(-12.5, 73.02) * mm, "end": v(-12.57, 72.93) * mm});
            skLineSegment(sketch, "E1521", {"start": v(-12.57, 72.93) * mm, "end": v(-12.82, 72.65) * mm});
            skLineSegment(sketch, "E1522", {"start": v(-12.82, 72.65) * mm, "end": v(-13.17, 72.34) * mm});
            skLineSegment(sketch, "E1523", {"start": v(-13.17, 72.34) * mm, "end": v(-13.61, 72.04) * mm});
            skLineSegment(sketch, "E1524", {"start": v(-13.61, 72.04) * mm, "end": v(-14.22, 71.72) * mm});
            skLineSegment(sketch, "E1525", {"start": v(-14.22, 71.72) * mm, "end": v(-14.92, 71.45) * mm});
            skArc(sketch, "E1526", {"start": v(-10.97, 74.46) * mm, "mid": v(-11.57, 74.45) * mm, "end": v(-12, 74.05) * mm});
            skCircle(sketch, "E1527", {"center": v(74.57, 118.19) * mm, "radius": 3.1 * mm});
            skArc(sketch, "E1528", {"start": v(-10.97, 74.46) * mm, "mid": v(-10.67, 74.35) * mm, "end": v(-10.36, 74.26) * mm});
            skArc(sketch, "E1529", {"start": v(-9.77, 73.33) * mm, "mid": v(-9.89, 73.9) * mm, "end": v(-10.36, 74.26) * mm});
            skLineSegment(sketch, "E1530", {"start": v(-9.77, 73.33) * mm, "end": v(-9.86, 72.85) * mm});
            skLineSegment(sketch, "E1531", {"start": v(-9.86, 72.85) * mm, "end": v(-9.92, 72.48) * mm});
            skLineSegment(sketch, "E1532", {"start": v(-9.92, 72.48) * mm, "end": v(-9.95, 72.29) * mm});
            skLineSegment(sketch, "E1533", {"start": v(-9.95, 72.29) * mm, "end": v(-9.97, 72.2) * mm});
            skLineSegment(sketch, "E1534", {"start": v(-9.97, 72.2) * mm, "end": v(-9.97, 72.08) * mm});
            skLineSegment(sketch, "E1535", {"start": v(-9.97, 72.08) * mm, "end": v(-9.94, 71.71) * mm});
            skLineSegment(sketch, "E1536", {"start": v(-9.94, 71.71) * mm, "end": v(-9.83, 71.26) * mm});
            skLineSegment(sketch, "E1537", {"start": v(-9.83, 71.26) * mm, "end": v(-9.65, 70.76) * mm});
            skLineSegment(sketch, "E1538", {"start": v(-9.65, 70.76) * mm, "end": v(-9.35, 70.13) * mm});
            skLineSegment(sketch, "E1539", {"start": v(-9.35, 70.13) * mm, "end": v(-8.94, 69.5) * mm});
            skArc(sketch, "E1540", {"start": v(-8.94, 69.5) * mm, "mid": v(-8.35, 69.49) * mm, "end": v(-7.77, 69.5) * mm});
            skLineSegment(sketch, "E1541", {"start": v(-6.93, 73.33) * mm, "end": v(-6.85, 72.85) * mm});
            skLineSegment(sketch, "E1542", {"start": v(-6.85, 72.85) * mm, "end": v(-6.79, 72.48) * mm});
            skLineSegment(sketch, "E1543", {"start": v(-6.79, 72.48) * mm, "end": v(-6.75, 72.29) * mm});
            skLineSegment(sketch, "E1544", {"start": v(-6.75, 72.29) * mm, "end": v(-6.74, 72.2) * mm});
            skLineSegment(sketch, "E1545", {"start": v(-6.74, 72.2) * mm, "end": v(-6.74, 72.08) * mm});
            skLineSegment(sketch, "E1546", {"start": v(-6.74, 72.08) * mm, "end": v(-6.77, 71.71) * mm});
            skLineSegment(sketch, "E1547", {"start": v(-6.77, 71.71) * mm, "end": v(-6.88, 71.26) * mm});
            skLineSegment(sketch, "E1548", {"start": v(-6.88, 71.26) * mm, "end": v(-7.06, 70.76) * mm});
            skLineSegment(sketch, "E1549", {"start": v(-7.06, 70.76) * mm, "end": v(-7.36, 70.13) * mm});
            skCircle(sketch, "E1550", {"center": v(33.47, 119.85) * mm, "radius": 3.1 * mm});
            skCircle(sketch, "E1551", {"center": v(-8.35, 81.49) * mm, "radius": 3.1 * mm});
            skArc(sketch, "E1552", {"start": v(113.15, 114.02) * mm, "mid": v(112.77, 114.47) * mm, "end": v(112.2, 114.55) * mm});
            skLineSegment(sketch, "E1553", {"start": v(113.15, 114.02) * mm, "end": v(113.32, 113.52) * mm});
            skLineSegment(sketch, "E1554", {"start": v(113.32, 113.52) * mm, "end": v(113.45, 113.14) * mm});
            skLineSegment(sketch, "E1555", {"start": v(113.45, 113.14) * mm, "end": v(113.52, 112.95) * mm});
            skLineSegment(sketch, "E1556", {"start": v(113.52, 112.95) * mm, "end": v(113.55, 112.87) * mm});
            skLineSegment(sketch, "E1557", {"start": v(113.55, 112.87) * mm, "end": v(113.6, 112.77) * mm});
            skLineSegment(sketch, "E1558", {"start": v(113.6, 112.77) * mm, "end": v(113.84, 112.44) * mm});
            skLineSegment(sketch, "E1559", {"start": v(113.84, 112.44) * mm, "end": v(114.19, 112.08) * mm});
            skLineSegment(sketch, "E1560", {"start": v(114.19, 112.08) * mm, "end": v(114.63, 111.72) * mm});
            skLineSegment(sketch, "E1561", {"start": v(114.63, 111.72) * mm, "end": v(115.16, 111.4) * mm});
            skLineSegment(sketch, "E1562", {"start": v(115.16, 111.4) * mm, "end": v(115.77, 111.1) * mm});
            skArc(sketch, "E1563", {"start": v(115.77, 111.1) * mm, "mid": v(116.26, 111.37) * mm, "end": v(116.75, 111.66) * mm});
            skLineSegment(sketch, "E1564", {"start": v(115.52, 115.4) * mm, "end": v(115.87, 115) * mm});
            skLineSegment(sketch, "E1565", {"start": v(115.87, 115) * mm, "end": v(116.13, 114.69) * mm});
            skLineSegment(sketch, "E1566", {"start": v(116.13, 114.69) * mm, "end": v(116.27, 114.53) * mm});
            skLineSegment(sketch, "E1567", {"start": v(116.27, 114.53) * mm, "end": v(116.32, 114.47) * mm});
            skLineSegment(sketch, "E1568", {"start": v(116.32, 114.47) * mm, "end": v(116.38, 114.37) * mm});
            skLineSegment(sketch, "E1569", {"start": v(116.38, 114.37) * mm, "end": v(116.55, 114) * mm});
            skLineSegment(sketch, "E1570", {"start": v(116.55, 114) * mm, "end": v(116.69, 113.52) * mm});
            skLineSegment(sketch, "E1571", {"start": v(116.69, 113.52) * mm, "end": v(116.77, 112.96) * mm});
            skLineSegment(sketch, "E1572", {"start": v(116.77, 112.96) * mm, "end": v(116.8, 112.33) * mm});
            skLineSegment(sketch, "E1573", {"start": v(116.8, 112.33) * mm, "end": v(116.75, 111.66) * mm});
            skArc(sketch, "E1574", {"start": v(115.54, 116.48) * mm, "mid": v(115.32, 115.94) * mm, "end": v(115.52, 115.4) * mm});
            skArc(sketch, "E1575", {"start": v(115.54, 116.48) * mm, "mid": v(115.74, 116.71) * mm, "end": v(115.94, 116.96) * mm});
            skArc(sketch, "E1576", {"start": v(117, 117.16) * mm, "mid": v(116.43, 117.26) * mm, "end": v(115.94, 116.96) * mm});
            skLineSegment(sketch, "E1577", {"start": v(117, 117.16) * mm, "end": v(117.46, 116.9) * mm});
            skLineSegment(sketch, "E1578", {"start": v(117.46, 116.9) * mm, "end": v(117.8, 116.68) * mm});
            skLineSegment(sketch, "E1579", {"start": v(117.8, 116.68) * mm, "end": v(117.98, 116.58) * mm});
            skLineSegment(sketch, "E1580", {"start": v(117.98, 116.58) * mm, "end": v(118.05, 116.54) * mm});
            skLineSegment(sketch, "E1581", {"start": v(118.05, 116.54) * mm, "end": v(118.16, 116.5) * mm});
            skLineSegment(sketch, "E1582", {"start": v(118.16, 116.5) * mm, "end": v(118.55, 116.4) * mm});
            skLineSegment(sketch, "E1583", {"start": v(118.55, 116.4) * mm, "end": v(119.05, 116.34) * mm});
            skLineSegment(sketch, "E1584", {"start": v(119.05, 116.34) * mm, "end": v(119.62, 116.36) * mm});
            skLineSegment(sketch, "E1585", {"start": v(119.62, 116.36) * mm, "end": v(120.24, 116.44) * mm});
            skLineSegment(sketch, "E1586", {"start": v(120.24, 116.44) * mm, "end": v(120.9, 116.6) * mm});
            skArc(sketch, "E1587", {"start": v(120.9, 116.6) * mm, "mid": v(121.1, 117.13) * mm, "end": v(121.28, 117.67) * mm});
            skLineSegment(sketch, "E1588", {"start": v(117.95, 119.74) * mm, "end": v(118.46, 119.66) * mm});
            skLineSegment(sketch, "E1589", {"start": v(118.46, 119.66) * mm, "end": v(118.87, 119.6) * mm});
            skLineSegment(sketch, "E1590", {"start": v(118.87, 119.6) * mm, "end": v(119.07, 119.56) * mm});
            skLineSegment(sketch, "E1591", {"start": v(119.07, 119.56) * mm, "end": v(119.15, 119.54) * mm});
            skLineSegment(sketch, "E1592", {"start": v(119.15, 119.54) * mm, "end": v(119.26, 119.5) * mm});
            skLineSegment(sketch, "E1593", {"start": v(119.26, 119.5) * mm, "end": v(119.62, 119.33) * mm});
            skLineSegment(sketch, "E1594", {"start": v(119.62, 119.33) * mm, "end": v(120.04, 119.05) * mm});
            skLineSegment(sketch, "E1595", {"start": v(120.04, 119.05) * mm, "end": v(120.47, 118.68) * mm});
            skLineSegment(sketch, "E1596", {"start": v(120.47, 118.68) * mm, "end": v(120.89, 118.21) * mm});
            skLineSegment(sketch, "E1597", {"start": v(120.89, 118.21) * mm, "end": v(121.28, 117.67) * mm});
            skArc(sketch, "E1598", {"start": v(117.26, 120.58) * mm, "mid": v(117.44, 120.03) * mm, "end": v(117.95, 119.74) * mm});
            skArc(sketch, "E1599", {"start": v(117.26, 120.58) * mm, "mid": v(117.26, 120.9) * mm, "end": v(117.26, 121.2) * mm});
            skArc(sketch, "E1600", {"start": v(117.95, 122.05) * mm, "mid": v(117.44, 121.76) * mm, "end": v(117.26, 121.2) * mm});
            skLineSegment(sketch, "E1601", {"start": v(117.95, 122.05) * mm, "end": v(118.46, 122.13) * mm});
            skLineSegment(sketch, "E1602", {"start": v(118.46, 122.13) * mm, "end": v(118.87, 122.2) * mm});
            skLineSegment(sketch, "E1603", {"start": v(118.87, 122.2) * mm, "end": v(119.07, 122.23) * mm});
            skLineSegment(sketch, "E1604", {"start": v(119.07, 122.23) * mm, "end": v(119.15, 122.24) * mm});
            skLineSegment(sketch, "E1605", {"start": v(119.15, 122.24) * mm, "end": v(119.26, 122.28) * mm});
            skLineSegment(sketch, "E1606", {"start": v(119.26, 122.28) * mm, "end": v(119.62, 122.45) * mm});
            skLineSegment(sketch, "E1607", {"start": v(119.62, 122.45) * mm, "end": v(120.04, 122.73) * mm});
            skLineSegment(sketch, "E1608", {"start": v(120.04, 122.73) * mm, "end": v(120.47, 123.1) * mm});
            skLineSegment(sketch, "E1609", {"start": v(120.47, 123.1) * mm, "end": v(120.89, 123.57) * mm});
            skLineSegment(sketch, "E1610", {"start": v(120.89, 123.57) * mm, "end": v(121.28, 124.12) * mm});
            skArc(sketch, "E1611", {"start": v(121.28, 124.12) * mm, "mid": v(121.1, 124.66) * mm, "end": v(120.9, 125.18) * mm});
            skLineSegment(sketch, "E1612", {"start": v(117, 124.62) * mm, "end": v(117.46, 124.9) * mm});
            skLineSegment(sketch, "E1613", {"start": v(117.46, 124.9) * mm, "end": v(117.8, 125.1) * mm});
            skLineSegment(sketch, "E1614", {"start": v(117.8, 125.1) * mm, "end": v(117.98, 125.2) * mm});
            skLineSegment(sketch, "E1615", {"start": v(117.98, 125.2) * mm, "end": v(118.05, 125.25) * mm});
            skLineSegment(sketch, "E1616", {"start": v(118.05, 125.25) * mm, "end": v(118.16, 125.3) * mm});
            skLineSegment(sketch, "E1617", {"start": v(118.16, 125.3) * mm, "end": v(118.55, 125.4) * mm});
            skLineSegment(sketch, "E1618", {"start": v(118.55, 125.4) * mm, "end": v(119.05, 125.44) * mm});
            skLineSegment(sketch, "E1619", {"start": v(119.05, 125.44) * mm, "end": v(119.62, 125.43) * mm});
            skLineSegment(sketch, "E1620", {"start": v(119.62, 125.43) * mm, "end": v(120.24, 125.34) * mm});
            skLineSegment(sketch, "E1621", {"start": v(120.24, 125.34) * mm, "end": v(120.9, 125.18) * mm});
            skArc(sketch, "E1622", {"start": v(115.94, 124.83) * mm, "mid": v(116.43, 124.52) * mm, "end": v(117, 124.62) * mm});
            skArc(sketch, "E1623", {"start": v(115.94, 124.83) * mm, "mid": v(115.74, 125.07) * mm, "end": v(115.54, 125.3) * mm});
            skArc(sketch, "E1624", {"start": v(115.52, 126.4) * mm, "mid": v(115.32, 125.84) * mm, "end": v(115.54, 125.3) * mm});
            skLineSegment(sketch, "E1625", {"start": v(115.52, 126.4) * mm, "end": v(115.87, 126.8) * mm});
            skLineSegment(sketch, "E1626", {"start": v(115.87, 126.8) * mm, "end": v(116.13, 127.1) * mm});
            skLineSegment(sketch, "E1627", {"start": v(116.13, 127.1) * mm, "end": v(116.27, 127.25) * mm});
            skLineSegment(sketch, "E1628", {"start": v(116.27, 127.25) * mm, "end": v(116.32, 127.32) * mm});
            skLineSegment(sketch, "E1629", {"start": v(116.32, 127.32) * mm, "end": v(116.38, 127.42) * mm});
            skLineSegment(sketch, "E1630", {"start": v(116.38, 127.42) * mm, "end": v(116.55, 127.78) * mm});
            skLineSegment(sketch, "E1631", {"start": v(116.55, 127.78) * mm, "end": v(116.69, 128.26) * mm});
            skLineSegment(sketch, "E1632", {"start": v(116.69, 128.26) * mm, "end": v(116.77, 128.83) * mm});
            skLineSegment(sketch, "E1633", {"start": v(116.77, 128.83) * mm, "end": v(116.8, 129.45) * mm});
            skLineSegment(sketch, "E1634", {"start": v(116.8, 129.45) * mm, "end": v(116.75, 130.12) * mm});
            skArc(sketch, "E1635", {"start": v(116.75, 130.12) * mm, "mid": v(116.26, 130.42) * mm, "end": v(115.77, 130.69) * mm});
            skLineSegment(sketch, "E1636", {"start": v(113.15, 127.76) * mm, "end": v(113.32, 128.26) * mm});
            skLineSegment(sketch, "E1637", {"start": v(113.32, 128.26) * mm, "end": v(113.45, 128.65) * mm});
            skLineSegment(sketch, "E1638", {"start": v(113.45, 128.65) * mm, "end": v(113.52, 128.84) * mm});
            skLineSegment(sketch, "E1639", {"start": v(113.52, 128.84) * mm, "end": v(113.55, 128.91) * mm});
            skLineSegment(sketch, "E1640", {"start": v(113.55, 128.91) * mm, "end": v(113.6, 129.02) * mm});
            skLineSegment(sketch, "E1641", {"start": v(113.6, 129.02) * mm, "end": v(113.84, 129.35) * mm});
            skLineSegment(sketch, "E1642", {"start": v(113.84, 129.35) * mm, "end": v(114.19, 129.7) * mm});
            skLineSegment(sketch, "E1643", {"start": v(114.19, 129.7) * mm, "end": v(114.63, 130.06) * mm});
            skLineSegment(sketch, "E1644", {"start": v(114.63, 130.06) * mm, "end": v(115.16, 130.4) * mm});
            skLineSegment(sketch, "E1645", {"start": v(115.16, 130.4) * mm, "end": v(115.77, 130.69) * mm});
            skArc(sketch, "E1646", {"start": v(112.2, 127.23) * mm, "mid": v(112.77, 127.32) * mm, "end": v(113.15, 127.76) * mm});
            skArc(sketch, "E1647", {"start": v(112.2, 127.23) * mm, "mid": v(111.9, 127.3) * mm, "end": v(111.59, 127.34) * mm});
            skArc(sketch, "E1648", {"start": v(110.87, 128.16) * mm, "mid": v(111.07, 127.62) * mm, "end": v(111.59, 127.34) * mm});
            skLineSegment(sketch, "E1649", {"start": v(110.87, 128.16) * mm, "end": v(110.88, 128.7) * mm});
            skLineSegment(sketch, "E1650", {"start": v(110.88, 128.7) * mm, "end": v(110.89, 129.1) * mm});
            skLineSegment(sketch, "E1651", {"start": v(110.89, 129.1) * mm, "end": v(110.9, 129.3) * mm});
            skLineSegment(sketch, "E1652", {"start": v(110.9, 129.3) * mm, "end": v(110.89, 129.38) * mm});
            skLineSegment(sketch, "E1653", {"start": v(110.89, 129.38) * mm, "end": v(110.87, 129.5) * mm});
            skLineSegment(sketch, "E1654", {"start": v(110.87, 129.5) * mm, "end": v(110.77, 129.89) * mm});
            skLineSegment(sketch, "E1655", {"start": v(110.77, 129.89) * mm, "end": v(110.56, 130.34) * mm});
            skLineSegment(sketch, "E1656", {"start": v(110.56, 130.34) * mm, "end": v(110.27, 130.83) * mm});
            skLineSegment(sketch, "E1657", {"start": v(110.27, 130.83) * mm, "end": v(109.88, 131.33) * mm});
            skLineSegment(sketch, "E1658", {"start": v(109.88, 131.33) * mm, "end": v(109.41, 131.8) * mm});
            skArc(sketch, "E1659", {"start": v(109.41, 131.8) * mm, "mid": v(108.85, 131.73) * mm, "end": v(108.3, 131.61) * mm});
            skLineSegment(sketch, "E1660", {"start": v(108.17, 127.69) * mm, "end": v(107.99, 128.18) * mm});
            skLineSegment(sketch, "E1661", {"start": v(107.99, 128.18) * mm, "end": v(107.84, 128.56) * mm});
            skLineSegment(sketch, "E1662", {"start": v(107.84, 128.56) * mm, "end": v(107.77, 128.75) * mm});
            skLineSegment(sketch, "E1663", {"start": v(107.77, 128.75) * mm, "end": v(107.74, 128.83) * mm});
            skLineSegment(sketch, "E1664", {"start": v(107.74, 128.83) * mm, "end": v(107.72, 128.94) * mm});
            skLineSegment(sketch, "E1665", {"start": v(107.72, 128.94) * mm, "end": v(107.69, 129.34) * mm});
            skLineSegment(sketch, "E1666", {"start": v(107.69, 129.34) * mm, "end": v(107.72, 129.84) * mm});
            skLineSegment(sketch, "E1667", {"start": v(107.72, 129.84) * mm, "end": v(107.83, 130.4) * mm});
            skLineSegment(sketch, "E1668", {"start": v(107.83, 130.4) * mm, "end": v(108.03, 131) * mm});
            skLineSegment(sketch, "E1669", {"start": v(108.03, 131) * mm, "end": v(108.3, 131.61) * mm});
            skArc(sketch, "E1670", {"start": v(107.79, 126.67) * mm, "mid": v(108.17, 127.1) * mm, "end": v(108.17, 127.69) * mm});
            skArc(sketch, "E1671", {"start": v(107.79, 126.67) * mm, "mid": v(107.51, 126.52) * mm, "end": v(107.25, 126.36) * mm});
            skArc(sketch, "E1672", {"start": v(106.17, 126.53) * mm, "mid": v(106.68, 126.24) * mm, "end": v(107.25, 126.36) * mm});
            skLineSegment(sketch, "E1673", {"start": v(106.17, 126.53) * mm, "end": v(105.84, 126.94) * mm});
            skLineSegment(sketch, "E1674", {"start": v(105.84, 126.94) * mm, "end": v(105.59, 127.26) * mm});
            skLineSegment(sketch, "E1675", {"start": v(105.59, 127.26) * mm, "end": v(105.46, 127.42) * mm});
            skLineSegment(sketch, "E1676", {"start": v(105.46, 127.42) * mm, "end": v(105.4, 127.48) * mm});
            skLineSegment(sketch, "E1677", {"start": v(105.4, 127.48) * mm, "end": v(105.31, 127.56) * mm});
            skLineSegment(sketch, "E1678", {"start": v(105.31, 127.56) * mm, "end": v(104.98, 127.78) * mm});
            skLineSegment(sketch, "E1679", {"start": v(104.98, 127.78) * mm, "end": v(104.53, 128) * mm});
            skLineSegment(sketch, "E1680", {"start": v(104.53, 128) * mm, "end": v(104, 128.19) * mm});
            skLineSegment(sketch, "E1681", {"start": v(104, 128.19) * mm, "end": v(103.38, 128.32) * mm});
            skLineSegment(sketch, "E1682", {"start": v(103.38, 128.32) * mm, "end": v(102.71, 128.39) * mm});
            skArc(sketch, "E1683", {"start": v(102.71, 128.39) * mm, "mid": v(102.34, 127.96) * mm, "end": v(101.99, 127.52) * mm});
            skLineSegment(sketch, "E1684", {"start": v(104.41, 124.43) * mm, "end": v(103.95, 124.69) * mm});
            skLineSegment(sketch, "E1685", {"start": v(103.95, 124.69) * mm, "end": v(103.6, 124.89) * mm});
            skLineSegment(sketch, "E1686", {"start": v(103.6, 124.89) * mm, "end": v(103.42, 124.99) * mm});
            skLineSegment(sketch, "E1687", {"start": v(103.42, 124.99) * mm, "end": v(103.35, 125.03) * mm});
            skLineSegment(sketch, "E1688", {"start": v(103.35, 125.03) * mm, "end": v(103.26, 125.1) * mm});
            skLineSegment(sketch, "E1689", {"start": v(103.26, 125.1) * mm, "end": v(102.97, 125.39) * mm});
            skLineSegment(sketch, "E1690", {"start": v(102.97, 125.39) * mm, "end": v(102.68, 125.8) * mm});
            skLineSegment(sketch, "E1691", {"start": v(102.68, 125.8) * mm, "end": v(102.4, 126.3) * mm});
            skLineSegment(sketch, "E1692", {"start": v(102.4, 126.3) * mm, "end": v(102.17, 126.87) * mm});
            skLineSegment(sketch, "E1693", {"start": v(102.17, 126.87) * mm, "end": v(101.99, 127.52) * mm});
            skArc(sketch, "E1694", {"start": v(104.77, 123.4) * mm, "mid": v(104.79, 123.99) * mm, "end": v(104.41, 124.43) * mm});
            skArc(sketch, "E1695", {"start": v(104.77, 123.4) * mm, "mid": v(104.66, 123.12) * mm, "end": v(104.56, 122.82) * mm});
            skArc(sketch, "E1696", {"start": v(103.62, 122.26) * mm, "mid": v(104.2, 122.37) * mm, "end": v(104.56, 122.82) * mm});
            skLineSegment(sketch, "E1697", {"start": v(103.62, 122.26) * mm, "end": v(103.1, 122.36) * mm});
            skLineSegment(sketch, "E1698", {"start": v(103.1, 122.36) * mm, "end": v(102.7, 122.44) * mm});
            skLineSegment(sketch, "E1699", {"start": v(102.7, 122.44) * mm, "end": v(102.5, 122.48) * mm});
            skLineSegment(sketch, "E1700", {"start": v(102.5, 122.48) * mm, "end": v(102.43, 122.49) * mm});
            skLineSegment(sketch, "E1701", {"start": v(102.43, 122.49) * mm, "end": v(102.3, 122.5) * mm});
            skLineSegment(sketch, "E1702", {"start": v(102.3, 122.5) * mm, "end": v(101.9, 122.46) * mm});
            skLineSegment(sketch, "E1703", {"start": v(101.9, 122.46) * mm, "end": v(101.42, 122.34) * mm});
            skLineSegment(sketch, "E1704", {"start": v(101.42, 122.34) * mm, "end": v(100.9, 122.13) * mm});
            skLineSegment(sketch, "E1705", {"start": v(100.9, 122.13) * mm, "end": v(100.34, 121.83) * mm});
            skLineSegment(sketch, "E1706", {"start": v(100.34, 121.83) * mm, "end": v(99.78, 121.46) * mm});
            skArc(sketch, "E1707", {"start": v(99.78, 121.46) * mm, "mid": v(99.76, 120.9) * mm, "end": v(99.78, 120.33) * mm});
            skLineSegment(sketch, "E1708", {"start": v(103.62, 119.52) * mm, "end": v(103.1, 119.42) * mm});
            skLineSegment(sketch, "E1709", {"start": v(103.1, 119.42) * mm, "end": v(102.7, 119.35) * mm});
            skLineSegment(sketch, "E1710", {"start": v(102.7, 119.35) * mm, "end": v(102.5, 119.3) * mm});
            skLineSegment(sketch, "E1711", {"start": v(102.5, 119.3) * mm, "end": v(102.43, 119.3) * mm});
            skLineSegment(sketch, "E1712", {"start": v(102.43, 119.3) * mm, "end": v(102.3, 119.3) * mm});
            skLineSegment(sketch, "E1713", {"start": v(102.3, 119.3) * mm, "end": v(101.9, 119.33) * mm});
            skLineSegment(sketch, "E1714", {"start": v(101.9, 119.33) * mm, "end": v(101.42, 119.45) * mm});
            skCircle(sketch, "E1715", {"center": v(-5.5, 118.23) * mm, "radius": 3.1 * mm});
            skLineSegment(sketch, "E1716", {"start": v(101.42, 119.45) * mm, "end": v(100.9, 119.66) * mm});
            skLineSegment(sketch, "E1717", {"start": v(100.9, 119.66) * mm, "end": v(100.34, 119.95) * mm});
            skLineSegment(sketch, "E1718", {"start": v(100.34, 119.95) * mm, "end": v(99.78, 120.33) * mm});
            skArc(sketch, "E1719", {"start": v(104.56, 118.96) * mm, "mid": v(104.2, 119.42) * mm, "end": v(103.62, 119.52) * mm});
            skArc(sketch, "E1720", {"start": v(104.56, 118.96) * mm, "mid": v(104.66, 118.67) * mm, "end": v(104.77, 118.38) * mm});
            skArc(sketch, "E1721", {"start": v(104.41, 117.35) * mm, "mid": v(104.79, 117.8) * mm, "end": v(104.77, 118.38) * mm});
            skLineSegment(sketch, "E1722", {"start": v(104.41, 117.35) * mm, "end": v(103.95, 117.1) * mm});
            skLineSegment(sketch, "E1723", {"start": v(103.95, 117.1) * mm, "end": v(103.6, 116.9) * mm});
            skLineSegment(sketch, "E1724", {"start": v(103.6, 116.9) * mm, "end": v(103.42, 116.8) * mm});
            skLineSegment(sketch, "E1725", {"start": v(103.42, 116.8) * mm, "end": v(103.35, 116.76) * mm});
            skLineSegment(sketch, "E1726", {"start": v(103.35, 116.76) * mm, "end": v(103.26, 116.68) * mm});
            skLineSegment(sketch, "E1727", {"start": v(103.26, 116.68) * mm, "end": v(102.97, 116.4) * mm});
            skLineSegment(sketch, "E1728", {"start": v(102.97, 116.4) * mm, "end": v(102.68, 116) * mm});
            skLineSegment(sketch, "E1729", {"start": v(102.68, 116) * mm, "end": v(102.4, 115.5) * mm});
            skLineSegment(sketch, "E1730", {"start": v(102.4, 115.5) * mm, "end": v(102.17, 114.91) * mm});
            skLineSegment(sketch, "E1731", {"start": v(102.17, 114.91) * mm, "end": v(101.99, 114.26) * mm});
            skArc(sketch, "E1732", {"start": v(101.99, 114.26) * mm, "mid": v(102.34, 113.82) * mm, "end": v(102.71, 113.4) * mm});
            skLineSegment(sketch, "E1733", {"start": v(106.17, 115.25) * mm, "end": v(105.84, 114.84) * mm});
            skLineSegment(sketch, "E1734", {"start": v(105.84, 114.84) * mm, "end": v(105.59, 114.53) * mm});
            skLineSegment(sketch, "E1735", {"start": v(105.59, 114.53) * mm, "end": v(105.46, 114.37) * mm});
            skLineSegment(sketch, "E1736", {"start": v(105.46, 114.37) * mm, "end": v(105.4, 114.3) * mm});
            skLineSegment(sketch, "E1737", {"start": v(105.4, 114.3) * mm, "end": v(105.31, 114.23) * mm});
            skLineSegment(sketch, "E1738", {"start": v(105.31, 114.23) * mm, "end": v(104.98, 114) * mm});
            skLineSegment(sketch, "E1739", {"start": v(104.98, 114) * mm, "end": v(104.53, 113.78) * mm});
            skLineSegment(sketch, "E1740", {"start": v(104.53, 113.78) * mm, "end": v(104, 113.6) * mm});
            skLineSegment(sketch, "E1741", {"start": v(104, 113.6) * mm, "end": v(103.38, 113.47) * mm});
            skLineSegment(sketch, "E1742", {"start": v(103.38, 113.47) * mm, "end": v(102.71, 113.4) * mm});
            skArc(sketch, "E1743", {"start": v(107.25, 115.42) * mm, "mid": v(106.68, 115.54) * mm, "end": v(106.17, 115.25) * mm});
            skArc(sketch, "E1744", {"start": v(107.25, 115.42) * mm, "mid": v(107.51, 115.26) * mm, "end": v(107.79, 115.12) * mm});
            skArc(sketch, "E1745", {"start": v(108.17, 114.1) * mm, "mid": v(108.17, 114.68) * mm, "end": v(107.79, 115.12) * mm});
            skLineSegment(sketch, "E1746", {"start": v(108.17, 114.1) * mm, "end": v(107.99, 113.6) * mm});
            skLineSegment(sketch, "E1747", {"start": v(107.99, 113.6) * mm, "end": v(107.84, 113.22) * mm});
            skLineSegment(sketch, "E1748", {"start": v(107.84, 113.22) * mm, "end": v(107.77, 113.03) * mm});
            skLineSegment(sketch, "E1749", {"start": v(107.77, 113.03) * mm, "end": v(107.74, 112.96) * mm});
            skLineSegment(sketch, "E1750", {"start": v(107.74, 112.96) * mm, "end": v(107.72, 112.84) * mm});
            skLineSegment(sketch, "E1751", {"start": v(107.72, 112.84) * mm, "end": v(107.69, 112.44) * mm});
            skLineSegment(sketch, "E1752", {"start": v(107.69, 112.44) * mm, "end": v(107.72, 111.94) * mm});
            skLineSegment(sketch, "E1753", {"start": v(107.72, 111.94) * mm, "end": v(107.83, 111.38) * mm});
            skLineSegment(sketch, "E1754", {"start": v(107.83, 111.38) * mm, "end": v(108.03, 110.79) * mm});
            skLineSegment(sketch, "E1755", {"start": v(108.03, 110.79) * mm, "end": v(108.3, 110.17) * mm});
            skArc(sketch, "E1756", {"start": v(108.3, 110.17) * mm, "mid": v(108.85, 110.06) * mm, "end": v(109.41, 109.98) * mm});
            skLineSegment(sketch, "E1757", {"start": v(110.87, 113.62) * mm, "end": v(110.88, 113.1) * mm});
            skLineSegment(sketch, "E1758", {"start": v(110.88, 113.1) * mm, "end": v(110.89, 112.69) * mm});
            skLineSegment(sketch, "E1759", {"start": v(110.89, 112.69) * mm, "end": v(110.9, 112.48) * mm});
            skLineSegment(sketch, "E1760", {"start": v(110.9, 112.48) * mm, "end": v(110.89, 112.4) * mm});
            skLineSegment(sketch, "E1761", {"start": v(110.89, 112.4) * mm, "end": v(110.87, 112.28) * mm});
            skLineSegment(sketch, "E1762", {"start": v(110.87, 112.28) * mm, "end": v(110.77, 111.9) * mm});
            skLineSegment(sketch, "E1763", {"start": v(110.77, 111.9) * mm, "end": v(110.56, 111.44) * mm});
            skLineSegment(sketch, "E1764", {"start": v(110.56, 111.44) * mm, "end": v(110.27, 110.95) * mm});
            skLineSegment(sketch, "E1765", {"start": v(110.27, 110.95) * mm, "end": v(109.88, 110.46) * mm});
            skLineSegment(sketch, "E1766", {"start": v(109.88, 110.46) * mm, "end": v(109.41, 109.98) * mm});
            skArc(sketch, "E1767", {"start": v(111.59, 114.45) * mm, "mid": v(111.07, 114.17) * mm, "end": v(110.87, 113.62) * mm});
            skArc(sketch, "E1768", {"start": v(111.59, 114.45) * mm, "mid": v(111.9, 114.5) * mm, "end": v(112.2, 114.55) * mm});
            skCircle(sketch, "E1769", {"center": v(10.75, 33.21) * mm, "radius": 15 * mm});
            skCircle(sketch, "E1770", {"center": v(10.75, 33.21) * mm, "radius": 0.23 * mm});
            skCircle(sketch, "E1771", {"center": v(10.75, 33.21) * mm, "radius": 3.1 * mm});
            skSolve(sketch);
        }
        {
            var Q0;
            Q0 = qSketchRegion(id + "F0", true);
            extrude(context, id + "F1", {"entities" : qUnion([Q0]), "depth" : 8 * mm, "offsetDistance" : 25 * mm});
        }
    });
